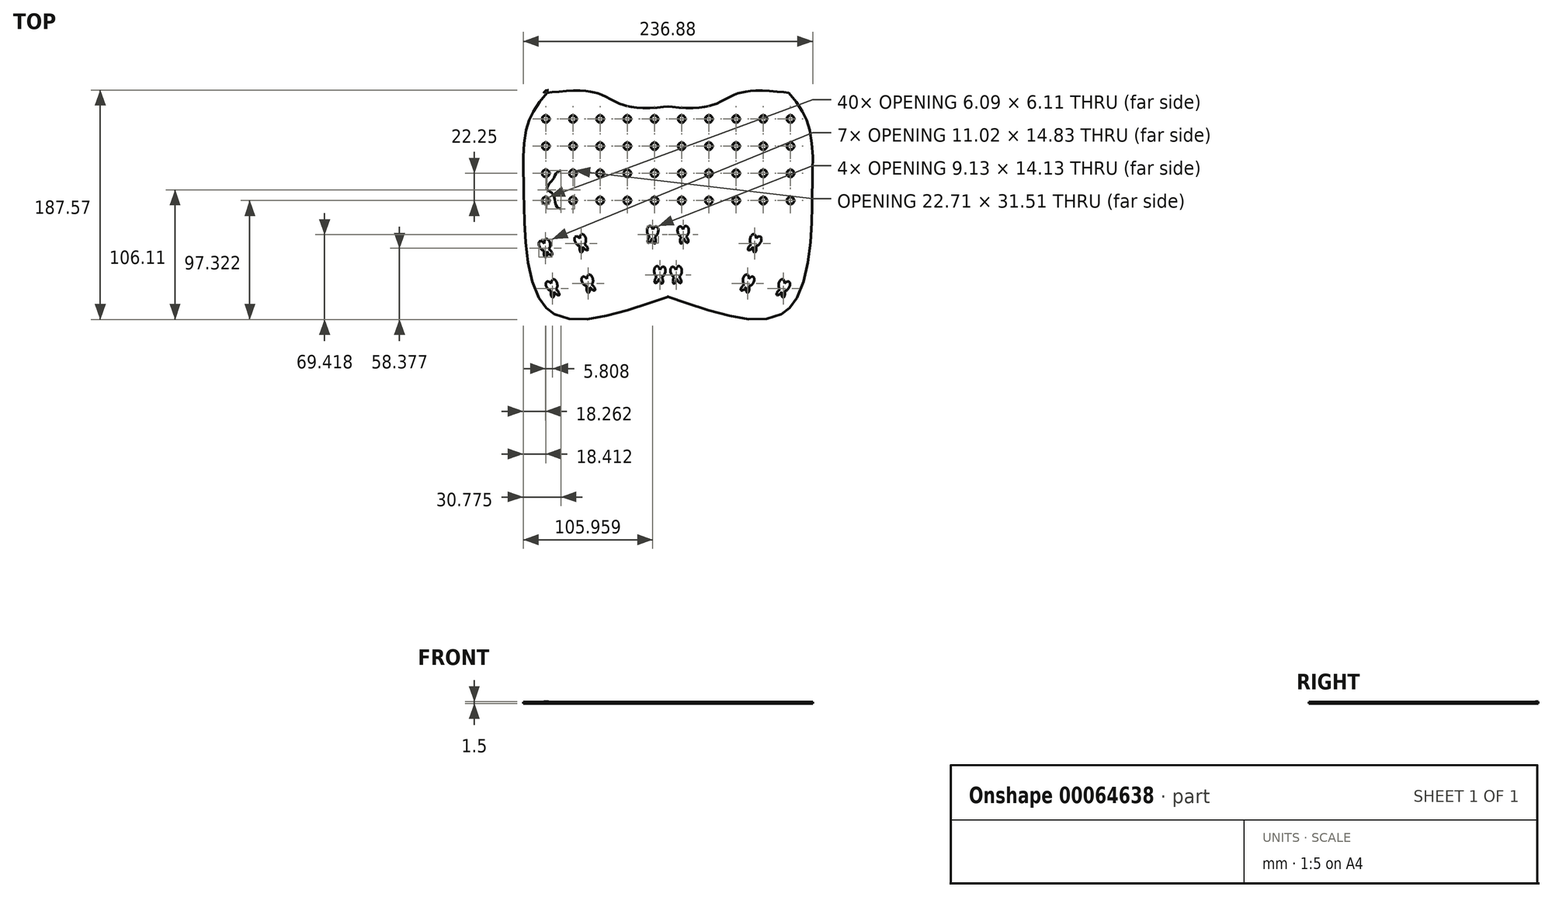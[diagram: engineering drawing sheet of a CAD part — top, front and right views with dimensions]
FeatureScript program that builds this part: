
annotation { "Feature Type Name" : "Feature", "Feature Type Description" : "" }
export const myFeature = defineFeature(function(context is Context, id is Id, definition is map)
    precondition{}
    {
        {
            var Q0;
            Q0=qCreatedBy(makeId("Top.planeOp"),FACE);
            var sketch = newSketch(context, id + "F0", { "sketchPlane" : qUnion([Q0])});
            skLineSegment(sketch, "E0", {"start": v(-116.5, 0) * mm, "end": v(139.03, 0) * mm, "construction": true});
            skLineSegment(sketch, "E1.0", {"start": v(-116.5, -90) * mm, "end": v(139.03, -90) * mm, "construction": true});
            skLineSegment(sketch, "E2.0", {"start": v(-116.5, 90) * mm, "end": v(139.03, 90) * mm, "construction": true});
            skLineSegment(sketch, "E3", {"start": v(0, 90) * mm, "end": v(0, -92.69) * mm, "construction": true});
            skLineSegment(sketch, "E4.0", {"start": v(-100, 90) * mm, "end": v(-100, -92.69) * mm, "construction": true});
            skLineSegment(sketch, "E5.0", {"start": v(-120, 90) * mm, "end": v(-120, -92.69) * mm, "construction": true});
            skLineSegment(sketch, "E6.0", {"start": v(120, 90) * mm, "end": v(120, -92.69) * mm, "construction": true});
            skLineSegment(sketch, "E7.0", {"start": v(100, 90) * mm, "end": v(100, -92.69) * mm, "construction": true});
            skFitSpline(sketch, "E8", {"points": [v(-100, 90) * mm, v(-114.02, 69.47) * mm, v(-120, 43.4) * mm, v(-120, 8.31) * mm, v(-100, -90) * mm, v(0, -80.79) * mm], "startDerivative": vector(-114.58, -138.92) * mm, "endDerivative": vector(433.2, 151.03) * mm});
            skFitSpline(sketch, "E9", {"points": [v(0, 78.79) * mm, v(-34.86, 79.72) * mm, v(-58.45, 90) * mm, v(-100, 90) * mm], "startDerivative": vector(-110.99, -8.68) * mm, "endDerivative": vector(-123.02, -12.63) * mm});
            skArc(sketch, "E10.filletArc", {"start": v(-97.54, 90.25) * mm, "mid": v(-99.77, 89.57) * mm, "end": v(-101.57, 88.09) * mm});
            skFitSpline(sketch, "E11.MirrorCS", {"points": [v(0, 78.79) * mm, v(34.86, 79.72) * mm, v(58.45, 90) * mm, v(100, 90) * mm], "startDerivative": vector(110.99, -8.68) * mm, "endDerivative": vector(123.02, -12.63) * mm});
            skFitSpline(sketch, "E12.MirrorCS", {"points": [v(100, 90) * mm, v(114.02, 69.47) * mm, v(120, 43.4) * mm, v(120, 8.31) * mm, v(100, -90) * mm, v(0, -80.79) * mm], "startDerivative": vector(114.58, -138.92) * mm, "endDerivative": vector(-433.2, 151.03) * mm});
            skArc(sketch, "E13.MirrorCS", {"start": v(97.54, 90.25) * mm, "mid": v(99.77, 89.57) * mm, "end": v(101.57, 88.09) * mm});
            skFitSpline(sketch, "E14.0", {"points": [v(0.16, 76.8) * mm, v(-2.16, 76.61) * mm, v(-6.8, 76.25) * mm, v(-13.69, 75.85) * mm, v(-20.42, 75.74) * mm, v(-25.82, 76.02) * mm, v(-29.97, 76.55) * mm, v(-32.48, 77.03) * mm, v(-34.44, 77.51) * mm, v(-36.35, 78.06) * mm, v(-38.65, 78.88) * mm, v(-41.26, 80) * mm, v(-44.61, 81.61) * mm, v(-47.82, 83.32) * mm, v(-51.02, 84.95) * mm, v(-53.45, 86.09) * mm, v(-55.94, 87.11) * mm, v(-58.1, 87.84) * mm, v(-59.9, 88.32) * mm, v(-61.76, 88.75) * mm, v(-64.2, 89.18) * mm, v(-67.3, 89.53) * mm, v(-71.61, 89.8) * mm, v(-77.33, 89.83) * mm, v(-84.6, 89.45) * mm, v(-92.12, 88.8) * mm, v(-97.23, 88.27) * mm, v(-99.8, 88.01) * mm]});
            skFitSpline(sketch, "E15.0", {"points": [v(-0.16, 76.8) * mm, v(2.16, 76.61) * mm, v(6.8, 76.25) * mm, v(13.69, 75.85) * mm, v(20.42, 75.74) * mm, v(25.82, 76.02) * mm, v(29.97, 76.55) * mm, v(32.48, 77.03) * mm, v(34.44, 77.51) * mm, v(36.35, 78.06) * mm, v(38.65, 78.88) * mm, v(41.26, 80) * mm, v(44.61, 81.61) * mm, v(47.82, 83.32) * mm, v(51.02, 84.95) * mm, v(53.45, 86.09) * mm, v(55.94, 87.11) * mm, v(58.1, 87.84) * mm, v(59.9, 88.32) * mm, v(61.76, 88.75) * mm, v(64.2, 89.18) * mm, v(67.3, 89.53) * mm, v(71.61, 89.8) * mm, v(77.33, 89.83) * mm, v(84.6, 89.45) * mm, v(92.12, 88.8) * mm, v(97.23, 88.27) * mm, v(99.8, 88.01) * mm]});
            skFitSpline(sketch, "E16.0", {"points": [v(98.46, 88.73) * mm, v(99.65, 87.28) * mm, v(102.03, 84.4) * mm, v(105.43, 80.03) * mm, v(108.04, 76.27) * mm, v(109.92, 73.15) * mm, v(111.23, 70.74) * mm, v(112.4, 68.25) * mm, v(113.46, 65.66) * mm, v(114.39, 62.97) * mm, v(115.47, 59.3) * mm, v(116.56, 54.56) * mm, v(117.47, 48.83) * mm, v(118.05, 43.2) * mm, v(118.35, 37.81) * mm, v(118.44, 32.29) * mm, v(118.37, 26.22) * mm, v(118.24, 20.4) * mm, v(118.12, 15.08) * mm, v(118.05, 11.45) * mm, v(118, 8.34) * mm, v(117.95, 5.08) * mm, v(117.9, 0.76) * mm, v(117.8, -4.78) * mm, v(117.63, -12.53) * mm, v(117.26, -22.79) * mm, v(116.37, -35.51) * mm, v(114.87, -48.17) * mm, v(112.6, -60.27) * mm, v(109.38, -71.31) * mm, v(105.8, -79.21) * mm, v(102.33, -84.5) * mm, v(99.92, -87.34) * mm, v(97.83, -89.3) * mm, v(95.62, -91.08) * mm, v(91.46, -93.7) * mm, v(84.64, -96.16) * mm, v(75.12, -97.29) * mm, v(64.45, -96.8) * mm, v(52.83, -94.9) * mm, v(40.45, -91.9) * mm, v(23.2, -86.76) * mm, v(9.68, -82.05) * mm, v(0.66, -78.9) * mm]});
            skFitSpline(sketch, "E17.0", {"points": [v(-98.46, 88.73) * mm, v(-99.65, 87.28) * mm, v(-102.03, 84.4) * mm, v(-105.43, 80.03) * mm, v(-108.04, 76.27) * mm, v(-109.92, 73.15) * mm, v(-111.23, 70.74) * mm, v(-112.4, 68.25) * mm, v(-113.46, 65.66) * mm, v(-114.39, 62.97) * mm, v(-115.47, 59.3) * mm, v(-116.56, 54.56) * mm, v(-117.47, 48.83) * mm, v(-118.05, 43.2) * mm, v(-118.35, 37.81) * mm, v(-118.44, 32.29) * mm, v(-118.37, 26.22) * mm, v(-118.24, 20.4) * mm, v(-118.12, 15.08) * mm, v(-118.05, 11.45) * mm, v(-118, 8.34) * mm, v(-117.95, 5.08) * mm, v(-117.9, 0.76) * mm, v(-117.8, -4.78) * mm, v(-117.63, -12.53) * mm, v(-117.26, -22.79) * mm, v(-116.37, -35.51) * mm, v(-114.87, -48.17) * mm, v(-112.6, -60.27) * mm, v(-109.38, -71.31) * mm, v(-105.8, -79.21) * mm, v(-102.33, -84.5) * mm, v(-99.92, -87.34) * mm, v(-97.83, -89.3) * mm, v(-95.62, -91.08) * mm, v(-91.46, -93.7) * mm, v(-84.64, -96.16) * mm, v(-75.12, -97.29) * mm, v(-64.45, -96.8) * mm, v(-52.83, -94.9) * mm, v(-40.45, -91.9) * mm, v(-23.2, -86.76) * mm, v(-9.68, -82.05) * mm, v(-0.66, -78.9) * mm]});
            skFitSpline(sketch, "E18", {"points": [v(-0.66, -78.9) * mm, v(0, -78.63) * mm, v(0.66, -78.9) * mm], "startDerivative": vector(1.32, 0.81) * mm, "endDerivative": vector(1.32, -0.81) * mm});
            skArc(sketch, "E19.filletArc", {"start": v(100.56, 86.17) * mm, "mid": v(98.75, 87.66) * mm, "end": v(96.52, 88.35) * mm});
            skArc(sketch, "E20.filletArc", {"start": v(-96.52, 88.35) * mm, "mid": v(-98.75, 87.66) * mm, "end": v(-100.56, 86.17) * mm});
            skCircle(sketch, "E21", {"center": v(-100, 0) * mm, "radius": 2.04 * mm});
            skEllipticalArc(sketch, "E22", {});
            skEllipticalArc(sketch, "E23.1.0", {});
            skEllipticalArc(sketch, "E23.2.0", {});
            skEllipticalArc(sketch, "E24.1.3.0", {});
            skEllipticalArc(sketch, "E24.1.4.0", {});
            skEllipticalArc(sketch, "E24.1.5.0", {});
            skEllipticalArc(sketch, "E24.1.6.0", {});
            skEllipticalArc(sketch, "E24.1.7.0", {});
            skEllipticalArc(sketch, "E24.1.8.0", {});
            skEllipticalArc(sketch, "E24.1.9.0", {});
            skEllipticalArc(sketch, "E24.1.10.0", {});
            skEllipticalArc(sketch, "E24.1.11.0", {});
            skEllipticalArc(sketch, "E24.1.12.0", {});
            skEllipticalArc(sketch, "E24.1.13.0", {});
            skEllipticalArc(sketch, "E24.1.14.0", {});
            skEllipticalArc(sketch, "E25.trimOffspring", {});
            skEllipticalArc(sketch, "E26.trimOffspring", {});
            skEllipticalArc(sketch, "E27.trimOffspring", {});
            skEllipticalArc(sketch, "E28.trimOffspring", {});
            skEllipticalArc(sketch, "E29.trimOffspring", {});
            skEllipticalArc(sketch, "E30.trimOffspring", {});
            skEllipticalArc(sketch, "E31.trimOffspring", {});
            skEllipticalArc(sketch, "E32.trimOffspring", {});
            skEllipticalArc(sketch, "E33.trimOffspring", {});
            skEllipticalArc(sketch, "E34.trimOffspring", {});
            skEllipticalArc(sketch, "E35.trimOffspring", {});
            skEllipticalArc(sketch, "E36.trimOffspring", {});
            skEllipticalArc(sketch, "E37.trimOffspring", {});
            skEllipticalArc(sketch, "E38.trimOffspring", {});
            skEllipticalArc(sketch, "E39.trimOffspring", {});
            skEllipticalArc(sketch, "E40.0.1.0", {});
            skEllipticalArc(sketch, "E40.0.1.1", {});
            skEllipticalArc(sketch, "E40.0.1.2", {});
            skEllipticalArc(sketch, "E40.0.1.3", {});
            skEllipticalArc(sketch, "E40.0.1.4", {});
            skEllipticalArc(sketch, "E40.0.1.5", {});
            skEllipticalArc(sketch, "E40.0.1.6", {});
            skEllipticalArc(sketch, "E40.0.1.7", {});
            skEllipticalArc(sketch, "E40.0.1.8", {});
            skEllipticalArc(sketch, "E40.0.1.9", {});
            skEllipticalArc(sketch, "E40.0.1.10", {});
            skEllipticalArc(sketch, "E40.0.1.11", {});
            skEllipticalArc(sketch, "E40.0.1.12", {});
            skEllipticalArc(sketch, "E40.0.1.13", {});
            skEllipticalArc(sketch, "E40.0.1.14", {});
            skEllipticalArc(sketch, "E40.0.2.0", {});
            skEllipticalArc(sketch, "E40.0.2.1", {});
            skEllipticalArc(sketch, "E40.0.2.2", {});
            skEllipticalArc(sketch, "E40.0.2.3", {});
            skEllipticalArc(sketch, "E40.0.2.4", {});
            skEllipticalArc(sketch, "E40.0.2.5", {});
            skEllipticalArc(sketch, "E40.0.2.6", {});
            skEllipticalArc(sketch, "E40.0.2.7", {});
            skEllipticalArc(sketch, "E40.0.2.8", {});
            skEllipticalArc(sketch, "E40.0.2.9", {});
            skEllipticalArc(sketch, "E40.0.2.10", {});
            skEllipticalArc(sketch, "E40.0.2.11", {});
            skEllipticalArc(sketch, "E40.0.2.12", {});
            skEllipticalArc(sketch, "E40.0.2.13", {});
            skEllipticalArc(sketch, "E40.0.2.14", {});
            skEllipticalArc(sketch, "E40.0.3.0", {});
            skEllipticalArc(sketch, "E40.0.3.1", {});
            skEllipticalArc(sketch, "E40.0.3.2", {});
            skEllipticalArc(sketch, "E40.0.3.3", {});
            skEllipticalArc(sketch, "E40.0.3.4", {});
            skEllipticalArc(sketch, "E40.0.3.5", {});
            skEllipticalArc(sketch, "E40.0.3.6", {});
            skEllipticalArc(sketch, "E40.0.3.7", {});
            skEllipticalArc(sketch, "E40.0.3.8", {});
            skEllipticalArc(sketch, "E40.0.3.9", {});
            skEllipticalArc(sketch, "E40.0.3.10", {});
            skEllipticalArc(sketch, "E40.0.3.11", {});
            skEllipticalArc(sketch, "E40.0.3.12", {});
            skEllipticalArc(sketch, "E40.0.3.13", {});
            skEllipticalArc(sketch, "E40.0.3.14", {});
            skEllipticalArc(sketch, "E40.1.0.0", {});
            skEllipticalArc(sketch, "E40.1.0.1", {});
            skEllipticalArc(sketch, "E40.1.0.2", {});
            skEllipticalArc(sketch, "E40.1.0.3", {});
            skEllipticalArc(sketch, "E40.1.0.4", {});
            skEllipticalArc(sketch, "E40.1.0.5", {});
            skEllipticalArc(sketch, "E40.1.0.6", {});
            skEllipticalArc(sketch, "E40.1.0.7", {});
            skEllipticalArc(sketch, "E40.1.0.8", {});
            skEllipticalArc(sketch, "E40.1.0.9", {});
            skEllipticalArc(sketch, "E40.1.0.10", {});
            skEllipticalArc(sketch, "E40.1.0.11", {});
            skEllipticalArc(sketch, "E40.1.0.12", {});
            skEllipticalArc(sketch, "E40.1.0.13", {});
            skEllipticalArc(sketch, "E40.1.0.14", {});
            skEllipticalArc(sketch, "E40.1.1.0", {});
            skEllipticalArc(sketch, "E40.1.1.1", {});
            skEllipticalArc(sketch, "E40.1.1.2", {});
            skEllipticalArc(sketch, "E40.1.1.3", {});
            skEllipticalArc(sketch, "E40.1.1.4", {});
            skEllipticalArc(sketch, "E40.1.1.5", {});
            skEllipticalArc(sketch, "E40.1.1.6", {});
            skEllipticalArc(sketch, "E40.1.1.7", {});
            skEllipticalArc(sketch, "E40.1.1.8", {});
            skEllipticalArc(sketch, "E40.1.1.9", {});
            skEllipticalArc(sketch, "E40.1.1.10", {});
            skEllipticalArc(sketch, "E40.1.1.11", {});
            skEllipticalArc(sketch, "E40.1.1.12", {});
            skEllipticalArc(sketch, "E40.1.1.13", {});
            skEllipticalArc(sketch, "E40.1.1.14", {});
            skEllipticalArc(sketch, "E40.1.2.0", {});
            skEllipticalArc(sketch, "E40.1.2.1", {});
            skEllipticalArc(sketch, "E40.1.2.2", {});
            skEllipticalArc(sketch, "E40.1.2.3", {});
            skEllipticalArc(sketch, "E40.1.2.4", {});
            skEllipticalArc(sketch, "E40.1.2.5", {});
            skEllipticalArc(sketch, "E40.1.2.6", {});
            skEllipticalArc(sketch, "E40.1.2.7", {});
            skEllipticalArc(sketch, "E40.1.2.8", {});
            skEllipticalArc(sketch, "E40.1.2.9", {});
            skEllipticalArc(sketch, "E40.1.2.10", {});
            skEllipticalArc(sketch, "E40.1.2.11", {});
            skEllipticalArc(sketch, "E40.1.2.12", {});
            skEllipticalArc(sketch, "E40.1.2.13", {});
            skEllipticalArc(sketch, "E40.1.2.14", {});
            skEllipticalArc(sketch, "E40.1.3.0", {});
            skEllipticalArc(sketch, "E40.1.3.1", {});
            skEllipticalArc(sketch, "E40.1.3.2", {});
            skEllipticalArc(sketch, "E40.1.3.3", {});
            skEllipticalArc(sketch, "E40.1.3.4", {});
            skEllipticalArc(sketch, "E40.1.3.5", {});
            skEllipticalArc(sketch, "E40.1.3.6", {});
            skEllipticalArc(sketch, "E40.1.3.7", {});
            skEllipticalArc(sketch, "E40.1.3.8", {});
            skEllipticalArc(sketch, "E40.1.3.9", {});
            skEllipticalArc(sketch, "E40.1.3.10", {});
            skEllipticalArc(sketch, "E40.1.3.11", {});
            skEllipticalArc(sketch, "E40.1.3.12", {});
            skEllipticalArc(sketch, "E40.1.3.13", {});
            skEllipticalArc(sketch, "E40.1.3.14", {});
            skEllipticalArc(sketch, "E40.2.0.0", {});
            skEllipticalArc(sketch, "E40.2.0.1", {});
            skEllipticalArc(sketch, "E40.2.0.2", {});
            skEllipticalArc(sketch, "E40.2.0.3", {});
            skEllipticalArc(sketch, "E40.2.0.4", {});
            skEllipticalArc(sketch, "E40.2.0.5", {});
            skEllipticalArc(sketch, "E40.2.0.6", {});
            skEllipticalArc(sketch, "E40.2.0.7", {});
            skEllipticalArc(sketch, "E40.2.0.8", {});
            skEllipticalArc(sketch, "E40.2.0.9", {});
            skEllipticalArc(sketch, "E40.2.0.10", {});
            skEllipticalArc(sketch, "E40.2.0.11", {});
            skEllipticalArc(sketch, "E40.2.0.12", {});
            skEllipticalArc(sketch, "E40.2.0.13", {});
            skEllipticalArc(sketch, "E40.2.0.14", {});
            skEllipticalArc(sketch, "E40.2.1.0", {});
            skEllipticalArc(sketch, "E40.2.1.1", {});
            skEllipticalArc(sketch, "E40.2.1.2", {});
            skEllipticalArc(sketch, "E40.2.1.3", {});
            skEllipticalArc(sketch, "E40.2.1.4", {});
            skEllipticalArc(sketch, "E40.2.1.5", {});
            skEllipticalArc(sketch, "E40.2.1.6", {});
            skEllipticalArc(sketch, "E40.2.1.7", {});
            skEllipticalArc(sketch, "E40.2.1.8", {});
            skEllipticalArc(sketch, "E40.2.1.9", {});
            skEllipticalArc(sketch, "E40.2.1.10", {});
            skEllipticalArc(sketch, "E40.2.1.11", {});
            skEllipticalArc(sketch, "E40.2.1.12", {});
            skEllipticalArc(sketch, "E40.2.1.13", {});
            skEllipticalArc(sketch, "E40.2.1.14", {});
            skEllipticalArc(sketch, "E40.2.2.0", {});
            skEllipticalArc(sketch, "E40.2.2.1", {});
            skEllipticalArc(sketch, "E40.2.2.2", {});
            skEllipticalArc(sketch, "E40.2.2.3", {});
            skEllipticalArc(sketch, "E40.2.2.4", {});
            skEllipticalArc(sketch, "E40.2.2.5", {});
            skEllipticalArc(sketch, "E40.2.2.6", {});
            skEllipticalArc(sketch, "E40.2.2.7", {});
            skEllipticalArc(sketch, "E40.2.2.8", {});
            skEllipticalArc(sketch, "E40.2.2.9", {});
            skEllipticalArc(sketch, "E40.2.2.10", {});
            skEllipticalArc(sketch, "E40.2.2.11", {});
            skEllipticalArc(sketch, "E40.2.2.12", {});
            skEllipticalArc(sketch, "E40.2.2.13", {});
            skEllipticalArc(sketch, "E40.2.2.14", {});
            skEllipticalArc(sketch, "E40.2.3.0", {});
            skEllipticalArc(sketch, "E40.2.3.1", {});
            skEllipticalArc(sketch, "E40.2.3.2", {});
            skEllipticalArc(sketch, "E40.2.3.3", {});
            skEllipticalArc(sketch, "E40.2.3.4", {});
            skEllipticalArc(sketch, "E40.2.3.5", {});
            skEllipticalArc(sketch, "E40.2.3.6", {});
            skEllipticalArc(sketch, "E40.2.3.7", {});
            skEllipticalArc(sketch, "E40.2.3.8", {});
            skEllipticalArc(sketch, "E40.2.3.9", {});
            skEllipticalArc(sketch, "E40.2.3.10", {});
            skEllipticalArc(sketch, "E40.2.3.11", {});
            skEllipticalArc(sketch, "E40.2.3.12", {});
            skEllipticalArc(sketch, "E40.2.3.13", {});
            skEllipticalArc(sketch, "E40.2.3.14", {});
            skEllipticalArc(sketch, "E40.3.0.0", {});
            skEllipticalArc(sketch, "E40.3.0.1", {});
            skEllipticalArc(sketch, "E40.3.0.2", {});
            skEllipticalArc(sketch, "E40.3.0.3", {});
            skEllipticalArc(sketch, "E40.3.0.4", {});
            skEllipticalArc(sketch, "E40.3.0.5", {});
            skEllipticalArc(sketch, "E40.3.0.6", {});
            skEllipticalArc(sketch, "E40.3.0.7", {});
            skEllipticalArc(sketch, "E40.3.0.8", {});
            skEllipticalArc(sketch, "E40.3.0.9", {});
            skEllipticalArc(sketch, "E40.3.0.10", {});
            skEllipticalArc(sketch, "E40.3.0.11", {});
            skEllipticalArc(sketch, "E40.3.0.12", {});
            skEllipticalArc(sketch, "E40.3.0.13", {});
            skEllipticalArc(sketch, "E40.3.0.14", {});
            skEllipticalArc(sketch, "E40.3.1.0", {});
            skEllipticalArc(sketch, "E40.3.1.1", {});
            skEllipticalArc(sketch, "E40.3.1.2", {});
            skEllipticalArc(sketch, "E40.3.1.3", {});
            skEllipticalArc(sketch, "E40.3.1.4", {});
            skEllipticalArc(sketch, "E40.3.1.5", {});
            skEllipticalArc(sketch, "E40.3.1.6", {});
            skEllipticalArc(sketch, "E40.3.1.7", {});
            skEllipticalArc(sketch, "E40.3.1.8", {});
            skEllipticalArc(sketch, "E40.3.1.9", {});
            skEllipticalArc(sketch, "E40.3.1.10", {});
            skEllipticalArc(sketch, "E40.3.1.11", {});
            skEllipticalArc(sketch, "E40.3.1.12", {});
            skEllipticalArc(sketch, "E40.3.1.13", {});
            skEllipticalArc(sketch, "E40.3.1.14", {});
            skEllipticalArc(sketch, "E40.3.2.0", {});
            skEllipticalArc(sketch, "E40.3.2.1", {});
            skEllipticalArc(sketch, "E40.3.2.2", {});
            skEllipticalArc(sketch, "E40.3.2.3", {});
            skEllipticalArc(sketch, "E40.3.2.4", {});
            skEllipticalArc(sketch, "E40.3.2.5", {});
            skEllipticalArc(sketch, "E40.3.2.6", {});
            skEllipticalArc(sketch, "E40.3.2.7", {});
            skEllipticalArc(sketch, "E40.3.2.8", {});
            skEllipticalArc(sketch, "E40.3.2.9", {});
            skEllipticalArc(sketch, "E40.3.2.10", {});
            skEllipticalArc(sketch, "E40.3.2.11", {});
            skEllipticalArc(sketch, "E40.3.2.12", {});
            skEllipticalArc(sketch, "E40.3.2.13", {});
            skEllipticalArc(sketch, "E40.3.2.14", {});
            skEllipticalArc(sketch, "E40.3.3.0", {});
            skEllipticalArc(sketch, "E40.3.3.1", {});
            skEllipticalArc(sketch, "E40.3.3.2", {});
            skEllipticalArc(sketch, "E40.3.3.3", {});
            skEllipticalArc(sketch, "E40.3.3.4", {});
            skEllipticalArc(sketch, "E40.3.3.5", {});
            skEllipticalArc(sketch, "E40.3.3.6", {});
            skEllipticalArc(sketch, "E40.3.3.7", {});
            skEllipticalArc(sketch, "E40.3.3.8", {});
            skEllipticalArc(sketch, "E40.3.3.9", {});
            skEllipticalArc(sketch, "E40.3.3.10", {});
            skEllipticalArc(sketch, "E40.3.3.11", {});
            skEllipticalArc(sketch, "E40.3.3.12", {});
            skEllipticalArc(sketch, "E40.3.3.13", {});
            skEllipticalArc(sketch, "E40.3.3.14", {});
            skEllipticalArc(sketch, "E40.4.0.0", {});
            skEllipticalArc(sketch, "E40.4.0.1", {});
            skEllipticalArc(sketch, "E40.4.0.2", {});
            skEllipticalArc(sketch, "E40.4.0.3", {});
            skEllipticalArc(sketch, "E40.4.0.4", {});
            skEllipticalArc(sketch, "E40.4.0.5", {});
            skEllipticalArc(sketch, "E40.4.0.6", {});
            skEllipticalArc(sketch, "E40.4.0.7", {});
            skEllipticalArc(sketch, "E40.4.0.8", {});
            skEllipticalArc(sketch, "E40.4.0.9", {});
            skEllipticalArc(sketch, "E40.4.0.10", {});
            skEllipticalArc(sketch, "E40.4.0.11", {});
            skEllipticalArc(sketch, "E40.4.0.12", {});
            skEllipticalArc(sketch, "E40.4.0.13", {});
            skEllipticalArc(sketch, "E40.4.0.14", {});
            skEllipticalArc(sketch, "E40.4.1.0", {});
            skEllipticalArc(sketch, "E40.4.1.1", {});
            skEllipticalArc(sketch, "E40.4.1.2", {});
            skEllipticalArc(sketch, "E40.4.1.3", {});
            skEllipticalArc(sketch, "E40.4.1.4", {});
            skEllipticalArc(sketch, "E40.4.1.5", {});
            skEllipticalArc(sketch, "E40.4.1.6", {});
            skEllipticalArc(sketch, "E40.4.1.7", {});
            skEllipticalArc(sketch, "E40.4.1.8", {});
            skEllipticalArc(sketch, "E40.4.1.9", {});
            skEllipticalArc(sketch, "E40.4.1.10", {});
            skEllipticalArc(sketch, "E40.4.1.11", {});
            skEllipticalArc(sketch, "E40.4.1.12", {});
            skEllipticalArc(sketch, "E40.4.1.13", {});
            skEllipticalArc(sketch, "E40.4.1.14", {});
            skEllipticalArc(sketch, "E40.4.2.0", {});
            skEllipticalArc(sketch, "E40.4.2.1", {});
            skEllipticalArc(sketch, "E40.4.2.2", {});
            skEllipticalArc(sketch, "E40.4.2.3", {});
            skEllipticalArc(sketch, "E40.4.2.4", {});
            skEllipticalArc(sketch, "E40.4.2.5", {});
            skEllipticalArc(sketch, "E40.4.2.6", {});
            skEllipticalArc(sketch, "E40.4.2.7", {});
            skEllipticalArc(sketch, "E40.4.2.8", {});
            skEllipticalArc(sketch, "E40.4.2.9", {});
            skEllipticalArc(sketch, "E40.4.2.10", {});
            skEllipticalArc(sketch, "E40.4.2.11", {});
            skEllipticalArc(sketch, "E40.4.2.12", {});
            skEllipticalArc(sketch, "E40.4.2.13", {});
            skEllipticalArc(sketch, "E40.4.2.14", {});
            skEllipticalArc(sketch, "E40.4.3.0", {});
            skEllipticalArc(sketch, "E40.4.3.1", {});
            skEllipticalArc(sketch, "E40.4.3.2", {});
            skEllipticalArc(sketch, "E40.4.3.3", {});
            skEllipticalArc(sketch, "E40.4.3.4", {});
            skEllipticalArc(sketch, "E40.4.3.5", {});
            skEllipticalArc(sketch, "E40.4.3.6", {});
            skEllipticalArc(sketch, "E40.4.3.7", {});
            skEllipticalArc(sketch, "E40.4.3.8", {});
            skEllipticalArc(sketch, "E40.4.3.9", {});
            skEllipticalArc(sketch, "E40.4.3.10", {});
            skEllipticalArc(sketch, "E40.4.3.11", {});
            skEllipticalArc(sketch, "E40.4.3.12", {});
            skEllipticalArc(sketch, "E40.4.3.13", {});
            skEllipticalArc(sketch, "E40.4.3.14", {});
            skEllipticalArc(sketch, "E40.5.0.0", {});
            skEllipticalArc(sketch, "E40.5.0.1", {});
            skEllipticalArc(sketch, "E40.5.0.2", {});
            skEllipticalArc(sketch, "E40.5.0.3", {});
            skEllipticalArc(sketch, "E40.5.0.4", {});
            skEllipticalArc(sketch, "E40.5.0.5", {});
            skEllipticalArc(sketch, "E40.5.0.6", {});
            skEllipticalArc(sketch, "E40.5.0.7", {});
            skEllipticalArc(sketch, "E40.5.0.8", {});
            skEllipticalArc(sketch, "E40.5.0.9", {});
            skEllipticalArc(sketch, "E40.5.0.10", {});
            skEllipticalArc(sketch, "E40.5.0.11", {});
            skEllipticalArc(sketch, "E40.5.0.12", {});
            skEllipticalArc(sketch, "E40.5.0.13", {});
            skEllipticalArc(sketch, "E40.5.0.14", {});
            skEllipticalArc(sketch, "E40.5.1.0", {});
            skEllipticalArc(sketch, "E40.5.1.1", {});
            skEllipticalArc(sketch, "E40.5.1.2", {});
            skEllipticalArc(sketch, "E40.5.1.3", {});
            skEllipticalArc(sketch, "E40.5.1.4", {});
            skEllipticalArc(sketch, "E40.5.1.5", {});
            skEllipticalArc(sketch, "E40.5.1.6", {});
            skEllipticalArc(sketch, "E40.5.1.7", {});
            skEllipticalArc(sketch, "E40.5.1.8", {});
            skEllipticalArc(sketch, "E40.5.1.9", {});
            skEllipticalArc(sketch, "E40.5.1.10", {});
            skEllipticalArc(sketch, "E40.5.1.11", {});
            skEllipticalArc(sketch, "E40.5.1.12", {});
            skEllipticalArc(sketch, "E40.5.1.13", {});
            skEllipticalArc(sketch, "E40.5.1.14", {});
            skEllipticalArc(sketch, "E40.5.2.0", {});
            skEllipticalArc(sketch, "E40.5.2.1", {});
            skEllipticalArc(sketch, "E40.5.2.2", {});
            skEllipticalArc(sketch, "E40.5.2.3", {});
            skEllipticalArc(sketch, "E40.5.2.4", {});
            skEllipticalArc(sketch, "E40.5.2.5", {});
            skEllipticalArc(sketch, "E40.5.2.6", {});
            skEllipticalArc(sketch, "E40.5.2.7", {});
            skEllipticalArc(sketch, "E40.5.2.8", {});
            skEllipticalArc(sketch, "E40.5.2.9", {});
            skEllipticalArc(sketch, "E40.5.2.10", {});
            skEllipticalArc(sketch, "E40.5.2.11", {});
            skEllipticalArc(sketch, "E40.5.2.12", {});
            skEllipticalArc(sketch, "E40.5.2.13", {});
            skEllipticalArc(sketch, "E40.5.2.14", {});
            skEllipticalArc(sketch, "E40.5.3.0", {});
            skEllipticalArc(sketch, "E40.5.3.1", {});
            skEllipticalArc(sketch, "E40.5.3.2", {});
            skEllipticalArc(sketch, "E40.5.3.3", {});
            skEllipticalArc(sketch, "E40.5.3.4", {});
            skEllipticalArc(sketch, "E40.5.3.5", {});
            skEllipticalArc(sketch, "E40.5.3.6", {});
            skEllipticalArc(sketch, "E40.5.3.7", {});
            skEllipticalArc(sketch, "E40.5.3.8", {});
            skEllipticalArc(sketch, "E40.5.3.9", {});
            skEllipticalArc(sketch, "E40.5.3.10", {});
            skEllipticalArc(sketch, "E40.5.3.11", {});
            skEllipticalArc(sketch, "E40.5.3.12", {});
            skEllipticalArc(sketch, "E40.5.3.13", {});
            skEllipticalArc(sketch, "E40.5.3.14", {});
            skEllipticalArc(sketch, "E40.6.0.0", {});
            skEllipticalArc(sketch, "E40.6.0.1", {});
            skEllipticalArc(sketch, "E40.6.0.2", {});
            skEllipticalArc(sketch, "E40.6.0.3", {});
            skEllipticalArc(sketch, "E40.6.0.4", {});
            skEllipticalArc(sketch, "E40.6.0.5", {});
            skEllipticalArc(sketch, "E40.6.0.6", {});
            skEllipticalArc(sketch, "E40.6.0.7", {});
            skEllipticalArc(sketch, "E40.6.0.8", {});
            skEllipticalArc(sketch, "E40.6.0.9", {});
            skEllipticalArc(sketch, "E40.6.0.10", {});
            skEllipticalArc(sketch, "E40.6.0.11", {});
            skEllipticalArc(sketch, "E40.6.0.12", {});
            skEllipticalArc(sketch, "E40.6.0.13", {});
            skEllipticalArc(sketch, "E40.6.0.14", {});
            skEllipticalArc(sketch, "E40.6.1.0", {});
            skEllipticalArc(sketch, "E40.6.1.1", {});
            skEllipticalArc(sketch, "E40.6.1.2", {});
            skEllipticalArc(sketch, "E40.6.1.3", {});
            skEllipticalArc(sketch, "E40.6.1.4", {});
            skEllipticalArc(sketch, "E40.6.1.5", {});
            skEllipticalArc(sketch, "E40.6.1.6", {});
            skEllipticalArc(sketch, "E40.6.1.7", {});
            skEllipticalArc(sketch, "E40.6.1.8", {});
            skEllipticalArc(sketch, "E40.6.1.9", {});
            skEllipticalArc(sketch, "E40.6.1.10", {});
            skEllipticalArc(sketch, "E40.6.1.11", {});
            skEllipticalArc(sketch, "E40.6.1.12", {});
            skEllipticalArc(sketch, "E40.6.1.13", {});
            skEllipticalArc(sketch, "E40.6.1.14", {});
            skEllipticalArc(sketch, "E40.6.2.0", {});
            skEllipticalArc(sketch, "E40.6.2.1", {});
            skEllipticalArc(sketch, "E40.6.2.2", {});
            skEllipticalArc(sketch, "E40.6.2.3", {});
            skEllipticalArc(sketch, "E40.6.2.4", {});
            skEllipticalArc(sketch, "E40.6.2.5", {});
            skEllipticalArc(sketch, "E40.6.2.6", {});
            skEllipticalArc(sketch, "E40.6.2.7", {});
            skEllipticalArc(sketch, "E40.6.2.8", {});
            skEllipticalArc(sketch, "E40.6.2.9", {});
            skEllipticalArc(sketch, "E40.6.2.10", {});
            skEllipticalArc(sketch, "E40.6.2.11", {});
            skEllipticalArc(sketch, "E40.6.2.12", {});
            skEllipticalArc(sketch, "E40.6.2.13", {});
            skEllipticalArc(sketch, "E40.6.2.14", {});
            skEllipticalArc(sketch, "E40.6.3.0", {});
            skEllipticalArc(sketch, "E40.6.3.1", {});
            skEllipticalArc(sketch, "E40.6.3.2", {});
            skEllipticalArc(sketch, "E40.6.3.3", {});
            skEllipticalArc(sketch, "E40.6.3.4", {});
            skEllipticalArc(sketch, "E40.6.3.5", {});
            skEllipticalArc(sketch, "E40.6.3.6", {});
            skEllipticalArc(sketch, "E40.6.3.7", {});
            skEllipticalArc(sketch, "E40.6.3.8", {});
            skEllipticalArc(sketch, "E40.6.3.9", {});
            skEllipticalArc(sketch, "E40.6.3.10", {});
            skEllipticalArc(sketch, "E40.6.3.11", {});
            skEllipticalArc(sketch, "E40.6.3.12", {});
            skEllipticalArc(sketch, "E40.6.3.13", {});
            skEllipticalArc(sketch, "E40.6.3.14", {});
            skEllipticalArc(sketch, "E40.7.0.0", {});
            skEllipticalArc(sketch, "E40.7.0.1", {});
            skEllipticalArc(sketch, "E40.7.0.2", {});
            skEllipticalArc(sketch, "E40.7.0.3", {});
            skEllipticalArc(sketch, "E40.7.0.4", {});
            skEllipticalArc(sketch, "E40.7.0.5", {});
            skEllipticalArc(sketch, "E40.7.0.6", {});
            skEllipticalArc(sketch, "E40.7.0.7", {});
            skEllipticalArc(sketch, "E40.7.0.8", {});
            skEllipticalArc(sketch, "E40.7.0.9", {});
            skEllipticalArc(sketch, "E40.7.0.10", {});
            skEllipticalArc(sketch, "E40.7.0.11", {});
            skEllipticalArc(sketch, "E40.7.0.12", {});
            skEllipticalArc(sketch, "E40.7.0.13", {});
            skEllipticalArc(sketch, "E40.7.0.14", {});
            skEllipticalArc(sketch, "E40.7.1.0", {});
            skEllipticalArc(sketch, "E40.7.1.1", {});
            skEllipticalArc(sketch, "E40.7.1.2", {});
            skEllipticalArc(sketch, "E40.7.1.3", {});
            skEllipticalArc(sketch, "E40.7.1.4", {});
            skEllipticalArc(sketch, "E40.7.1.5", {});
            skEllipticalArc(sketch, "E40.7.1.6", {});
            skEllipticalArc(sketch, "E40.7.1.7", {});
            skEllipticalArc(sketch, "E40.7.1.8", {});
            skEllipticalArc(sketch, "E40.7.1.9", {});
            skEllipticalArc(sketch, "E40.7.1.10", {});
            skEllipticalArc(sketch, "E40.7.1.11", {});
            skEllipticalArc(sketch, "E40.7.1.12", {});
            skEllipticalArc(sketch, "E40.7.1.13", {});
            skEllipticalArc(sketch, "E40.7.1.14", {});
            skEllipticalArc(sketch, "E40.7.2.0", {});
            skEllipticalArc(sketch, "E40.7.2.1", {});
            skEllipticalArc(sketch, "E40.7.2.2", {});
            skEllipticalArc(sketch, "E40.7.2.3", {});
            skEllipticalArc(sketch, "E40.7.2.4", {});
            skEllipticalArc(sketch, "E40.7.2.5", {});
            skEllipticalArc(sketch, "E40.7.2.6", {});
            skEllipticalArc(sketch, "E40.7.2.7", {});
            skEllipticalArc(sketch, "E40.7.2.8", {});
            skEllipticalArc(sketch, "E40.7.2.9", {});
            skEllipticalArc(sketch, "E40.7.2.10", {});
            skEllipticalArc(sketch, "E40.7.2.11", {});
            skEllipticalArc(sketch, "E40.7.2.12", {});
            skEllipticalArc(sketch, "E40.7.2.13", {});
            skEllipticalArc(sketch, "E40.7.2.14", {});
            skEllipticalArc(sketch, "E40.7.3.0", {});
            skEllipticalArc(sketch, "E40.7.3.1", {});
            skEllipticalArc(sketch, "E40.7.3.2", {});
            skEllipticalArc(sketch, "E40.7.3.3", {});
            skEllipticalArc(sketch, "E40.7.3.4", {});
            skEllipticalArc(sketch, "E40.7.3.5", {});
            skEllipticalArc(sketch, "E40.7.3.6", {});
            skEllipticalArc(sketch, "E40.7.3.7", {});
            skEllipticalArc(sketch, "E40.7.3.8", {});
            skEllipticalArc(sketch, "E40.7.3.9", {});
            skEllipticalArc(sketch, "E40.7.3.10", {});
            skEllipticalArc(sketch, "E40.7.3.11", {});
            skEllipticalArc(sketch, "E40.7.3.12", {});
            skEllipticalArc(sketch, "E40.7.3.13", {});
            skEllipticalArc(sketch, "E40.7.3.14", {});
            skEllipticalArc(sketch, "E40.8.0.0", {});
            skEllipticalArc(sketch, "E40.8.0.1", {});
            skEllipticalArc(sketch, "E40.8.0.2", {});
            skEllipticalArc(sketch, "E40.8.0.3", {});
            skEllipticalArc(sketch, "E40.8.0.4", {});
            skEllipticalArc(sketch, "E40.8.0.5", {});
            skEllipticalArc(sketch, "E40.8.0.6", {});
            skEllipticalArc(sketch, "E40.8.0.7", {});
            skEllipticalArc(sketch, "E40.8.0.8", {});
            skEllipticalArc(sketch, "E40.8.0.9", {});
            skEllipticalArc(sketch, "E40.8.0.10", {});
            skEllipticalArc(sketch, "E40.8.0.11", {});
            skEllipticalArc(sketch, "E40.8.0.12", {});
            skEllipticalArc(sketch, "E40.8.0.13", {});
            skEllipticalArc(sketch, "E40.8.0.14", {});
            skEllipticalArc(sketch, "E40.8.1.0", {});
            skEllipticalArc(sketch, "E40.8.1.1", {});
            skEllipticalArc(sketch, "E40.8.1.2", {});
            skEllipticalArc(sketch, "E40.8.1.3", {});
            skEllipticalArc(sketch, "E40.8.1.4", {});
            skEllipticalArc(sketch, "E40.8.1.5", {});
            skEllipticalArc(sketch, "E40.8.1.6", {});
            skEllipticalArc(sketch, "E40.8.1.7", {});
            skEllipticalArc(sketch, "E40.8.1.8", {});
            skEllipticalArc(sketch, "E40.8.1.9", {});
            skEllipticalArc(sketch, "E40.8.1.10", {});
            skEllipticalArc(sketch, "E40.8.1.11", {});
            skEllipticalArc(sketch, "E40.8.1.12", {});
            skEllipticalArc(sketch, "E40.8.1.13", {});
            skEllipticalArc(sketch, "E40.8.1.14", {});
            skEllipticalArc(sketch, "E40.8.2.0", {});
            skEllipticalArc(sketch, "E40.8.2.1", {});
            skEllipticalArc(sketch, "E40.8.2.2", {});
            skEllipticalArc(sketch, "E40.8.2.3", {});
            skEllipticalArc(sketch, "E40.8.2.4", {});
            skEllipticalArc(sketch, "E40.8.2.5", {});
            skEllipticalArc(sketch, "E40.8.2.6", {});
            skEllipticalArc(sketch, "E40.8.2.7", {});
            skEllipticalArc(sketch, "E40.8.2.8", {});
            skEllipticalArc(sketch, "E40.8.2.9", {});
            skEllipticalArc(sketch, "E40.8.2.10", {});
            skEllipticalArc(sketch, "E40.8.2.11", {});
            skEllipticalArc(sketch, "E40.8.2.12", {});
            skEllipticalArc(sketch, "E40.8.2.13", {});
            skEllipticalArc(sketch, "E40.8.2.14", {});
            skEllipticalArc(sketch, "E40.8.3.0", {});
            skEllipticalArc(sketch, "E40.8.3.1", {});
            skEllipticalArc(sketch, "E40.8.3.2", {});
            skEllipticalArc(sketch, "E40.8.3.3", {});
            skEllipticalArc(sketch, "E40.8.3.4", {});
            skEllipticalArc(sketch, "E40.8.3.5", {});
            skEllipticalArc(sketch, "E40.8.3.6", {});
            skEllipticalArc(sketch, "E40.8.3.7", {});
            skEllipticalArc(sketch, "E40.8.3.8", {});
            skEllipticalArc(sketch, "E40.8.3.9", {});
            skEllipticalArc(sketch, "E40.8.3.10", {});
            skEllipticalArc(sketch, "E40.8.3.11", {});
            skEllipticalArc(sketch, "E40.8.3.12", {});
            skEllipticalArc(sketch, "E40.8.3.13", {});
            skEllipticalArc(sketch, "E40.8.3.14", {});
            skEllipticalArc(sketch, "E40.9.0.0", {});
            skEllipticalArc(sketch, "E40.9.0.1", {});
            skEllipticalArc(sketch, "E40.9.0.2", {});
            skEllipticalArc(sketch, "E40.9.0.3", {});
            skEllipticalArc(sketch, "E40.9.0.4", {});
            skEllipticalArc(sketch, "E40.9.0.5", {});
            skEllipticalArc(sketch, "E40.9.0.6", {});
            skEllipticalArc(sketch, "E40.9.0.7", {});
            skEllipticalArc(sketch, "E40.9.0.8", {});
            skEllipticalArc(sketch, "E40.9.0.9", {});
            skEllipticalArc(sketch, "E40.9.0.10", {});
            skEllipticalArc(sketch, "E40.9.0.11", {});
            skEllipticalArc(sketch, "E40.9.0.12", {});
            skEllipticalArc(sketch, "E40.9.0.13", {});
            skEllipticalArc(sketch, "E40.9.0.14", {});
            skEllipticalArc(sketch, "E40.9.1.0", {});
            skEllipticalArc(sketch, "E40.9.1.1", {});
            skEllipticalArc(sketch, "E40.9.1.2", {});
            skEllipticalArc(sketch, "E40.9.1.3", {});
            skEllipticalArc(sketch, "E40.9.1.4", {});
            skEllipticalArc(sketch, "E40.9.1.5", {});
            skEllipticalArc(sketch, "E40.9.1.6", {});
            skEllipticalArc(sketch, "E40.9.1.7", {});
            skEllipticalArc(sketch, "E40.9.1.8", {});
            skEllipticalArc(sketch, "E40.9.1.9", {});
            skEllipticalArc(sketch, "E40.9.1.10", {});
            skEllipticalArc(sketch, "E40.9.1.11", {});
            skEllipticalArc(sketch, "E40.9.1.12", {});
            skEllipticalArc(sketch, "E40.9.1.13", {});
            skEllipticalArc(sketch, "E40.9.1.14", {});
            skEllipticalArc(sketch, "E40.9.2.0", {});
            skEllipticalArc(sketch, "E40.9.2.1", {});
            skEllipticalArc(sketch, "E40.9.2.2", {});
            skEllipticalArc(sketch, "E40.9.2.3", {});
            skEllipticalArc(sketch, "E40.9.2.4", {});
            skEllipticalArc(sketch, "E40.9.2.5", {});
            skEllipticalArc(sketch, "E40.9.2.6", {});
            skEllipticalArc(sketch, "E40.9.2.7", {});
            skEllipticalArc(sketch, "E40.9.2.8", {});
            skEllipticalArc(sketch, "E40.9.2.9", {});
            skEllipticalArc(sketch, "E40.9.2.10", {});
            skEllipticalArc(sketch, "E40.9.2.11", {});
            skEllipticalArc(sketch, "E40.9.2.12", {});
            skEllipticalArc(sketch, "E40.9.2.13", {});
            skEllipticalArc(sketch, "E40.9.2.14", {});
            skEllipticalArc(sketch, "E40.9.3.0", {});
            skEllipticalArc(sketch, "E40.9.3.1", {});
            skEllipticalArc(sketch, "E40.9.3.2", {});
            skEllipticalArc(sketch, "E40.9.3.3", {});
            skEllipticalArc(sketch, "E40.9.3.4", {});
            skEllipticalArc(sketch, "E40.9.3.5", {});
            skEllipticalArc(sketch, "E40.9.3.6", {});
            skEllipticalArc(sketch, "E40.9.3.7", {});
            skEllipticalArc(sketch, "E40.9.3.8", {});
            skEllipticalArc(sketch, "E40.9.3.9", {});
            skEllipticalArc(sketch, "E40.9.3.10", {});
            skEllipticalArc(sketch, "E40.9.3.11", {});
            skEllipticalArc(sketch, "E40.9.3.12", {});
            skEllipticalArc(sketch, "E40.9.3.13", {});
            skEllipticalArc(sketch, "E40.9.3.14", {});
            skLineSegment(sketch, "E40.direction1", {"start": v(-98.4, -2.07) * mm, "end": v(-76.15, -2.07) * mm, "construction": true});
            skLineSegment(sketch, "E40.direction2", {"start": v(-98.4, -2.07) * mm, "end": v(-98.4, 20.18) * mm, "construction": true});
            skLineSegment(sketch, "E41", {"start": v(-100, -76.68) * mm, "end": v(0, -64) * mm, "construction": true});
            skEllipticalArc(sketch, "E42", {});
            skEllipticalArc(sketch, "E43", {});
            skLineSegment(sketch, "E44", {"start": v(-96.84, -64.06) * mm, "end": v(-91.82, -78.03) * mm, "construction": true});
            skEllipticalArc(sketch, "E45.MirrorCS", {});
            skEllipticalArc(sketch, "E46.MirrorCS", {});
            skEllipticalArc(sketch, "E47.trimOffspring", {});
            skEllipticalArc(sketch, "E48.trimOffspring", {});
            skEllipticalArc(sketch, "E49.trimOffspring", {});
            skEllipticalArc(sketch, "E50.trimOffspring", {});
            skLineSegment(sketch, "E51", {"start": v(-50, -70.34) * mm, "end": v(-52.96, -46.95) * mm, "construction": true});
            skEllipticalArc(sketch, "E52.MirrorCS", {});
            skEllipticalArc(sketch, "E53.MirrorCS", {});
            skEllipticalArc(sketch, "E54.MirrorCS", {});
            skEllipticalArc(sketch, "E55.MirrorCS", {});
            skEllipticalArc(sketch, "E56.1.0.0", {});
            skEllipticalArc(sketch, "E56.1.0.1", {});
            skEllipticalArc(sketch, "E56.1.0.2", {});
            skEllipticalArc(sketch, "E56.1.0.3", {});
            skLineSegment(sketch, "E56.direction1", {"start": v(-91.78, -72.47) * mm, "end": v(-62.58, -68.55) * mm, "construction": true});
            skEllipticalArc(sketch, "E57.0.1.0", {});
            skEllipticalArc(sketch, "E57.0.1.1", {});
            skEllipticalArc(sketch, "E57.0.1.2", {});
            skEllipticalArc(sketch, "E57.0.1.3", {});
            skEllipticalArc(sketch, "E57.0.1.4", {});
            skEllipticalArc(sketch, "E57.0.1.5", {});
            skEllipticalArc(sketch, "E57.0.1.6", {});
            skEllipticalArc(sketch, "E57.0.1.7", {});
            skEllipticalArc(sketch, "E57.0.1.8", {});
            skEllipticalArc(sketch, "E57.0.1.9", {});
            skEllipticalArc(sketch, "E57.0.1.10", {});
            skEllipticalArc(sketch, "E57.0.1.11", {});
            skLineSegment(sketch, "E57.direction1", {"start": v(-9.01, -61.98) * mm, "end": v(15.99, -61.98) * mm, "construction": true});
            skLineSegment(sketch, "E57.direction2", {"start": v(-9.01, -61.98) * mm, "end": v(-14.82, -29.06) * mm, "construction": true});
            skEllipticalArc(sketch, "E58.MirrorCS", {});
            skEllipticalArc(sketch, "E59.MirrorCS", {});
            skEllipticalArc(sketch, "E60.MirrorCS", {});
            skEllipticalArc(sketch, "E61.MirrorCS", {});
            skEllipticalArc(sketch, "E62.MirrorCS", {});
            skEllipticalArc(sketch, "E63.MirrorCS", {});
            skEllipticalArc(sketch, "E64.MirrorCS", {});
            skEllipticalArc(sketch, "E65.MirrorCS", {});
            skEllipticalArc(sketch, "E66.MirrorCS", {});
            skEllipticalArc(sketch, "E67.MirrorCS", {});
            skEllipticalArc(sketch, "E68.MirrorCS", {});
            skEllipticalArc(sketch, "E69.MirrorCS", {});
            skEllipticalArc(sketch, "E70.MirrorCS", {});
            skEllipticalArc(sketch, "E71.MirrorCS", {});
            skEllipticalArc(sketch, "E72.MirrorCS", {});
            skEllipticalArc(sketch, "E73.MirrorCS", {});
            skEllipticalArc(sketch, "E74.MirrorCS", {});
            skEllipticalArc(sketch, "E75.MirrorCS", {});
            skEllipticalArc(sketch, "E76.MirrorCS", {});
            skEllipticalArc(sketch, "E77.MirrorCS", {});
            skEllipticalArc(sketch, "E78.MirrorCS", {});
            skEllipticalArc(sketch, "E79.MirrorCS", {});
            skLineSegment(sketch, "E80", {"start": v(-87.67, 25.63) * mm, "end": v(-87.67, -6.96) * mm, "construction": true});
            skFitSpline(sketch, "E81", {"points": [v(-87.67, 24.54) * mm, v(-83.85, 22.24) * mm, v(-81.65, 17.63) * mm, v(-77.98, 13.65) * mm, v(-76.3, 9.25) * mm, v(-78.2, 7.57) * mm, v(-81.55, 4.53) * mm, v(-83.75, -3.74) * mm, v(-87.67, -6.96) * mm], "startDerivative": vector(43.74, -13.23) * mm, "endDerivative": vector(-50.81, -5.65) * mm});
            skFitSpline(sketch, "E82.MirrorCS", {"points": [v(-87.67, 24.54) * mm, v(-91.48, 22.24) * mm, v(-93.68, 17.63) * mm, v(-97.35, 13.65) * mm, v(-99.02, 9.25) * mm, v(-97.14, 7.57) * mm, v(-93.79, 4.53) * mm, v(-91.59, -3.74) * mm, v(-87.67, -6.96) * mm], "startDerivative": vector(-43.74, -13.23) * mm, "endDerivative": vector(50.81, -5.65) * mm});
            const initialGuessF0  = {"E22": [-0.09796370088603243, 0, -0.741691698534492, -0.6707409517280276, 0.0012113596359206152, 0.0005476982455656242, 4.424159048994017, 1.0271249403401506], "E23.1.0": [-0.09813974819403327, 0.0008282374659133868, -0.40475415908808526, -0.9144255413651223, 0.0012113596359206152, 0.0005476982455656242, 4.4241590489939915, 1.0271249403401483], "E23.2.0": [-0.09863744993914286, 0.0015132651496692073, 0.002169051540750866, -0.99999764760494, 0.0012113596359206152, 0.0005476982455656242, 4.4241590489940075, 1.0271249403401341], "E24.1.3.0": [-0.09937074896815337, 0.0019366355414648928, 0.40871721345297557, -0.912661075880436, 0.0012113596359206152, 0.0005476982455656242, 1.8115872085407756, 3.8684587889580113], "E24.1.4.0": [-0.1002128512171363, 0.0020251440543597454, 0.7445944560798636, -0.6675171128706231, 0.0012113596359206152, 0.0005476982455656242, 1.811587208540798, 3.8684587889579776], "E24.1.5.0": [-0.10101814955698378, 0.0017634867623996658, 0.9517245528222696, -0.3069533768428862, 0.0012113596359206152, 0.0005476982455656242, 1.811587208540785, 3.868458788958013], "E24.1.6.0": [-0.10164740058883041, 0.0011969065884463656, 0.9942928282355765, 0.10668538662487148, 0.0012113596359206152, 0.0005476982455656242, 1.8115872085407754, 3.868458788958021], "E24.1.7.0": [-0.10199180109270375, 0.0004233703917957028, 0.8649388407801819, 0.5018772775388773, 0.001211359635920615, 0.000547698245565624, 1.8115872085407738, 3.8684587889580158], "E24.1.8.0": [-0.10199180109270375, -0.0004233703917957062, 0.5860290700312074, 0.8102900277544814, 0.0012113596359206152, 0.0005476982455656242, 1.8115872085407763, 3.868458788958045], "E24.1.9.0": [-0.10164740058883039, -0.0011969065884463587, 0.20578954916687192, 0.97859627091753, 0.0012113596359206152, 0.0005476982455656242, 1.8115872085407798, 3.868458788957996], "E24.1.10.0": [-0.10101814955698377, -0.001763486762399652, -0.2100328542877775, 0.9776943285709134, 0.0012113596359206152, 0.0005476982455656242, 4.4241590489939995, 1.027124940340158], "E24.1.11.0": [-0.1002128512171363, -0.0020251440543597593, -0.5895386691474909, 0.8077401547402515, 0.0012113596359206152, 0.0005476982455656242, 4.424159048994005, 1.0271249403401468], "E24.1.12.0": [-0.09937074896815336, -0.0019366355414648928, -0.8671078923209321, 0.4981203700660625, 0.0012113596359206152, 0.0005476982455656242, 4.42415904899401, 1.0271249403401517], "E24.1.13.0": [-0.09863744993914288, -0.0015132651496692073, -0.9947462834841825, 0.10237104812595471, 0.0012113596359206152, 0.0005476982455656242, 4.424159048994001, 1.0271249403401437], "E24.1.14.0": [-0.09813974819403326, -0.0008282374659133868, -0.9503840052467358, -0.31107915804690683, 0.0012113596359206152, 0.0005476982455656242, 4.424159048994019, 1.0271249403401463], "E25.trimOffspring": [-0.09937074896815337, 0.0019366355414648928, 0.40871721345297557, -0.912661075880436, 0.0012113596359206152, 0.0005476982455656242, 4.395511339103687, 1.0271249403401677], "E26.trimOffspring": [-0.09863744993914286, 0.0015132651496692073, 0.002169051540750866, -0.99999764760494, 0.0012113596359206152, 0.0005476982455656242, 1.811587208540777, 3.868458788958028], "E27.trimOffspring": [-0.09813974819403327, 0.0008282374659133868, -0.40475415908808526, -0.9144255413651223, 0.0012113596359206152, 0.0005476982455656242, 1.8115872085407903, 3.868458788958002], "E28.trimOffspring": [-0.09796370088603243, 0, -0.741691698534492, -0.6707409517280276, 0.0012113596359206152, 0.0005476982455656242, 1.8115872085407894, 3.8684587889580095], "E29.trimOffspring": [-0.1002128512171363, 0.0020251440543597454, 0.7445944560798636, -0.6675171128706231, 0.0012113596359206152, 0.0005476982455656242, 4.424159048993999, 1.0271249403401697], "E30.trimOffspring": [-0.10101814955698378, 0.0017634867623996658, 0.9517245528222696, -0.3069533768428862, 0.0012113596359206152, 0.0005476982455656242, 4.424159048994017, 1.0271249403401368], "E31.trimOffspring": [-0.10164740058883041, 0.0011969065884463656, 0.9942928282355765, 0.10668538662487148, 0.0012113596359206152, 0.0005476982455656242, 4.424159048994029, 1.0271249403401441], "E32.trimOffspring": [-0.10199180109270375, 0.0004233703917957028, 0.8649388407801819, 0.5018772775388773, 0.001211359635920615, 0.000547698245565624, 4.424159048994019, 1.0271249403401321], "E33.trimOffspring": [-0.10199180109270375, -0.0004233703917957062, 0.5860290700312074, 0.8102900277544814, 0.0012113596359206152, 0.0005476982455656242, 4.4241590489940155, 1.0271249403401317], "E34.trimOffspring": [-0.09813974819403326, -0.0008282374659133868, -0.9503840052467358, -0.31107915804690683, 0.0012113596359206152, 0.0005476982455656242, 1.8115872085407585, 3.868458788958019], "E35.trimOffspring": [-0.09863744993914288, -0.0015132651496692073, -0.9947462834841825, 0.10237104812595471, 0.0012113596359206152, 0.0005476982455656242, 1.8115872085408105, 3.868458788958024], "E36.trimOffspring": [-0.09937074896815336, -0.0019366355414648928, -0.8671078923209321, 0.4981203700660625, 0.0012113596359206152, 0.0005476982455656242, 1.8115872085407796, 3.8684587889579816], "E37.trimOffspring": [-0.1002128512171363, -0.0020251440543597593, -0.5895386691474909, 0.8077401547402515, 0.0012113596359206152, 0.0005476982455656242, 1.8115872085407858, 3.8684587889580238], "E38.trimOffspring": [-0.10101814955698377, -0.001763486762399652, -0.2100328542877775, 0.9776943285709134, 0.0012113596359206152, 0.0005476982455656242, 1.8115872085407818, 3.868458788958003], "E39.trimOffspring": [-0.10164740058883039, -0.0011969065884463587, 0.20578954916687192, 0.97859627091753, 0.0012113596359206152, 0.0005476982455656242, 4.42415904899399, 1.0271249403401728], "E40.0.1.0": [-0.09863744993914288, 0.02073673485033079, -0.9947462834841825, 0.10237104812595471, 0.0012113596359206152, 0.0005476982455656242, 1.8115872085408105, 3.8684587889580238], "E40.0.1.1": [-0.09813974819403326, 0.021421762534086612, -0.9503840052467358, -0.31107915804690683, 0.0012113596359206152, 0.0005476982455656242, 1.8115872085407578, 3.868458788958019], "E40.0.1.2": [-0.09796370088603243, 0.02225, -0.741691698534492, -0.6707409517280276, 0.0012113596359206152, 0.0005476982455656242, 1.8115872085407894, 3.86845878895801], "E40.0.1.3": [-0.09813974819403327, 0.023078237465913386, -0.40475415908808526, -0.9144255413651223, 0.0012113596359206152, 0.0005476982455656242, 1.8115872085407896, 3.868458788958003], "E40.0.1.4": [-0.09863744993914286, 0.023763265149669206, 0.002169051540750866, -0.99999764760494, 0.0012113596359206152, 0.0005476982455656242, 1.8115872085407771, 3.8684587889580273], "E40.0.1.5": [-0.09937074896815337, 0.024186635541464892, 0.40871721345297557, -0.912661075880436, 0.0012113596359206152, 0.0005476982455656242, 1.8115872085407752, 3.8684587889580118], "E40.0.1.6": [-0.1002128512171363, 0.024275144054359744, 0.7445944560798636, -0.6675171128706231, 0.0012113596359206152, 0.0005476982455656242, 1.8115872085407987, 3.868458788957976], "E40.0.1.7": [-0.10101814955698378, 0.024013486762399665, 0.9517245528222696, -0.3069533768428862, 0.0012113596359206152, 0.0005476982455656242, 1.8115872085407854, 3.8684587889580118], "E40.0.1.8": [-0.10164740058883041, 0.023446906588446365, 0.9942928282355765, 0.10668538662487148, 0.0012113596359206152, 0.0005476982455656242, 1.8115872085407754, 3.8684587889580206], "E40.0.1.9": [-0.10199180109270375, 0.022673370391795702, 0.8649388407801819, 0.5018772775388773, 0.001211359635920615, 0.000547698245565624, 1.8115872085407736, 3.8684587889580158], "E40.0.1.10": [-0.10199180109270375, 0.021826629608204293, 0.5860290700312074, 0.8102900277544814, 0.0012113596359206152, 0.0005476982455656242, 1.8115872085407756, 3.868458788958045], "E40.0.1.11": [-0.10164740058883039, 0.02105309341155364, 0.20578954916687192, 0.97859627091753, 0.0012113596359206152, 0.0005476982455656242, 1.811587208540781, 3.868458788957996], "E40.0.1.12": [-0.10101814955698377, 0.020486513237600347, -0.2100328542877775, 0.9776943285709134, 0.0012113596359206152, 0.0005476982455656242, 1.8115872085407831, 3.8684587889580038], "E40.0.1.13": [-0.1002128512171363, 0.02022485594564024, -0.5895386691474909, 0.8077401547402515, 0.0012113596359206152, 0.0005476982455656242, 1.8115872085407858, 3.868458788958025], "E40.0.1.14": [-0.09937074896815336, 0.020313364458535106, -0.8671078923209321, 0.4981203700660625, 0.0012113596359206152, 0.0005476982455656242, 1.81158720854078, 3.868458788957983], "E40.0.2.0": [-0.09863744993914288, 0.04298673485033079, -0.9947462834841825, 0.10237104812595471, 0.0012113596359206152, 0.0005476982455656242, 1.8115872085408105, 3.8684587889580255], "E40.0.2.1": [-0.09813974819403326, 0.04367176253408661, -0.9503840052467358, -0.31107915804690683, 0.0012113596359206152, 0.0005476982455656242, 1.8115872085407578, 3.868458788958019], "E40.0.2.2": [-0.09796370088603243, 0.0445, -0.741691698534492, -0.6707409517280276, 0.0012113596359206152, 0.0005476982455656242, 1.8115872085407914, 3.868458788958009], "E40.0.2.3": [-0.09813974819403327, 0.045328237465913385, -0.40475415908808526, -0.9144255413651223, 0.0012113596359206152, 0.0005476982455656242, 1.8115872085407922, 3.868458788958], "E40.0.2.4": [-0.09863744993914286, 0.046013265149669205, 0.002169051540750866, -0.99999764760494, 0.0012113596359206152, 0.0005476982455656242, 1.8115872085407771, 3.8684587889580273], "E40.0.2.5": [-0.09937074896815337, 0.04643663554146489, 0.40871721345297557, -0.912661075880436, 0.0012113596359206152, 0.0005476982455656242, 1.8115872085407778, 3.8684587889580118], "E40.0.2.6": [-0.1002128512171363, 0.04652514405435974, 0.7445944560798636, -0.6675171128706231, 0.0012113596359206152, 0.0005476982455656242, 1.8115872085407987, 3.868458788957976], "E40.0.2.7": [-0.10101814955698378, 0.046263486762399664, 0.9517245528222696, -0.3069533768428862, 0.0012113596359206152, 0.0005476982455656242, 1.8115872085407847, 3.8684587889580118], "E40.0.2.8": [-0.10164740058883041, 0.045696906588446363, 0.9942928282355765, 0.10668538662487148, 0.0012113596359206152, 0.0005476982455656242, 1.8115872085407754, 3.8684587889580224], "E40.0.2.9": [-0.10199180109270375, 0.0449233703917957, 0.8649388407801819, 0.5018772775388773, 0.001211359635920615, 0.000547698245565624, 1.8115872085407754, 3.8684587889580158], "E40.0.2.10": [-0.10199180109270375, 0.04407662960820429, 0.5860290700312074, 0.8102900277544814, 0.0012113596359206152, 0.0005476982455656242, 1.8115872085407756, 3.868458788958045], "E40.0.2.11": [-0.10164740058883039, 0.04330309341155364, 0.20578954916687192, 0.97859627091753, 0.0012113596359206152, 0.0005476982455656242, 1.811587208540781, 3.868458788957996], "E40.0.2.12": [-0.10101814955698377, 0.042736513237600346, -0.2100328542877775, 0.9776943285709134, 0.0012113596359206152, 0.0005476982455656242, 1.8115872085407831, 3.868458788958], "E40.0.2.13": [-0.1002128512171363, 0.04247485594564024, -0.5895386691474909, 0.8077401547402515, 0.0012113596359206152, 0.0005476982455656242, 1.8115872085407836, 3.868458788958025], "E40.0.2.14": [-0.09937074896815336, 0.042563364458535105, -0.8671078923209321, 0.4981203700660625, 0.0012113596359206152, 0.0005476982455656242, 1.811587208540779, 3.868458788957983], "E40.0.3.0": [-0.09863744993914288, 0.0652367348503308, -0.9947462834841825, 0.10237104812595471, 0.0012113596359206152, 0.0005476982455656242, 1.8115872085408105, 3.8684587889580255], "E40.0.3.1": [-0.09813974819403326, 0.06592176253408662, -0.9503840052467358, -0.31107915804690683, 0.0012113596359206152, 0.0005476982455656242, 1.8115872085407603, 3.8684587889580175], "E40.0.3.2": [-0.09796370088603243, 0.06675, -0.741691698534492, -0.6707409517280276, 0.0012113596359206152, 0.0005476982455656242, 1.8115872085407871, 3.868458788958009], "E40.0.3.3": [-0.09813974819403327, 0.06757823746591339, -0.40475415908808526, -0.9144255413651223, 0.0012113596359206152, 0.0005476982455656242, 1.8115872085407922, 3.868458788958005], "E40.0.3.4": [-0.09863744993914286, 0.06826326514966921, 0.002169051540750866, -0.99999764760494, 0.0012113596359206152, 0.0005476982455656242, 1.8115872085407712, 3.8684587889580273], "E40.0.3.5": [-0.09937074896815337, 0.0686866355414649, 0.40871721345297557, -0.912661075880436, 0.0012113596359206152, 0.0005476982455656242, 1.8115872085407727, 3.868458788958004], "E40.0.3.6": [-0.1002128512171363, 0.06877514405435975, 0.7445944560798636, -0.6675171128706231, 0.0012113596359206152, 0.0005476982455656242, 1.8115872085407987, 3.868458788957976], "E40.0.3.7": [-0.10101814955698378, 0.06851348676239967, 0.9517245528222696, -0.3069533768428862, 0.0012113596359206152, 0.0005476982455656242, 1.8115872085407858, 3.8684587889580118], "E40.0.3.8": [-0.10164740058883041, 0.06794690658844638, 0.9942928282355765, 0.10668538662487148, 0.0012113596359206152, 0.0005476982455656242, 1.8115872085407754, 3.8684587889580224], "E40.0.3.9": [-0.10199180109270375, 0.0671733703917957, 0.8649388407801819, 0.5018772775388773, 0.001211359635920615, 0.000547698245565624, 1.8115872085407754, 3.868458788958016], "E40.0.3.10": [-0.10199180109270375, 0.0663266296082043, 0.5860290700312074, 0.8102900277544814, 0.0012113596359206152, 0.0005476982455656242, 1.8115872085407807, 3.868458788958045], "E40.0.3.11": [-0.10164740058883039, 0.06555309341155365, 0.20578954916687192, 0.97859627091753, 0.0012113596359206152, 0.0005476982455656242, 1.8115872085407752, 3.868458788957996], "E40.0.3.12": [-0.10101814955698377, 0.06498651323760035, -0.2100328542877775, 0.9776943285709134, 0.0012113596359206152, 0.0005476982455656242, 1.8115872085407776, 3.8684587889580073], "E40.0.3.13": [-0.1002128512171363, 0.06472485594564024, -0.5895386691474909, 0.8077401547402515, 0.0012113596359206152, 0.0005476982455656242, 1.8115872085407836, 3.8684587889580175], "E40.0.3.14": [-0.09937074896815336, 0.06481336445853511, -0.8671078923209321, 0.4981203700660625, 0.0012113596359206152, 0.0005476982455656242, 1.8115872085407811, 3.868458788957983], "E40.1.0.0": [-0.07638744993914287, -0.0015132651496692073, -0.9947462834841825, 0.10237104812595471, 0.0012113596359206152, 0.0005476982455656242, 1.8115872085408105, 3.868458788958024], "E40.1.0.1": [-0.07588974819403325, -0.0008282374659133868, -0.9503840052467358, -0.31107915804690683, 0.0012113596359206152, 0.0005476982455656242, 1.8115872085407585, 3.868458788958019], "E40.1.0.2": [-0.07571370088603242, 0, -0.741691698534492, -0.6707409517280276, 0.0012113596359206152, 0.0005476982455656242, 1.8115872085407891, 3.8684587889580095], "E40.1.0.3": [-0.07588974819403327, 0.0008282374659133868, -0.40475415908808526, -0.9144255413651223, 0.0012113596359206152, 0.0005476982455656242, 1.8115872085407905, 3.868458788958002], "E40.1.0.4": [-0.07638744993914286, 0.0015132651496692073, 0.002169051540750866, -0.99999764760494, 0.0012113596359206152, 0.0005476982455656242, 1.8115872085407774, 3.8684587889580273], "E40.1.0.5": [-0.07712074896815337, 0.0019366355414648928, 0.40871721345297557, -0.912661075880436, 0.0012113596359206152, 0.0005476982455656242, 1.8115872085407752, 3.8684587889580113], "E40.1.0.6": [-0.0779628512171363, 0.0020251440543597454, 0.7445944560798636, -0.6675171128706231, 0.0012113596359206152, 0.0005476982455656242, 1.811587208540798, 3.8684587889579767], "E40.1.0.7": [-0.07876814955698377, 0.0017634867623996658, 0.9517245528222696, -0.3069533768428862, 0.0012113596359206152, 0.0005476982455656242, 1.811587208540785, 3.8684587889580127], "E40.1.0.8": [-0.07939740058883041, 0.0011969065884463656, 0.9942928282355765, 0.10668538662487148, 0.0012113596359206152, 0.0005476982455656242, 1.8115872085407754, 3.868458788958021], "E40.1.0.9": [-0.07974180109270375, 0.0004233703917957028, 0.8649388407801819, 0.5018772775388773, 0.001211359635920615, 0.000547698245565624, 1.8115872085407738, 3.8684587889580158], "E40.1.0.10": [-0.07974180109270375, -0.0004233703917957062, 0.5860290700312074, 0.8102900277544814, 0.0012113596359206152, 0.0005476982455656242, 1.811587208540776, 3.868458788958045], "E40.1.0.11": [-0.07939740058883038, -0.0011969065884463587, 0.20578954916687192, 0.97859627091753, 0.0012113596359206152, 0.0005476982455656242, 1.8115872085407798, 3.8684587889579958], "E40.1.0.12": [-0.07876814955698376, -0.001763486762399652, -0.2100328542877775, 0.9776943285709134, 0.0012113596359206152, 0.0005476982455656242, 1.8115872085407814, 3.868458788958003], "E40.1.0.13": [-0.0779628512171363, -0.0020251440543597593, -0.5895386691474909, 0.8077401547402515, 0.0012113596359206152, 0.0005476982455656242, 1.8115872085407858, 3.8684587889580233], "E40.1.0.14": [-0.07712074896815335, -0.0019366355414648928, -0.8671078923209321, 0.4981203700660625, 0.0012113596359206152, 0.0005476982455656242, 1.8115872085407796, 3.8684587889579802], "E40.1.1.0": [-0.07638744993914287, 0.02073673485033079, -0.9947462834841825, 0.10237104812595471, 0.0012113596359206152, 0.0005476982455656242, 1.8115872085408105, 3.8684587889580238], "E40.1.1.1": [-0.07588974819403325, 0.021421762534086612, -0.9503840052467358, -0.31107915804690683, 0.0012113596359206152, 0.0005476982455656242, 1.8115872085407578, 3.868458788958019], "E40.1.1.2": [-0.07571370088603242, 0.02225, -0.741691698534492, -0.6707409517280276, 0.0012113596359206152, 0.0005476982455656242, 1.8115872085407894, 3.86845878895801], "E40.1.1.3": [-0.07588974819403327, 0.023078237465913386, -0.40475415908808526, -0.9144255413651223, 0.0012113596359206152, 0.0005476982455656242, 1.8115872085407896, 3.868458788958003], "E40.1.1.4": [-0.07638744993914286, 0.023763265149669206, 0.002169051540750866, -0.99999764760494, 0.0012113596359206152, 0.0005476982455656242, 1.8115872085407771, 3.8684587889580273], "E40.1.1.5": [-0.07712074896815337, 0.024186635541464892, 0.40871721345297557, -0.912661075880436, 0.0012113596359206152, 0.0005476982455656242, 1.8115872085407752, 3.8684587889580118], "E40.1.1.6": [-0.0779628512171363, 0.024275144054359744, 0.7445944560798636, -0.6675171128706231, 0.0012113596359206152, 0.0005476982455656242, 1.8115872085407987, 3.868458788957976], "E40.1.1.7": [-0.07876814955698377, 0.024013486762399665, 0.9517245528222696, -0.3069533768428862, 0.0012113596359206152, 0.0005476982455656242, 1.8115872085407854, 3.8684587889580118], "E40.1.1.8": [-0.07939740058883041, 0.023446906588446365, 0.9942928282355765, 0.10668538662487148, 0.0012113596359206152, 0.0005476982455656242, 1.8115872085407754, 3.8684587889580206], "E40.1.1.9": [-0.07974180109270375, 0.022673370391795702, 0.8649388407801819, 0.5018772775388773, 0.001211359635920615, 0.000547698245565624, 1.8115872085407736, 3.8684587889580158], "E40.1.1.10": [-0.07974180109270375, 0.021826629608204293, 0.5860290700312074, 0.8102900277544814, 0.0012113596359206152, 0.0005476982455656242, 1.8115872085407756, 3.868458788958045], "E40.1.1.11": [-0.07939740058883038, 0.02105309341155364, 0.20578954916687192, 0.97859627091753, 0.0012113596359206152, 0.0005476982455656242, 1.811587208540781, 3.868458788957996], "E40.1.1.12": [-0.07876814955698376, 0.020486513237600347, -0.2100328542877775, 0.9776943285709134, 0.0012113596359206152, 0.0005476982455656242, 1.8115872085407831, 3.8684587889580038], "E40.1.1.13": [-0.0779628512171363, 0.02022485594564024, -0.5895386691474909, 0.8077401547402515, 0.0012113596359206152, 0.0005476982455656242, 1.8115872085407858, 3.868458788958025], "E40.1.1.14": [-0.07712074896815335, 0.020313364458535106, -0.8671078923209321, 0.4981203700660625, 0.0012113596359206152, 0.0005476982455656242, 1.81158720854078, 3.868458788957983], "E40.1.2.0": [-0.07638744993914287, 0.04298673485033079, -0.9947462834841825, 0.10237104812595471, 0.0012113596359206152, 0.0005476982455656242, 1.8115872085408105, 3.8684587889580255], "E40.1.2.1": [-0.07588974819403325, 0.04367176253408661, -0.9503840052467358, -0.31107915804690683, 0.0012113596359206152, 0.0005476982455656242, 1.8115872085407578, 3.868458788958019], "E40.1.2.2": [-0.07571370088603242, 0.0445, -0.741691698534492, -0.6707409517280276, 0.0012113596359206152, 0.0005476982455656242, 1.8115872085407914, 3.868458788958009], "E40.1.2.3": [-0.07588974819403327, 0.045328237465913385, -0.40475415908808526, -0.9144255413651223, 0.0012113596359206152, 0.0005476982455656242, 1.8115872085407922, 3.868458788958], "E40.1.2.4": [-0.07638744993914286, 0.046013265149669205, 0.002169051540750866, -0.99999764760494, 0.0012113596359206152, 0.0005476982455656242, 1.8115872085407771, 3.8684587889580273], "E40.1.2.5": [-0.07712074896815337, 0.04643663554146489, 0.40871721345297557, -0.912661075880436, 0.0012113596359206152, 0.0005476982455656242, 1.8115872085407778, 3.8684587889580118], "E40.1.2.6": [-0.0779628512171363, 0.04652514405435974, 0.7445944560798636, -0.6675171128706231, 0.0012113596359206152, 0.0005476982455656242, 1.8115872085407987, 3.868458788957976], "E40.1.2.7": [-0.07876814955698377, 0.046263486762399664, 0.9517245528222696, -0.3069533768428862, 0.0012113596359206152, 0.0005476982455656242, 1.8115872085407847, 3.8684587889580118], "E40.1.2.8": [-0.07939740058883041, 0.045696906588446363, 0.9942928282355765, 0.10668538662487148, 0.0012113596359206152, 0.0005476982455656242, 1.8115872085407754, 3.8684587889580224], "E40.1.2.9": [-0.07974180109270375, 0.0449233703917957, 0.8649388407801819, 0.5018772775388773, 0.001211359635920615, 0.000547698245565624, 1.8115872085407754, 3.8684587889580158], "E40.1.2.10": [-0.07974180109270375, 0.04407662960820429, 0.5860290700312074, 0.8102900277544814, 0.0012113596359206152, 0.0005476982455656242, 1.8115872085407756, 3.868458788958045], "E40.1.2.11": [-0.07939740058883038, 0.04330309341155364, 0.20578954916687192, 0.97859627091753, 0.0012113596359206152, 0.0005476982455656242, 1.811587208540781, 3.868458788957996], "E40.1.2.12": [-0.07876814955698376, 0.042736513237600346, -0.2100328542877775, 0.9776943285709134, 0.0012113596359206152, 0.0005476982455656242, 1.8115872085407831, 3.868458788958], "E40.1.2.13": [-0.0779628512171363, 0.04247485594564024, -0.5895386691474909, 0.8077401547402515, 0.0012113596359206152, 0.0005476982455656242, 1.8115872085407836, 3.868458788958025], "E40.1.2.14": [-0.07712074896815335, 0.042563364458535105, -0.8671078923209321, 0.4981203700660625, 0.0012113596359206152, 0.0005476982455656242, 1.811587208540779, 3.868458788957983], "E40.1.3.0": [-0.07638744993914287, 0.0652367348503308, -0.9947462834841825, 0.10237104812595471, 0.0012113596359206152, 0.0005476982455656242, 1.8115872085408105, 3.8684587889580255], "E40.1.3.1": [-0.07588974819403325, 0.06592176253408662, -0.9503840052467358, -0.31107915804690683, 0.0012113596359206152, 0.0005476982455656242, 1.8115872085407603, 3.8684587889580175], "E40.1.3.2": [-0.07571370088603242, 0.06675, -0.741691698534492, -0.6707409517280276, 0.0012113596359206152, 0.0005476982455656242, 1.8115872085407871, 3.868458788958009], "E40.1.3.3": [-0.07588974819403327, 0.06757823746591339, -0.40475415908808526, -0.9144255413651223, 0.0012113596359206152, 0.0005476982455656242, 1.8115872085407922, 3.868458788958005], "E40.1.3.4": [-0.07638744993914286, 0.06826326514966921, 0.002169051540750866, -0.99999764760494, 0.0012113596359206152, 0.0005476982455656242, 1.8115872085407712, 3.8684587889580273], "E40.1.3.5": [-0.07712074896815337, 0.0686866355414649, 0.40871721345297557, -0.912661075880436, 0.0012113596359206152, 0.0005476982455656242, 1.8115872085407727, 3.868458788958004], "E40.1.3.6": [-0.0779628512171363, 0.06877514405435975, 0.7445944560798636, -0.6675171128706231, 0.0012113596359206152, 0.0005476982455656242, 1.8115872085407987, 3.868458788957976], "E40.1.3.7": [-0.07876814955698377, 0.06851348676239967, 0.9517245528222696, -0.3069533768428862, 0.0012113596359206152, 0.0005476982455656242, 1.8115872085407858, 3.8684587889580118], "E40.1.3.8": [-0.07939740058883041, 0.06794690658844638, 0.9942928282355765, 0.10668538662487148, 0.0012113596359206152, 0.0005476982455656242, 1.8115872085407754, 3.8684587889580224], "E40.1.3.9": [-0.07974180109270375, 0.0671733703917957, 0.8649388407801819, 0.5018772775388773, 0.001211359635920615, 0.000547698245565624, 1.8115872085407754, 3.868458788958016], "E40.1.3.10": [-0.07974180109270375, 0.0663266296082043, 0.5860290700312074, 0.8102900277544814, 0.0012113596359206152, 0.0005476982455656242, 1.8115872085407807, 3.868458788958045], "E40.1.3.11": [-0.07939740058883038, 0.06555309341155365, 0.20578954916687192, 0.97859627091753, 0.0012113596359206152, 0.0005476982455656242, 1.8115872085407752, 3.868458788957996], "E40.1.3.12": [-0.07876814955698376, 0.06498651323760035, -0.2100328542877775, 0.9776943285709134, 0.0012113596359206152, 0.0005476982455656242, 1.8115872085407776, 3.8684587889580073], "E40.1.3.13": [-0.0779628512171363, 0.06472485594564024, -0.5895386691474909, 0.8077401547402515, 0.0012113596359206152, 0.0005476982455656242, 1.8115872085407836, 3.8684587889580175], "E40.1.3.14": [-0.07712074896815335, 0.06481336445853511, -0.8671078923209321, 0.4981203700660625, 0.0012113596359206152, 0.0005476982455656242, 1.8115872085407811, 3.868458788957983], "E40.2.0.0": [-0.054137449939142865, -0.0015132651496692073, -0.9947462834841825, 0.10237104812595471, 0.0012113596359206152, 0.0005476982455656242, 1.8115872085408105, 3.868458788958024], "E40.2.0.1": [-0.05363974819403325, -0.0008282374659133868, -0.9503840052467358, -0.31107915804690683, 0.0012113596359206152, 0.0005476982455656242, 1.8115872085407585, 3.868458788958019], "E40.2.0.2": [-0.05346370088603242, 0, -0.741691698534492, -0.6707409517280276, 0.0012113596359206152, 0.0005476982455656242, 1.8115872085407891, 3.8684587889580095], "E40.2.0.3": [-0.05363974819403326, 0.0008282374659133868, -0.40475415908808526, -0.9144255413651223, 0.0012113596359206152, 0.0005476982455656242, 1.8115872085407905, 3.868458788958002], "E40.2.0.4": [-0.05413744993914285, 0.0015132651496692073, 0.002169051540750866, -0.99999764760494, 0.0012113596359206152, 0.0005476982455656242, 1.8115872085407763, 3.8684587889580273], "E40.2.0.5": [-0.05487074896815336, 0.0019366355414648928, 0.40871721345297557, -0.912661075880436, 0.0012113596359206152, 0.0005476982455656242, 1.8115872085407752, 3.8684587889580113], "E40.2.0.6": [-0.05571285121713629, 0.0020251440543597454, 0.7445944560798636, -0.6675171128706231, 0.0012113596359206152, 0.0005476982455656242, 1.811587208540798, 3.8684587889579767], "E40.2.0.7": [-0.05651814955698377, 0.0017634867623996658, 0.9517245528222696, -0.3069533768428862, 0.0012113596359206152, 0.0005476982455656242, 1.811587208540785, 3.8684587889580127], "E40.2.0.8": [-0.0571474005888304, 0.0011969065884463656, 0.9942928282355765, 0.10668538662487148, 0.0012113596359206152, 0.0005476982455656242, 1.8115872085407754, 3.868458788958021], "E40.2.0.9": [-0.05749180109270374, 0.0004233703917957028, 0.8649388407801819, 0.5018772775388773, 0.001211359635920615, 0.000547698245565624, 1.8115872085407738, 3.8684587889580158], "E40.2.0.10": [-0.05749180109270374, -0.0004233703917957062, 0.5860290700312074, 0.8102900277544814, 0.0012113596359206152, 0.0005476982455656242, 1.811587208540776, 3.868458788958045], "E40.2.0.11": [-0.057147400588830374, -0.0011969065884463587, 0.20578954916687192, 0.97859627091753, 0.0012113596359206152, 0.0005476982455656242, 1.8115872085407798, 3.8684587889579958], "E40.2.0.12": [-0.056518149556983754, -0.001763486762399652, -0.2100328542877775, 0.9776943285709134, 0.0012113596359206152, 0.0005476982455656242, 1.8115872085407814, 3.868458788958003], "E40.2.0.13": [-0.05571285121713629, -0.0020251440543597593, -0.5895386691474909, 0.8077401547402515, 0.0012113596359206152, 0.0005476982455656242, 1.8115872085407858, 3.8684587889580233], "E40.2.0.14": [-0.054870748968153346, -0.0019366355414648928, -0.8671078923209321, 0.4981203700660625, 0.0012113596359206152, 0.0005476982455656242, 1.8115872085407796, 3.8684587889579802], "E40.2.1.0": [-0.054137449939142865, 0.02073673485033079, -0.9947462834841825, 0.10237104812595471, 0.0012113596359206152, 0.0005476982455656242, 1.8115872085408105, 3.8684587889580238], "E40.2.1.1": [-0.05363974819403325, 0.021421762534086612, -0.9503840052467358, -0.31107915804690683, 0.0012113596359206152, 0.0005476982455656242, 1.8115872085407578, 3.868458788958019], "E40.2.1.2": [-0.05346370088603242, 0.02225, -0.741691698534492, -0.6707409517280276, 0.0012113596359206152, 0.0005476982455656242, 1.8115872085407894, 3.86845878895801], "E40.2.1.3": [-0.05363974819403326, 0.023078237465913386, -0.40475415908808526, -0.9144255413651223, 0.0012113596359206152, 0.0005476982455656242, 1.8115872085407896, 3.868458788958003], "E40.2.1.4": [-0.05413744993914285, 0.023763265149669206, 0.002169051540750866, -0.99999764760494, 0.0012113596359206152, 0.0005476982455656242, 1.8115872085407763, 3.8684587889580273], "E40.2.1.5": [-0.05487074896815336, 0.024186635541464892, 0.40871721345297557, -0.912661075880436, 0.0012113596359206152, 0.0005476982455656242, 1.8115872085407752, 3.8684587889580118], "E40.2.1.6": [-0.05571285121713629, 0.024275144054359744, 0.7445944560798636, -0.6675171128706231, 0.0012113596359206152, 0.0005476982455656242, 1.8115872085407987, 3.868458788957976], "E40.2.1.7": [-0.05651814955698377, 0.024013486762399665, 0.9517245528222696, -0.3069533768428862, 0.0012113596359206152, 0.0005476982455656242, 1.8115872085407854, 3.8684587889580118], "E40.2.1.8": [-0.0571474005888304, 0.023446906588446365, 0.9942928282355765, 0.10668538662487148, 0.0012113596359206152, 0.0005476982455656242, 1.8115872085407754, 3.8684587889580206], "E40.2.1.9": [-0.05749180109270374, 0.022673370391795702, 0.8649388407801819, 0.5018772775388773, 0.001211359635920615, 0.000547698245565624, 1.8115872085407736, 3.8684587889580158], "E40.2.1.10": [-0.05749180109270374, 0.021826629608204293, 0.5860290700312074, 0.8102900277544814, 0.0012113596359206152, 0.0005476982455656242, 1.8115872085407756, 3.868458788958045], "E40.2.1.11": [-0.057147400588830374, 0.02105309341155364, 0.20578954916687192, 0.97859627091753, 0.0012113596359206152, 0.0005476982455656242, 1.811587208540781, 3.868458788957996], "E40.2.1.12": [-0.056518149556983754, 0.020486513237600347, -0.2100328542877775, 0.9776943285709134, 0.0012113596359206152, 0.0005476982455656242, 1.8115872085407831, 3.8684587889580038], "E40.2.1.13": [-0.05571285121713629, 0.02022485594564024, -0.5895386691474909, 0.8077401547402515, 0.0012113596359206152, 0.0005476982455656242, 1.8115872085407858, 3.868458788958025], "E40.2.1.14": [-0.054870748968153346, 0.020313364458535106, -0.8671078923209321, 0.4981203700660625, 0.0012113596359206152, 0.0005476982455656242, 1.81158720854078, 3.868458788957983], "E40.2.2.0": [-0.054137449939142865, 0.04298673485033079, -0.9947462834841825, 0.10237104812595471, 0.0012113596359206152, 0.0005476982455656242, 1.8115872085408105, 3.8684587889580255], "E40.2.2.1": [-0.05363974819403325, 0.04367176253408661, -0.9503840052467358, -0.31107915804690683, 0.0012113596359206152, 0.0005476982455656242, 1.8115872085407578, 3.868458788958019], "E40.2.2.2": [-0.05346370088603242, 0.0445, -0.741691698534492, -0.6707409517280276, 0.0012113596359206152, 0.0005476982455656242, 1.8115872085407914, 3.868458788958009], "E40.2.2.3": [-0.05363974819403326, 0.045328237465913385, -0.40475415908808526, -0.9144255413651223, 0.0012113596359206152, 0.0005476982455656242, 1.8115872085407922, 3.868458788958], "E40.2.2.4": [-0.05413744993914285, 0.046013265149669205, 0.002169051540750866, -0.99999764760494, 0.0012113596359206152, 0.0005476982455656242, 1.8115872085407763, 3.8684587889580273], "E40.2.2.5": [-0.05487074896815336, 0.04643663554146489, 0.40871721345297557, -0.912661075880436, 0.0012113596359206152, 0.0005476982455656242, 1.8115872085407778, 3.8684587889580118], "E40.2.2.6": [-0.05571285121713629, 0.04652514405435974, 0.7445944560798636, -0.6675171128706231, 0.0012113596359206152, 0.0005476982455656242, 1.8115872085407987, 3.868458788957976], "E40.2.2.7": [-0.05651814955698377, 0.046263486762399664, 0.9517245528222696, -0.3069533768428862, 0.0012113596359206152, 0.0005476982455656242, 1.8115872085407847, 3.8684587889580118], "E40.2.2.8": [-0.0571474005888304, 0.045696906588446363, 0.9942928282355765, 0.10668538662487148, 0.0012113596359206152, 0.0005476982455656242, 1.8115872085407754, 3.8684587889580224], "E40.2.2.9": [-0.05749180109270374, 0.0449233703917957, 0.8649388407801819, 0.5018772775388773, 0.001211359635920615, 0.000547698245565624, 1.8115872085407754, 3.8684587889580158], "E40.2.2.10": [-0.05749180109270374, 0.04407662960820429, 0.5860290700312074, 0.8102900277544814, 0.0012113596359206152, 0.0005476982455656242, 1.8115872085407756, 3.868458788958045], "E40.2.2.11": [-0.057147400588830374, 0.04330309341155364, 0.20578954916687192, 0.97859627091753, 0.0012113596359206152, 0.0005476982455656242, 1.811587208540781, 3.868458788957996], "E40.2.2.12": [-0.056518149556983754, 0.042736513237600346, -0.2100328542877775, 0.9776943285709134, 0.0012113596359206152, 0.0005476982455656242, 1.8115872085407831, 3.868458788958], "E40.2.2.13": [-0.05571285121713629, 0.04247485594564024, -0.5895386691474909, 0.8077401547402515, 0.0012113596359206152, 0.0005476982455656242, 1.8115872085407836, 3.868458788958025], "E40.2.2.14": [-0.054870748968153346, 0.042563364458535105, -0.8671078923209321, 0.4981203700660625, 0.0012113596359206152, 0.0005476982455656242, 1.811587208540779, 3.868458788957983], "E40.2.3.0": [-0.054137449939142865, 0.0652367348503308, -0.9947462834841825, 0.10237104812595471, 0.0012113596359206152, 0.0005476982455656242, 1.8115872085408105, 3.8684587889580255], "E40.2.3.1": [-0.05363974819403325, 0.06592176253408662, -0.9503840052467358, -0.31107915804690683, 0.0012113596359206152, 0.0005476982455656242, 1.8115872085407603, 3.8684587889580175], "E40.2.3.2": [-0.05346370088603242, 0.06675, -0.741691698534492, -0.6707409517280276, 0.0012113596359206152, 0.0005476982455656242, 1.8115872085407871, 3.868458788958009], "E40.2.3.3": [-0.05363974819403326, 0.06757823746591339, -0.40475415908808526, -0.9144255413651223, 0.0012113596359206152, 0.0005476982455656242, 1.8115872085407922, 3.868458788958005], "E40.2.3.4": [-0.05413744993914285, 0.06826326514966921, 0.002169051540750866, -0.99999764760494, 0.0012113596359206152, 0.0005476982455656242, 1.8115872085407705, 3.8684587889580273], "E40.2.3.5": [-0.05487074896815336, 0.0686866355414649, 0.40871721345297557, -0.912661075880436, 0.0012113596359206152, 0.0005476982455656242, 1.8115872085407727, 3.868458788958004], "E40.2.3.6": [-0.05571285121713629, 0.06877514405435975, 0.7445944560798636, -0.6675171128706231, 0.0012113596359206152, 0.0005476982455656242, 1.8115872085407987, 3.868458788957976], "E40.2.3.7": [-0.05651814955698377, 0.06851348676239967, 0.9517245528222696, -0.3069533768428862, 0.0012113596359206152, 0.0005476982455656242, 1.8115872085407858, 3.8684587889580118], "E40.2.3.8": [-0.0571474005888304, 0.06794690658844638, 0.9942928282355765, 0.10668538662487148, 0.0012113596359206152, 0.0005476982455656242, 1.8115872085407754, 3.8684587889580224], "E40.2.3.9": [-0.05749180109270374, 0.0671733703917957, 0.8649388407801819, 0.5018772775388773, 0.001211359635920615, 0.000547698245565624, 1.8115872085407754, 3.868458788958016], "E40.2.3.10": [-0.05749180109270374, 0.0663266296082043, 0.5860290700312074, 0.8102900277544814, 0.0012113596359206152, 0.0005476982455656242, 1.8115872085407807, 3.868458788958045], "E40.2.3.11": [-0.057147400588830374, 0.06555309341155365, 0.20578954916687192, 0.97859627091753, 0.0012113596359206152, 0.0005476982455656242, 1.8115872085407752, 3.868458788957996], "E40.2.3.12": [-0.056518149556983754, 0.06498651323760035, -0.2100328542877775, 0.9776943285709134, 0.0012113596359206152, 0.0005476982455656242, 1.8115872085407776, 3.8684587889580073], "E40.2.3.13": [-0.05571285121713629, 0.06472485594564024, -0.5895386691474909, 0.8077401547402515, 0.0012113596359206152, 0.0005476982455656242, 1.8115872085407836, 3.8684587889580175], "E40.2.3.14": [-0.054870748968153346, 0.06481336445853511, -0.8671078923209321, 0.4981203700660625, 0.0012113596359206152, 0.0005476982455656242, 1.8115872085407811, 3.868458788957983], "E40.3.0.0": [-0.03188744993914286, -0.0015132651496692073, -0.9947462834841825, 0.10237104812595471, 0.0012113596359206152, 0.0005476982455656242, 1.8115872085408105, 3.868458788958024], "E40.3.0.1": [-0.03138974819403324, -0.0008282374659133868, -0.9503840052467358, -0.31107915804690683, 0.0012113596359206152, 0.0005476982455656242, 1.8115872085407585, 3.868458788958019], "E40.3.0.2": [-0.03121370088603241, 0, -0.741691698534492, -0.6707409517280276, 0.0012113596359206152, 0.0005476982455656242, 1.8115872085407891, 3.8684587889580095], "E40.3.0.3": [-0.03138974819403326, 0.0008282374659133868, -0.40475415908808526, -0.9144255413651223, 0.0012113596359206152, 0.0005476982455656242, 1.8115872085407905, 3.868458788958002], "E40.3.0.4": [-0.031887449939142845, 0.0015132651496692073, 0.002169051540750866, -0.99999764760494, 0.0012113596359206152, 0.0005476982455656242, 1.8115872085407763, 3.8684587889580273], "E40.3.0.5": [-0.032620748968153354, 0.0019366355414648928, 0.40871721345297557, -0.912661075880436, 0.0012113596359206152, 0.0005476982455656242, 1.8115872085407752, 3.8684587889580113], "E40.3.0.6": [-0.03346285121713628, 0.0020251440543597454, 0.7445944560798636, -0.6675171128706231, 0.0012113596359206152, 0.0005476982455656242, 1.811587208540798, 3.8684587889579767], "E40.3.0.7": [-0.03426814955698376, 0.0017634867623996658, 0.9517245528222696, -0.3069533768428862, 0.0012113596359206152, 0.0005476982455656242, 1.811587208540785, 3.8684587889580127], "E40.3.0.8": [-0.034897400588830396, 0.0011969065884463656, 0.9942928282355765, 0.10668538662487148, 0.0012113596359206152, 0.0005476982455656242, 1.8115872085407754, 3.868458788958021], "E40.3.0.9": [-0.03524180109270374, 0.0004233703917957028, 0.8649388407801819, 0.5018772775388773, 0.001211359635920615, 0.000547698245565624, 1.8115872085407738, 3.8684587889580158], "E40.3.0.10": [-0.03524180109270374, -0.0004233703917957062, 0.5860290700312074, 0.8102900277544814, 0.0012113596359206152, 0.0005476982455656242, 1.811587208540776, 3.868458788958045], "E40.3.0.11": [-0.03489740058883037, -0.0011969065884463587, 0.20578954916687192, 0.97859627091753, 0.0012113596359206152, 0.0005476982455656242, 1.8115872085407798, 3.8684587889579958], "E40.3.0.12": [-0.03426814955698375, -0.001763486762399652, -0.2100328542877775, 0.9776943285709134, 0.0012113596359206152, 0.0005476982455656242, 1.8115872085407814, 3.868458788958003], "E40.3.0.13": [-0.03346285121713628, -0.0020251440543597593, -0.5895386691474909, 0.8077401547402515, 0.0012113596359206152, 0.0005476982455656242, 1.8115872085407858, 3.8684587889580233], "E40.3.0.14": [-0.03262074896815334, -0.0019366355414648928, -0.8671078923209321, 0.4981203700660625, 0.0012113596359206152, 0.0005476982455656242, 1.8115872085407796, 3.8684587889579802], "E40.3.1.0": [-0.03188744993914286, 0.02073673485033079, -0.9947462834841825, 0.10237104812595471, 0.0012113596359206152, 0.0005476982455656242, 1.8115872085408105, 3.8684587889580238], "E40.3.1.1": [-0.03138974819403324, 0.021421762534086612, -0.9503840052467358, -0.31107915804690683, 0.0012113596359206152, 0.0005476982455656242, 1.8115872085407578, 3.868458788958019], "E40.3.1.2": [-0.03121370088603241, 0.02225, -0.741691698534492, -0.6707409517280276, 0.0012113596359206152, 0.0005476982455656242, 1.8115872085407894, 3.86845878895801], "E40.3.1.3": [-0.03138974819403326, 0.023078237465913386, -0.40475415908808526, -0.9144255413651223, 0.0012113596359206152, 0.0005476982455656242, 1.8115872085407896, 3.868458788958003], "E40.3.1.4": [-0.031887449939142845, 0.023763265149669206, 0.002169051540750866, -0.99999764760494, 0.0012113596359206152, 0.0005476982455656242, 1.8115872085407763, 3.8684587889580273], "E40.3.1.5": [-0.032620748968153354, 0.024186635541464892, 0.40871721345297557, -0.912661075880436, 0.0012113596359206152, 0.0005476982455656242, 1.8115872085407752, 3.8684587889580118], "E40.3.1.6": [-0.03346285121713628, 0.024275144054359744, 0.7445944560798636, -0.6675171128706231, 0.0012113596359206152, 0.0005476982455656242, 1.8115872085407987, 3.868458788957976], "E40.3.1.7": [-0.03426814955698376, 0.024013486762399665, 0.9517245528222696, -0.3069533768428862, 0.0012113596359206152, 0.0005476982455656242, 1.8115872085407854, 3.8684587889580118], "E40.3.1.8": [-0.034897400588830396, 0.023446906588446365, 0.9942928282355765, 0.10668538662487148, 0.0012113596359206152, 0.0005476982455656242, 1.8115872085407754, 3.8684587889580206], "E40.3.1.9": [-0.03524180109270374, 0.022673370391795702, 0.8649388407801819, 0.5018772775388773, 0.001211359635920615, 0.000547698245565624, 1.8115872085407736, 3.8684587889580158], "E40.3.1.10": [-0.03524180109270374, 0.021826629608204293, 0.5860290700312074, 0.8102900277544814, 0.0012113596359206152, 0.0005476982455656242, 1.8115872085407756, 3.868458788958045], "E40.3.1.11": [-0.03489740058883037, 0.02105309341155364, 0.20578954916687192, 0.97859627091753, 0.0012113596359206152, 0.0005476982455656242, 1.811587208540781, 3.868458788957996], "E40.3.1.12": [-0.03426814955698375, 0.020486513237600347, -0.2100328542877775, 0.9776943285709134, 0.0012113596359206152, 0.0005476982455656242, 1.8115872085407831, 3.8684587889580038], "E40.3.1.13": [-0.03346285121713628, 0.02022485594564024, -0.5895386691474909, 0.8077401547402515, 0.0012113596359206152, 0.0005476982455656242, 1.8115872085407858, 3.868458788958025], "E40.3.1.14": [-0.03262074896815334, 0.020313364458535106, -0.8671078923209321, 0.4981203700660625, 0.0012113596359206152, 0.0005476982455656242, 1.81158720854078, 3.868458788957983], "E40.3.2.0": [-0.03188744993914286, 0.04298673485033079, -0.9947462834841825, 0.10237104812595471, 0.0012113596359206152, 0.0005476982455656242, 1.8115872085408105, 3.8684587889580255], "E40.3.2.1": [-0.03138974819403324, 0.04367176253408661, -0.9503840052467358, -0.31107915804690683, 0.0012113596359206152, 0.0005476982455656242, 1.8115872085407578, 3.868458788958019], "E40.3.2.2": [-0.03121370088603241, 0.0445, -0.741691698534492, -0.6707409517280276, 0.0012113596359206152, 0.0005476982455656242, 1.8115872085407934, 3.868458788958009], "E40.3.2.3": [-0.03138974819403326, 0.045328237465913385, -0.40475415908808526, -0.9144255413651223, 0.0012113596359206152, 0.0005476982455656242, 1.8115872085407922, 3.868458788958], "E40.3.2.4": [-0.031887449939142845, 0.046013265149669205, 0.002169051540750866, -0.99999764760494, 0.0012113596359206152, 0.0005476982455656242, 1.8115872085407763, 3.8684587889580273], "E40.3.2.5": [-0.032620748968153354, 0.04643663554146489, 0.40871721345297557, -0.912661075880436, 0.0012113596359206152, 0.0005476982455656242, 1.8115872085407778, 3.8684587889580118], "E40.3.2.6": [-0.03346285121713628, 0.04652514405435974, 0.7445944560798636, -0.6675171128706231, 0.0012113596359206152, 0.0005476982455656242, 1.8115872085407987, 3.868458788957976], "E40.3.2.7": [-0.03426814955698376, 0.046263486762399664, 0.9517245528222696, -0.3069533768428862, 0.0012113596359206152, 0.0005476982455656242, 1.8115872085407847, 3.8684587889580118], "E40.3.2.8": [-0.034897400588830396, 0.045696906588446363, 0.9942928282355765, 0.10668538662487148, 0.0012113596359206152, 0.0005476982455656242, 1.8115872085407754, 3.8684587889580224], "E40.3.2.9": [-0.03524180109270374, 0.0449233703917957, 0.8649388407801819, 0.5018772775388773, 0.001211359635920615, 0.000547698245565624, 1.8115872085407754, 3.8684587889580158], "E40.3.2.10": [-0.03524180109270374, 0.04407662960820429, 0.5860290700312074, 0.8102900277544814, 0.0012113596359206152, 0.0005476982455656242, 1.8115872085407756, 3.868458788958045], "E40.3.2.11": [-0.03489740058883037, 0.04330309341155364, 0.20578954916687192, 0.97859627091753, 0.0012113596359206152, 0.0005476982455656242, 1.811587208540781, 3.868458788957996], "E40.3.2.12": [-0.03426814955698375, 0.042736513237600346, -0.2100328542877775, 0.9776943285709134, 0.0012113596359206152, 0.0005476982455656242, 1.8115872085407831, 3.868458788958], "E40.3.2.13": [-0.03346285121713628, 0.04247485594564024, -0.5895386691474909, 0.8077401547402515, 0.0012113596359206152, 0.0005476982455656242, 1.8115872085407836, 3.868458788958025], "E40.3.2.14": [-0.03262074896815334, 0.042563364458535105, -0.8671078923209321, 0.4981203700660625, 0.0012113596359206152, 0.0005476982455656242, 1.811587208540779, 3.868458788957983], "E40.3.3.0": [-0.03188744993914286, 0.0652367348503308, -0.9947462834841825, 0.10237104812595471, 0.0012113596359206152, 0.0005476982455656242, 1.8115872085408105, 3.8684587889580255], "E40.3.3.1": [-0.03138974819403324, 0.06592176253408662, -0.9503840052467358, -0.31107915804690683, 0.0012113596359206152, 0.0005476982455656242, 1.811587208540763, 3.8684587889580175], "E40.3.3.2": [-0.03121370088603241, 0.06675, -0.741691698534492, -0.6707409517280276, 0.0012113596359206152, 0.0005476982455656242, 1.8115872085407871, 3.868458788958009], "E40.3.3.3": [-0.03138974819403326, 0.06757823746591339, -0.40475415908808526, -0.9144255413651223, 0.0012113596359206152, 0.0005476982455656242, 1.8115872085407922, 3.868458788958005], "E40.3.3.4": [-0.031887449939142845, 0.06826326514966921, 0.002169051540750866, -0.99999764760494, 0.0012113596359206152, 0.0005476982455656242, 1.8115872085407705, 3.8684587889580273], "E40.3.3.5": [-0.032620748968153354, 0.0686866355414649, 0.40871721345297557, -0.912661075880436, 0.0012113596359206152, 0.0005476982455656242, 1.8115872085407727, 3.868458788958004], "E40.3.3.6": [-0.03346285121713628, 0.06877514405435975, 0.7445944560798636, -0.6675171128706231, 0.0012113596359206152, 0.0005476982455656242, 1.8115872085407987, 3.868458788957976], "E40.3.3.7": [-0.03426814955698376, 0.06851348676239967, 0.9517245528222696, -0.3069533768428862, 0.0012113596359206152, 0.0005476982455656242, 1.8115872085407858, 3.8684587889580118], "E40.3.3.8": [-0.034897400588830396, 0.06794690658844638, 0.9942928282355765, 0.10668538662487148, 0.0012113596359206152, 0.0005476982455656242, 1.8115872085407754, 3.8684587889580224], "E40.3.3.9": [-0.03524180109270374, 0.0671733703917957, 0.8649388407801819, 0.5018772775388773, 0.001211359635920615, 0.000547698245565624, 1.8115872085407754, 3.868458788958016], "E40.3.3.10": [-0.03524180109270374, 0.0663266296082043, 0.5860290700312074, 0.8102900277544814, 0.0012113596359206152, 0.0005476982455656242, 1.8115872085407807, 3.868458788958045], "E40.3.3.11": [-0.03489740058883037, 0.06555309341155365, 0.20578954916687192, 0.97859627091753, 0.0012113596359206152, 0.0005476982455656242, 1.8115872085407752, 3.868458788957996], "E40.3.3.12": [-0.03426814955698375, 0.06498651323760035, -0.2100328542877775, 0.9776943285709134, 0.0012113596359206152, 0.0005476982455656242, 1.8115872085407776, 3.8684587889580073], "E40.3.3.13": [-0.03346285121713628, 0.06472485594564024, -0.5895386691474909, 0.8077401547402515, 0.0012113596359206152, 0.0005476982455656242, 1.8115872085407836, 3.8684587889580175], "E40.3.3.14": [-0.03262074896815334, 0.06481336445853511, -0.8671078923209321, 0.4981203700660625, 0.0012113596359206152, 0.0005476982455656242, 1.8115872085407811, 3.868458788957983], "E40.4.0.0": [-0.009637449939142853, -0.0015132651496692073, -0.9947462834841825, 0.10237104812595471, 0.0012113596359206152, 0.0005476982455656242, 1.8115872085408105, 3.868458788958024], "E40.4.0.1": [-0.009139748194033237, -0.0008282374659133868, -0.9503840052467358, -0.31107915804690683, 0.0012113596359206152, 0.0005476982455656242, 1.8115872085407585, 3.868458788958019], "E40.4.0.2": [-0.008963700886032405, 0, -0.741691698534492, -0.6707409517280276, 0.0012113596359206152, 0.0005476982455656242, 1.8115872085407891, 3.8684587889580095], "E40.4.0.3": [-0.009139748194033251, 0.0008282374659133868, -0.40475415908808526, -0.9144255413651223, 0.0012113596359206152, 0.0005476982455656242, 1.8115872085407896, 3.868458788958002], "E40.4.0.4": [-0.00963744993914284, 0.0015132651496692073, 0.002169051540750866, -0.99999764760494, 0.0012113596359206152, 0.0005476982455656242, 1.8115872085407763, 3.868458788958029], "E40.4.0.5": [-0.010370748968153348, 0.0019366355414648928, 0.40871721345297557, -0.912661075880436, 0.0012113596359206152, 0.0005476982455656242, 1.8115872085407752, 3.8684587889580104], "E40.4.0.6": [-0.011212851217136277, 0.0020251440543597454, 0.7445944560798636, -0.6675171128706231, 0.0012113596359206152, 0.0005476982455656242, 1.811587208540798, 3.8684587889579785], "E40.4.0.7": [-0.012018149556983757, 0.0017634867623996658, 0.9517245528222696, -0.3069533768428862, 0.0012113596359206152, 0.0005476982455656242, 1.811587208540785, 3.8684587889580127], "E40.4.0.8": [-0.01264740058883039, 0.0011969065884463656, 0.9942928282355765, 0.10668538662487148, 0.0012113596359206152, 0.0005476982455656242, 1.8115872085407754, 3.868458788958021], "E40.4.0.9": [-0.01299180109270373, 0.0004233703917957028, 0.8649388407801819, 0.5018772775388773, 0.001211359635920615, 0.000547698245565624, 1.8115872085407738, 3.8684587889580158], "E40.4.0.10": [-0.01299180109270373, -0.0004233703917957062, 0.5860290700312074, 0.8102900277544814, 0.0012113596359206152, 0.0005476982455656242, 1.811587208540776, 3.868458788958045], "E40.4.0.11": [-0.012647400588830363, -0.0011969065884463587, 0.20578954916687192, 0.97859627091753, 0.0012113596359206152, 0.0005476982455656242, 1.8115872085407798, 3.8684587889579976], "E40.4.0.12": [-0.012018149556983743, -0.001763486762399652, -0.2100328542877775, 0.9776943285709134, 0.0012113596359206152, 0.0005476982455656242, 1.8115872085407823, 3.868458788958003], "E40.4.0.13": [-0.011212851217136277, -0.0020251440543597593, -0.5895386691474909, 0.8077401547402515, 0.0012113596359206152, 0.0005476982455656242, 1.8115872085407858, 3.868458788958024], "E40.4.0.14": [-0.010370748968153334, -0.0019366355414648928, -0.8671078923209321, 0.4981203700660625, 0.0012113596359206152, 0.0005476982455656242, 1.8115872085407796, 3.868458788957982], "E40.4.1.0": [-0.009637449939142853, 0.02073673485033079, -0.9947462834841825, 0.10237104812595471, 0.0012113596359206152, 0.0005476982455656242, 1.8115872085408105, 3.8684587889580238], "E40.4.1.1": [-0.009139748194033237, 0.021421762534086612, -0.9503840052467358, -0.31107915804690683, 0.0012113596359206152, 0.0005476982455656242, 1.8115872085407578, 3.868458788958019], "E40.4.1.2": [-0.008963700886032405, 0.02225, -0.741691698534492, -0.6707409517280276, 0.0012113596359206152, 0.0005476982455656242, 1.8115872085407894, 3.86845878895801], "E40.4.1.3": [-0.009139748194033251, 0.023078237465913386, -0.40475415908808526, -0.9144255413651223, 0.0012113596359206152, 0.0005476982455656242, 1.8115872085407891, 3.868458788958003], "E40.4.1.4": [-0.00963744993914284, 0.023763265149669206, 0.002169051540750866, -0.99999764760494, 0.0012113596359206152, 0.0005476982455656242, 1.8115872085407765, 3.868458788958028], "E40.4.1.5": [-0.010370748968153348, 0.024186635541464892, 0.40871721345297557, -0.912661075880436, 0.0012113596359206152, 0.0005476982455656242, 1.8115872085407752, 3.8684587889580118], "E40.4.1.6": [-0.011212851217136277, 0.024275144054359744, 0.7445944560798636, -0.6675171128706231, 0.0012113596359206152, 0.0005476982455656242, 1.8115872085407987, 3.8684587889579762], "E40.4.1.7": [-0.012018149556983757, 0.024013486762399665, 0.9517245528222696, -0.3069533768428862, 0.0012113596359206152, 0.0005476982455656242, 1.8115872085407854, 3.8684587889580118], "E40.4.1.8": [-0.01264740058883039, 0.023446906588446365, 0.9942928282355765, 0.10668538662487148, 0.0012113596359206152, 0.0005476982455656242, 1.8115872085407754, 3.8684587889580206], "E40.4.1.9": [-0.01299180109270373, 0.022673370391795702, 0.8649388407801819, 0.5018772775388773, 0.001211359635920615, 0.000547698245565624, 1.8115872085407736, 3.8684587889580158], "E40.4.1.10": [-0.01299180109270373, 0.021826629608204293, 0.5860290700312074, 0.8102900277544814, 0.0012113596359206152, 0.0005476982455656242, 1.8115872085407756, 3.868458788958045], "E40.4.1.11": [-0.012647400588830363, 0.02105309341155364, 0.20578954916687192, 0.97859627091753, 0.0012113596359206152, 0.0005476982455656242, 1.811587208540781, 3.868458788957996], "E40.4.1.12": [-0.012018149556983743, 0.020486513237600347, -0.2100328542877775, 0.9776943285709134, 0.0012113596359206152, 0.0005476982455656242, 1.811587208540784, 3.8684587889580038], "E40.4.1.13": [-0.011212851217136277, 0.02022485594564024, -0.5895386691474909, 0.8077401547402515, 0.0012113596359206152, 0.0005476982455656242, 1.8115872085407858, 3.8684587889580255], "E40.4.1.14": [-0.010370748968153334, 0.020313364458535106, -0.8671078923209321, 0.4981203700660625, 0.0012113596359206152, 0.0005476982455656242, 1.81158720854078, 3.868458788957984], "E40.4.2.0": [-0.009637449939142853, 0.04298673485033079, -0.9947462834841825, 0.10237104812595471, 0.0012113596359206152, 0.0005476982455656242, 1.8115872085408105, 3.8684587889580255], "E40.4.2.1": [-0.009139748194033237, 0.04367176253408661, -0.9503840052467358, -0.31107915804690683, 0.0012113596359206152, 0.0005476982455656242, 1.8115872085407578, 3.868458788958019], "E40.4.2.2": [-0.008963700886032405, 0.0445, -0.741691698534492, -0.6707409517280276, 0.0012113596359206152, 0.0005476982455656242, 1.8115872085407925, 3.868458788958009], "E40.4.2.3": [-0.009139748194033251, 0.045328237465913385, -0.40475415908808526, -0.9144255413651223, 0.0012113596359206152, 0.0005476982455656242, 1.8115872085407922, 3.868458788957999], "E40.4.2.4": [-0.00963744993914284, 0.046013265149669205, 0.002169051540750866, -0.99999764760494, 0.0012113596359206152, 0.0005476982455656242, 1.8115872085407765, 3.868458788958028], "E40.4.2.5": [-0.010370748968153348, 0.04643663554146489, 0.40871721345297557, -0.912661075880436, 0.0012113596359206152, 0.0005476982455656242, 1.8115872085407785, 3.8684587889580118], "E40.4.2.6": [-0.011212851217136277, 0.04652514405435974, 0.7445944560798636, -0.6675171128706231, 0.0012113596359206152, 0.0005476982455656242, 1.8115872085407987, 3.8684587889579762], "E40.4.2.7": [-0.012018149556983757, 0.046263486762399664, 0.9517245528222696, -0.3069533768428862, 0.0012113596359206152, 0.0005476982455656242, 1.8115872085407847, 3.8684587889580118], "E40.4.2.8": [-0.01264740058883039, 0.045696906588446363, 0.9942928282355765, 0.10668538662487148, 0.0012113596359206152, 0.0005476982455656242, 1.8115872085407754, 3.8684587889580224], "E40.4.2.9": [-0.01299180109270373, 0.0449233703917957, 0.8649388407801819, 0.5018772775388773, 0.001211359635920615, 0.000547698245565624, 1.8115872085407765, 3.8684587889580158], "E40.4.2.10": [-0.01299180109270373, 0.04407662960820429, 0.5860290700312074, 0.8102900277544814, 0.0012113596359206152, 0.0005476982455656242, 1.8115872085407756, 3.868458788958045], "E40.4.2.11": [-0.012647400588830363, 0.04330309341155364, 0.20578954916687192, 0.97859627091753, 0.0012113596359206152, 0.0005476982455656242, 1.811587208540781, 3.868458788957996], "E40.4.2.12": [-0.012018149556983743, 0.042736513237600346, -0.2100328542877775, 0.9776943285709134, 0.0012113596359206152, 0.0005476982455656242, 1.811587208540784, 3.868458788958], "E40.4.2.13": [-0.011212851217136277, 0.04247485594564024, -0.5895386691474909, 0.8077401547402515, 0.0012113596359206152, 0.0005476982455656242, 1.8115872085407827, 3.8684587889580255], "E40.4.2.14": [-0.010370748968153334, 0.042563364458535105, -0.8671078923209321, 0.4981203700660625, 0.0012113596359206152, 0.0005476982455656242, 1.811587208540779, 3.868458788957984], "E40.4.3.0": [-0.009637449939142853, 0.0652367348503308, -0.9947462834841825, 0.10237104812595471, 0.0012113596359206152, 0.0005476982455656242, 1.8115872085408105, 3.8684587889580255], "E40.4.3.1": [-0.009139748194033237, 0.06592176253408662, -0.9503840052467358, -0.31107915804690683, 0.0012113596359206152, 0.0005476982455656242, 1.8115872085407616, 3.8684587889580158], "E40.4.3.2": [-0.008963700886032405, 0.06675, -0.741691698534492, -0.6707409517280276, 0.0012113596359206152, 0.0005476982455656242, 1.811587208540786, 3.868458788958009], "E40.4.3.3": [-0.009139748194033251, 0.06757823746591339, -0.40475415908808526, -0.9144255413651223, 0.0012113596359206152, 0.0005476982455656242, 1.8115872085407922, 3.8684587889580064], "E40.4.3.4": [-0.00963744993914284, 0.06826326514966921, 0.002169051540750866, -0.99999764760494, 0.0012113596359206152, 0.0005476982455656242, 1.8115872085407705, 3.868458788958028], "E40.4.3.5": [-0.010370748968153348, 0.0686866355414649, 0.40871721345297557, -0.912661075880436, 0.0012113596359206152, 0.0005476982455656242, 1.811587208540772, 3.8684587889580038], "E40.4.3.6": [-0.011212851217136277, 0.06877514405435975, 0.7445944560798636, -0.6675171128706231, 0.0012113596359206152, 0.0005476982455656242, 1.8115872085407987, 3.8684587889579762], "E40.4.3.7": [-0.012018149556983757, 0.06851348676239967, 0.9517245528222696, -0.3069533768428862, 0.0012113596359206152, 0.0005476982455656242, 1.8115872085407874, 3.8684587889580118], "E40.4.3.8": [-0.01264740058883039, 0.06794690658844638, 0.9942928282355765, 0.10668538662487148, 0.0012113596359206152, 0.0005476982455656242, 1.8115872085407754, 3.8684587889580224], "E40.4.3.9": [-0.01299180109270373, 0.0671733703917957, 0.8649388407801819, 0.5018772775388773, 0.001211359635920615, 0.000547698245565624, 1.8115872085407765, 3.868458788958016], "E40.4.3.10": [-0.01299180109270373, 0.0663266296082043, 0.5860290700312074, 0.8102900277544814, 0.0012113596359206152, 0.0005476982455656242, 1.8115872085407823, 3.868458788958045], "E40.4.3.11": [-0.012647400588830363, 0.06555309341155365, 0.20578954916687192, 0.97859627091753, 0.0012113596359206152, 0.0005476982455656242, 1.811587208540775, 3.868458788957996], "E40.4.3.12": [-0.012018149556983743, 0.06498651323760035, -0.2100328542877775, 0.9776943285709134, 0.0012113596359206152, 0.0005476982455656242, 1.8115872085407776, 3.8684587889580073], "E40.4.3.13": [-0.011212851217136277, 0.06472485594564024, -0.5895386691474909, 0.8077401547402515, 0.0012113596359206152, 0.0005476982455656242, 1.8115872085407827, 3.8684587889580175], "E40.4.3.14": [-0.010370748968153334, 0.06481336445853511, -0.8671078923209321, 0.4981203700660625, 0.0012113596359206152, 0.0005476982455656242, 1.8115872085407825, 3.868458788957984], "E40.5.0.0": [0.012612550060857153, -0.0015132651496692073, -0.9947462834841825, 0.10237104812595471, 0.0012113596359206152, 0.0005476982455656242, 1.8115872085408105, 3.868458788958024], "E40.5.0.1": [0.013110251805966769, -0.0008282374659133868, -0.9503840052467358, -0.31107915804690683, 0.0012113596359206152, 0.0005476982455656242, 1.8115872085407585, 3.868458788958019], "E40.5.0.2": [0.0132862991139676, 0, -0.741691698534492, -0.6707409517280276, 0.0012113596359206152, 0.0005476982455656242, 1.8115872085407891, 3.8684587889580095], "E40.5.0.3": [0.013110251805966755, 0.0008282374659133868, -0.40475415908808526, -0.9144255413651223, 0.0012113596359206152, 0.0005476982455656242, 1.8115872085407896, 3.868458788958002], "E40.5.0.4": [0.012612550060857167, 0.0015132651496692073, 0.002169051540750866, -0.99999764760494, 0.0012113596359206152, 0.0005476982455656242, 1.8115872085407763, 3.868458788958029], "E40.5.0.5": [0.011879251031846658, 0.0019366355414648928, 0.40871721345297557, -0.912661075880436, 0.0012113596359206152, 0.0005476982455656242, 1.8115872085407752, 3.8684587889580104], "E40.5.0.6": [0.011037148782863729, 0.0020251440543597454, 0.7445944560798636, -0.6675171128706231, 0.0012113596359206152, 0.0005476982455656242, 1.811587208540798, 3.8684587889579785], "E40.5.0.7": [0.01023185044301625, 0.0017634867623996658, 0.9517245528222696, -0.3069533768428862, 0.0012113596359206152, 0.0005476982455656242, 1.811587208540785, 3.8684587889580127], "E40.5.0.8": [0.009602599411169616, 0.0011969065884463656, 0.9942928282355765, 0.10668538662487148, 0.0012113596359206152, 0.0005476982455656242, 1.8115872085407754, 3.868458788958021], "E40.5.0.9": [0.009258198907296275, 0.0004233703917957028, 0.8649388407801819, 0.5018772775388773, 0.001211359635920615, 0.000547698245565624, 1.8115872085407738, 3.8684587889580158], "E40.5.0.10": [0.009258198907296275, -0.0004233703917957062, 0.5860290700312074, 0.8102900277544814, 0.0012113596359206152, 0.0005476982455656242, 1.811587208540776, 3.868458788958045], "E40.5.0.11": [0.009602599411169643, -0.0011969065884463587, 0.20578954916687192, 0.97859627091753, 0.0012113596359206152, 0.0005476982455656242, 1.8115872085407798, 3.8684587889579976], "E40.5.0.12": [0.010231850443016263, -0.001763486762399652, -0.2100328542877775, 0.9776943285709134, 0.0012113596359206152, 0.0005476982455656242, 1.8115872085407823, 3.868458788958003], "E40.5.0.13": [0.011037148782863729, -0.0020251440543597593, -0.5895386691474909, 0.8077401547402515, 0.0012113596359206152, 0.0005476982455656242, 1.8115872085407858, 3.868458788958024], "E40.5.0.14": [0.011879251031846672, -0.0019366355414648928, -0.8671078923209321, 0.4981203700660625, 0.0012113596359206152, 0.0005476982455656242, 1.8115872085407796, 3.868458788957982], "E40.5.1.0": [0.012612550060857153, 0.02073673485033079, -0.9947462834841825, 0.10237104812595471, 0.0012113596359206152, 0.0005476982455656242, 1.8115872085408105, 3.8684587889580238], "E40.5.1.1": [0.013110251805966769, 0.021421762534086612, -0.9503840052467358, -0.31107915804690683, 0.0012113596359206152, 0.0005476982455656242, 1.8115872085407578, 3.868458788958019], "E40.5.1.2": [0.0132862991139676, 0.02225, -0.741691698534492, -0.6707409517280276, 0.0012113596359206152, 0.0005476982455656242, 1.8115872085407894, 3.86845878895801], "E40.5.1.3": [0.013110251805966755, 0.023078237465913386, -0.40475415908808526, -0.9144255413651223, 0.0012113596359206152, 0.0005476982455656242, 1.8115872085407891, 3.868458788958003], "E40.5.1.4": [0.012612550060857167, 0.023763265149669206, 0.002169051540750866, -0.99999764760494, 0.0012113596359206152, 0.0005476982455656242, 1.8115872085407765, 3.868458788958028], "E40.5.1.5": [0.011879251031846658, 0.024186635541464892, 0.40871721345297557, -0.912661075880436, 0.0012113596359206152, 0.0005476982455656242, 1.8115872085407752, 3.8684587889580118], "E40.5.1.6": [0.011037148782863729, 0.024275144054359744, 0.7445944560798636, -0.6675171128706231, 0.0012113596359206152, 0.0005476982455656242, 1.8115872085407987, 3.8684587889579762], "E40.5.1.7": [0.01023185044301625, 0.024013486762399665, 0.9517245528222696, -0.3069533768428862, 0.0012113596359206152, 0.0005476982455656242, 1.8115872085407854, 3.8684587889580118], "E40.5.1.8": [0.009602599411169616, 0.023446906588446365, 0.9942928282355765, 0.10668538662487148, 0.0012113596359206152, 0.0005476982455656242, 1.8115872085407754, 3.8684587889580206], "E40.5.1.9": [0.009258198907296275, 0.022673370391795702, 0.8649388407801819, 0.5018772775388773, 0.001211359635920615, 0.000547698245565624, 1.8115872085407736, 3.8684587889580158], "E40.5.1.10": [0.009258198907296275, 0.021826629608204293, 0.5860290700312074, 0.8102900277544814, 0.0012113596359206152, 0.0005476982455656242, 1.8115872085407756, 3.868458788958045], "E40.5.1.11": [0.009602599411169643, 0.02105309341155364, 0.20578954916687192, 0.97859627091753, 0.0012113596359206152, 0.0005476982455656242, 1.811587208540781, 3.868458788957996], "E40.5.1.12": [0.010231850443016263, 0.020486513237600347, -0.2100328542877775, 0.9776943285709134, 0.0012113596359206152, 0.0005476982455656242, 1.811587208540784, 3.8684587889580038], "E40.5.1.13": [0.011037148782863729, 0.02022485594564024, -0.5895386691474909, 0.8077401547402515, 0.0012113596359206152, 0.0005476982455656242, 1.8115872085407858, 3.8684587889580255], "E40.5.1.14": [0.011879251031846672, 0.020313364458535106, -0.8671078923209321, 0.4981203700660625, 0.0012113596359206152, 0.0005476982455656242, 1.81158720854078, 3.868458788957984], "E40.5.2.0": [0.012612550060857153, 0.04298673485033079, -0.9947462834841825, 0.10237104812595471, 0.0012113596359206152, 0.0005476982455656242, 1.8115872085408105, 3.8684587889580255], "E40.5.2.1": [0.013110251805966769, 0.04367176253408661, -0.9503840052467358, -0.31107915804690683, 0.0012113596359206152, 0.0005476982455656242, 1.8115872085407578, 3.868458788958019], "E40.5.2.2": [0.0132862991139676, 0.0445, -0.741691698534492, -0.6707409517280276, 0.0012113596359206152, 0.0005476982455656242, 1.8115872085407925, 3.868458788958009], "E40.5.2.3": [0.013110251805966755, 0.045328237465913385, -0.40475415908808526, -0.9144255413651223, 0.0012113596359206152, 0.0005476982455656242, 1.8115872085407922, 3.868458788957999], "E40.5.2.4": [0.012612550060857167, 0.046013265149669205, 0.002169051540750866, -0.99999764760494, 0.0012113596359206152, 0.0005476982455656242, 1.8115872085407765, 3.868458788958028], "E40.5.2.5": [0.011879251031846658, 0.04643663554146489, 0.40871721345297557, -0.912661075880436, 0.0012113596359206152, 0.0005476982455656242, 1.8115872085407785, 3.8684587889580118], "E40.5.2.6": [0.011037148782863729, 0.04652514405435974, 0.7445944560798636, -0.6675171128706231, 0.0012113596359206152, 0.0005476982455656242, 1.8115872085407987, 3.8684587889579762], "E40.5.2.7": [0.01023185044301625, 0.046263486762399664, 0.9517245528222696, -0.3069533768428862, 0.0012113596359206152, 0.0005476982455656242, 1.8115872085407847, 3.8684587889580118], "E40.5.2.8": [0.009602599411169616, 0.045696906588446363, 0.9942928282355765, 0.10668538662487148, 0.0012113596359206152, 0.0005476982455656242, 1.8115872085407754, 3.8684587889580224], "E40.5.2.9": [0.009258198907296275, 0.0449233703917957, 0.8649388407801819, 0.5018772775388773, 0.001211359635920615, 0.000547698245565624, 1.8115872085407765, 3.8684587889580158], "E40.5.2.10": [0.009258198907296275, 0.04407662960820429, 0.5860290700312074, 0.8102900277544814, 0.0012113596359206152, 0.0005476982455656242, 1.8115872085407756, 3.868458788958045], "E40.5.2.11": [0.009602599411169643, 0.04330309341155364, 0.20578954916687192, 0.97859627091753, 0.0012113596359206152, 0.0005476982455656242, 1.811587208540781, 3.868458788957996], "E40.5.2.12": [0.010231850443016263, 0.042736513237600346, -0.2100328542877775, 0.9776943285709134, 0.0012113596359206152, 0.0005476982455656242, 1.811587208540784, 3.868458788958], "E40.5.2.13": [0.011037148782863729, 0.04247485594564024, -0.5895386691474909, 0.8077401547402515, 0.0012113596359206152, 0.0005476982455656242, 1.8115872085407827, 3.8684587889580255], "E40.5.2.14": [0.011879251031846672, 0.042563364458535105, -0.8671078923209321, 0.4981203700660625, 0.0012113596359206152, 0.0005476982455656242, 1.811587208540779, 3.868458788957984], "E40.5.3.0": [0.012612550060857153, 0.0652367348503308, -0.9947462834841825, 0.10237104812595471, 0.0012113596359206152, 0.0005476982455656242, 1.8115872085408105, 3.8684587889580255], "E40.5.3.1": [0.013110251805966769, 0.06592176253408662, -0.9503840052467358, -0.31107915804690683, 0.0012113596359206152, 0.0005476982455656242, 1.8115872085407616, 3.8684587889580158], "E40.5.3.2": [0.0132862991139676, 0.06675, -0.741691698534492, -0.6707409517280276, 0.0012113596359206152, 0.0005476982455656242, 1.811587208540786, 3.868458788958009], "E40.5.3.3": [0.013110251805966755, 0.06757823746591339, -0.40475415908808526, -0.9144255413651223, 0.0012113596359206152, 0.0005476982455656242, 1.8115872085407922, 3.8684587889580064], "E40.5.3.4": [0.012612550060857167, 0.06826326514966921, 0.002169051540750866, -0.99999764760494, 0.0012113596359206152, 0.0005476982455656242, 1.8115872085407705, 3.868458788958028], "E40.5.3.5": [0.011879251031846658, 0.0686866355414649, 0.40871721345297557, -0.912661075880436, 0.0012113596359206152, 0.0005476982455656242, 1.811587208540772, 3.8684587889580038], "E40.5.3.6": [0.011037148782863729, 0.06877514405435975, 0.7445944560798636, -0.6675171128706231, 0.0012113596359206152, 0.0005476982455656242, 1.8115872085407987, 3.8684587889579762], "E40.5.3.7": [0.01023185044301625, 0.06851348676239967, 0.9517245528222696, -0.3069533768428862, 0.0012113596359206152, 0.0005476982455656242, 1.8115872085407874, 3.8684587889580118], "E40.5.3.8": [0.009602599411169616, 0.06794690658844638, 0.9942928282355765, 0.10668538662487148, 0.0012113596359206152, 0.0005476982455656242, 1.8115872085407754, 3.8684587889580224], "E40.5.3.9": [0.009258198907296275, 0.0671733703917957, 0.8649388407801819, 0.5018772775388773, 0.001211359635920615, 0.000547698245565624, 1.8115872085407765, 3.868458788958016], "E40.5.3.10": [0.009258198907296275, 0.0663266296082043, 0.5860290700312074, 0.8102900277544814, 0.0012113596359206152, 0.0005476982455656242, 1.8115872085407823, 3.868458788958045], "E40.5.3.11": [0.009602599411169643, 0.06555309341155365, 0.20578954916687192, 0.97859627091753, 0.0012113596359206152, 0.0005476982455656242, 1.811587208540775, 3.868458788957996], "E40.5.3.12": [0.010231850443016263, 0.06498651323760035, -0.2100328542877775, 0.9776943285709134, 0.0012113596359206152, 0.0005476982455656242, 1.8115872085407776, 3.8684587889580073], "E40.5.3.13": [0.011037148782863729, 0.06472485594564024, -0.5895386691474909, 0.8077401547402515, 0.0012113596359206152, 0.0005476982455656242, 1.8115872085407827, 3.8684587889580175], "E40.5.3.14": [0.011879251031846672, 0.06481336445853511, -0.8671078923209321, 0.4981203700660625, 0.0012113596359206152, 0.0005476982455656242, 1.8115872085407825, 3.868458788957984], "E40.6.0.0": [0.03486255006085716, -0.0015132651496692073, -0.9947462834841825, 0.10237104812595471, 0.0012113596359206152, 0.0005476982455656242, 1.8115872085408105, 3.868458788958024], "E40.6.0.1": [0.035360251805966775, -0.0008282374659133868, -0.9503840052467358, -0.31107915804690683, 0.0012113596359206152, 0.0005476982455656242, 1.8115872085407585, 3.868458788958019], "E40.6.0.2": [0.03553629911396761, 0, -0.741691698534492, -0.6707409517280276, 0.0012113596359206152, 0.0005476982455656242, 1.8115872085407891, 3.8684587889580095], "E40.6.0.3": [0.03536025180596676, 0.0008282374659133868, -0.40475415908808526, -0.9144255413651223, 0.0012113596359206152, 0.0005476982455656242, 1.8115872085407905, 3.868458788958002], "E40.6.0.4": [0.03486255006085717, 0.0015132651496692073, 0.002169051540750866, -0.99999764760494, 0.0012113596359206152, 0.0005476982455656242, 1.8115872085407763, 3.8684587889580273], "E40.6.0.5": [0.034129251031846664, 0.0019366355414648928, 0.40871721345297557, -0.912661075880436, 0.0012113596359206152, 0.0005476982455656242, 1.8115872085407752, 3.8684587889580113], "E40.6.0.6": [0.033287148782863735, 0.0020251440543597454, 0.7445944560798636, -0.6675171128706231, 0.0012113596359206152, 0.0005476982455656242, 1.811587208540798, 3.8684587889579767], "E40.6.0.7": [0.032481850443016255, 0.0017634867623996658, 0.9517245528222696, -0.3069533768428862, 0.0012113596359206152, 0.0005476982455656242, 1.811587208540785, 3.8684587889580127], "E40.6.0.8": [0.03185259941116962, 0.0011969065884463656, 0.9942928282355765, 0.10668538662487148, 0.0012113596359206152, 0.0005476982455656242, 1.8115872085407754, 3.868458788958021], "E40.6.0.9": [0.03150819890729628, 0.0004233703917957028, 0.8649388407801819, 0.5018772775388773, 0.001211359635920615, 0.000547698245565624, 1.8115872085407738, 3.8684587889580158], "E40.6.0.10": [0.03150819890729628, -0.0004233703917957062, 0.5860290700312074, 0.8102900277544814, 0.0012113596359206152, 0.0005476982455656242, 1.811587208540776, 3.868458788958045], "E40.6.0.11": [0.03185259941116965, -0.0011969065884463587, 0.20578954916687192, 0.97859627091753, 0.0012113596359206152, 0.0005476982455656242, 1.8115872085407798, 3.8684587889579958], "E40.6.0.12": [0.03248185044301627, -0.001763486762399652, -0.2100328542877775, 0.9776943285709134, 0.0012113596359206152, 0.0005476982455656242, 1.8115872085407814, 3.868458788958003], "E40.6.0.13": [0.033287148782863735, -0.0020251440543597593, -0.5895386691474909, 0.8077401547402515, 0.0012113596359206152, 0.0005476982455656242, 1.8115872085407858, 3.8684587889580233], "E40.6.0.14": [0.03412925103184668, -0.0019366355414648928, -0.8671078923209321, 0.4981203700660625, 0.0012113596359206152, 0.0005476982455656242, 1.8115872085407796, 3.8684587889579802], "E40.6.1.0": [0.03486255006085716, 0.02073673485033079, -0.9947462834841825, 0.10237104812595471, 0.0012113596359206152, 0.0005476982455656242, 1.8115872085408105, 3.8684587889580238], "E40.6.1.1": [0.035360251805966775, 0.021421762534086612, -0.9503840052467358, -0.31107915804690683, 0.0012113596359206152, 0.0005476982455656242, 1.8115872085407578, 3.868458788958019], "E40.6.1.2": [0.03553629911396761, 0.02225, -0.741691698534492, -0.6707409517280276, 0.0012113596359206152, 0.0005476982455656242, 1.8115872085407894, 3.86845878895801], "E40.6.1.3": [0.03536025180596676, 0.023078237465913386, -0.40475415908808526, -0.9144255413651223, 0.0012113596359206152, 0.0005476982455656242, 1.8115872085407896, 3.868458788958003], "E40.6.1.4": [0.03486255006085717, 0.023763265149669206, 0.002169051540750866, -0.99999764760494, 0.0012113596359206152, 0.0005476982455656242, 1.8115872085407763, 3.8684587889580273], "E40.6.1.5": [0.034129251031846664, 0.024186635541464892, 0.40871721345297557, -0.912661075880436, 0.0012113596359206152, 0.0005476982455656242, 1.8115872085407752, 3.8684587889580118], "E40.6.1.6": [0.033287148782863735, 0.024275144054359744, 0.7445944560798636, -0.6675171128706231, 0.0012113596359206152, 0.0005476982455656242, 1.8115872085407987, 3.868458788957976], "E40.6.1.7": [0.032481850443016255, 0.024013486762399665, 0.9517245528222696, -0.3069533768428862, 0.0012113596359206152, 0.0005476982455656242, 1.8115872085407854, 3.8684587889580118], "E40.6.1.8": [0.03185259941116962, 0.023446906588446365, 0.9942928282355765, 0.10668538662487148, 0.0012113596359206152, 0.0005476982455656242, 1.8115872085407754, 3.8684587889580206], "E40.6.1.9": [0.03150819890729628, 0.022673370391795702, 0.8649388407801819, 0.5018772775388773, 0.001211359635920615, 0.000547698245565624, 1.8115872085407736, 3.8684587889580158], "E40.6.1.10": [0.03150819890729628, 0.021826629608204293, 0.5860290700312074, 0.8102900277544814, 0.0012113596359206152, 0.0005476982455656242, 1.8115872085407756, 3.868458788958045], "E40.6.1.11": [0.03185259941116965, 0.02105309341155364, 0.20578954916687192, 0.97859627091753, 0.0012113596359206152, 0.0005476982455656242, 1.811587208540781, 3.868458788957996], "E40.6.1.12": [0.03248185044301627, 0.020486513237600347, -0.2100328542877775, 0.9776943285709134, 0.0012113596359206152, 0.0005476982455656242, 1.8115872085407831, 3.8684587889580038], "E40.6.1.13": [0.033287148782863735, 0.02022485594564024, -0.5895386691474909, 0.8077401547402515, 0.0012113596359206152, 0.0005476982455656242, 1.8115872085407858, 3.868458788958025], "E40.6.1.14": [0.03412925103184668, 0.020313364458535106, -0.8671078923209321, 0.4981203700660625, 0.0012113596359206152, 0.0005476982455656242, 1.81158720854078, 3.868458788957983], "E40.6.2.0": [0.03486255006085716, 0.04298673485033079, -0.9947462834841825, 0.10237104812595471, 0.0012113596359206152, 0.0005476982455656242, 1.8115872085408105, 3.8684587889580255], "E40.6.2.1": [0.035360251805966775, 0.04367176253408661, -0.9503840052467358, -0.31107915804690683, 0.0012113596359206152, 0.0005476982455656242, 1.8115872085407578, 3.868458788958019], "E40.6.2.2": [0.03553629911396761, 0.0445, -0.741691698534492, -0.6707409517280276, 0.0012113596359206152, 0.0005476982455656242, 1.8115872085407914, 3.868458788958009], "E40.6.2.3": [0.03536025180596676, 0.045328237465913385, -0.40475415908808526, -0.9144255413651223, 0.0012113596359206152, 0.0005476982455656242, 1.8115872085407922, 3.868458788958], "E40.6.2.4": [0.03486255006085717, 0.046013265149669205, 0.002169051540750866, -0.99999764760494, 0.0012113596359206152, 0.0005476982455656242, 1.8115872085407763, 3.8684587889580273], "E40.6.2.5": [0.034129251031846664, 0.04643663554146489, 0.40871721345297557, -0.912661075880436, 0.0012113596359206152, 0.0005476982455656242, 1.8115872085407778, 3.8684587889580118], "E40.6.2.6": [0.033287148782863735, 0.04652514405435974, 0.7445944560798636, -0.6675171128706231, 0.0012113596359206152, 0.0005476982455656242, 1.8115872085407987, 3.868458788957976], "E40.6.2.7": [0.032481850443016255, 0.046263486762399664, 0.9517245528222696, -0.3069533768428862, 0.0012113596359206152, 0.0005476982455656242, 1.8115872085407847, 3.8684587889580118], "E40.6.2.8": [0.03185259941116962, 0.045696906588446363, 0.9942928282355765, 0.10668538662487148, 0.0012113596359206152, 0.0005476982455656242, 1.8115872085407754, 3.8684587889580224], "E40.6.2.9": [0.03150819890729628, 0.0449233703917957, 0.8649388407801819, 0.5018772775388773, 0.001211359635920615, 0.000547698245565624, 1.8115872085407754, 3.8684587889580158], "E40.6.2.10": [0.03150819890729628, 0.04407662960820429, 0.5860290700312074, 0.8102900277544814, 0.0012113596359206152, 0.0005476982455656242, 1.8115872085407756, 3.868458788958045], "E40.6.2.11": [0.03185259941116965, 0.04330309341155364, 0.20578954916687192, 0.97859627091753, 0.0012113596359206152, 0.0005476982455656242, 1.811587208540781, 3.868458788957996], "E40.6.2.12": [0.03248185044301627, 0.042736513237600346, -0.2100328542877775, 0.9776943285709134, 0.0012113596359206152, 0.0005476982455656242, 1.8115872085407831, 3.868458788958], "E40.6.2.13": [0.033287148782863735, 0.04247485594564024, -0.5895386691474909, 0.8077401547402515, 0.0012113596359206152, 0.0005476982455656242, 1.8115872085407836, 3.868458788958025], "E40.6.2.14": [0.03412925103184668, 0.042563364458535105, -0.8671078923209321, 0.4981203700660625, 0.0012113596359206152, 0.0005476982455656242, 1.811587208540779, 3.868458788957983], "E40.6.3.0": [0.03486255006085716, 0.0652367348503308, -0.9947462834841825, 0.10237104812595471, 0.0012113596359206152, 0.0005476982455656242, 1.8115872085408105, 3.8684587889580255], "E40.6.3.1": [0.035360251805966775, 0.06592176253408662, -0.9503840052467358, -0.31107915804690683, 0.0012113596359206152, 0.0005476982455656242, 1.8115872085407603, 3.8684587889580175], "E40.6.3.2": [0.03553629911396761, 0.06675, -0.741691698534492, -0.6707409517280276, 0.0012113596359206152, 0.0005476982455656242, 1.8115872085407871, 3.868458788958009], "E40.6.3.3": [0.03536025180596676, 0.06757823746591339, -0.40475415908808526, -0.9144255413651223, 0.0012113596359206152, 0.0005476982455656242, 1.8115872085407922, 3.868458788958005], "E40.6.3.4": [0.03486255006085717, 0.06826326514966921, 0.002169051540750866, -0.99999764760494, 0.0012113596359206152, 0.0005476982455656242, 1.8115872085407705, 3.8684587889580273], "E40.6.3.5": [0.034129251031846664, 0.0686866355414649, 0.40871721345297557, -0.912661075880436, 0.0012113596359206152, 0.0005476982455656242, 1.8115872085407727, 3.868458788958004], "E40.6.3.6": [0.033287148782863735, 0.06877514405435975, 0.7445944560798636, -0.6675171128706231, 0.0012113596359206152, 0.0005476982455656242, 1.8115872085407987, 3.868458788957976], "E40.6.3.7": [0.032481850443016255, 0.06851348676239967, 0.9517245528222696, -0.3069533768428862, 0.0012113596359206152, 0.0005476982455656242, 1.8115872085407858, 3.8684587889580118], "E40.6.3.8": [0.03185259941116962, 0.06794690658844638, 0.9942928282355765, 0.10668538662487148, 0.0012113596359206152, 0.0005476982455656242, 1.8115872085407754, 3.8684587889580224], "E40.6.3.9": [0.03150819890729628, 0.0671733703917957, 0.8649388407801819, 0.5018772775388773, 0.001211359635920615, 0.000547698245565624, 1.8115872085407754, 3.868458788958016], "E40.6.3.10": [0.03150819890729628, 0.0663266296082043, 0.5860290700312074, 0.8102900277544814, 0.0012113596359206152, 0.0005476982455656242, 1.8115872085407823, 3.868458788958045], "E40.6.3.11": [0.03185259941116965, 0.06555309341155365, 0.20578954916687192, 0.97859627091753, 0.0012113596359206152, 0.0005476982455656242, 1.8115872085407752, 3.868458788957996], "E40.6.3.12": [0.03248185044301627, 0.06498651323760035, -0.2100328542877775, 0.9776943285709134, 0.0012113596359206152, 0.0005476982455656242, 1.8115872085407776, 3.8684587889580073], "E40.6.3.13": [0.033287148782863735, 0.06472485594564024, -0.5895386691474909, 0.8077401547402515, 0.0012113596359206152, 0.0005476982455656242, 1.8115872085407836, 3.8684587889580175], "E40.6.3.14": [0.03412925103184668, 0.06481336445853511, -0.8671078923209321, 0.4981203700660625, 0.0012113596359206152, 0.0005476982455656242, 1.8115872085407811, 3.868458788957983], "E40.7.0.0": [0.05711255006085718, -0.0015132651496692073, -0.9947462834841825, 0.10237104812595471, 0.0012113596359206152, 0.0005476982455656242, 1.8115872085408105, 3.868458788958024], "E40.7.0.1": [0.057610251805966795, -0.0008282374659133868, -0.9503840052467358, -0.31107915804690683, 0.0012113596359206152, 0.0005476982455656242, 1.8115872085407585, 3.868458788958019], "E40.7.0.2": [0.057786299113967626, 0, -0.741691698534492, -0.6707409517280276, 0.0012113596359206152, 0.0005476982455656242, 1.8115872085407891, 3.8684587889580095], "E40.7.0.3": [0.05761025180596678, 0.0008282374659133868, -0.40475415908808526, -0.9144255413651223, 0.0012113596359206152, 0.0005476982455656242, 1.8115872085407905, 3.868458788958002], "E40.7.0.4": [0.05711255006085719, 0.0015132651496692073, 0.002169051540750866, -0.99999764760494, 0.0012113596359206152, 0.0005476982455656242, 1.8115872085407763, 3.8684587889580273], "E40.7.0.5": [0.05637925103184668, 0.0019366355414648928, 0.40871721345297557, -0.912661075880436, 0.0012113596359206152, 0.0005476982455656242, 1.8115872085407752, 3.8684587889580113], "E40.7.0.6": [0.055537148782863754, 0.0020251440543597454, 0.7445944560798636, -0.6675171128706231, 0.0012113596359206152, 0.0005476982455656242, 1.811587208540798, 3.8684587889579767], "E40.7.0.7": [0.054731850443016275, 0.0017634867623996658, 0.9517245528222696, -0.3069533768428862, 0.0012113596359206152, 0.0005476982455656242, 1.811587208540785, 3.8684587889580127], "E40.7.0.8": [0.05410259941116964, 0.0011969065884463656, 0.9942928282355765, 0.10668538662487148, 0.0012113596359206152, 0.0005476982455656242, 1.8115872085407754, 3.868458788958021], "E40.7.0.9": [0.0537581989072963, 0.0004233703917957028, 0.8649388407801819, 0.5018772775388773, 0.001211359635920615, 0.000547698245565624, 1.8115872085407738, 3.8684587889580158], "E40.7.0.10": [0.0537581989072963, -0.0004233703917957062, 0.5860290700312074, 0.8102900277544814, 0.0012113596359206152, 0.0005476982455656242, 1.811587208540776, 3.868458788958045], "E40.7.0.11": [0.05410259941116967, -0.0011969065884463587, 0.20578954916687192, 0.97859627091753, 0.0012113596359206152, 0.0005476982455656242, 1.8115872085407798, 3.8684587889579958], "E40.7.0.12": [0.05473185044301629, -0.001763486762399652, -0.2100328542877775, 0.9776943285709134, 0.0012113596359206152, 0.0005476982455656242, 1.8115872085407814, 3.868458788958003], "E40.7.0.13": [0.055537148782863754, -0.0020251440543597593, -0.5895386691474909, 0.8077401547402515, 0.0012113596359206152, 0.0005476982455656242, 1.8115872085407858, 3.8684587889580233], "E40.7.0.14": [0.0563792510318467, -0.0019366355414648928, -0.8671078923209321, 0.4981203700660625, 0.0012113596359206152, 0.0005476982455656242, 1.8115872085407796, 3.8684587889579802], "E40.7.1.0": [0.05711255006085718, 0.02073673485033079, -0.9947462834841825, 0.10237104812595471, 0.0012113596359206152, 0.0005476982455656242, 1.8115872085408105, 3.8684587889580238], "E40.7.1.1": [0.057610251805966795, 0.021421762534086612, -0.9503840052467358, -0.31107915804690683, 0.0012113596359206152, 0.0005476982455656242, 1.8115872085407578, 3.868458788958019], "E40.7.1.2": [0.057786299113967626, 0.02225, -0.741691698534492, -0.6707409517280276, 0.0012113596359206152, 0.0005476982455656242, 1.8115872085407894, 3.86845878895801], "E40.7.1.3": [0.05761025180596678, 0.023078237465913386, -0.40475415908808526, -0.9144255413651223, 0.0012113596359206152, 0.0005476982455656242, 1.8115872085407896, 3.868458788958003], "E40.7.1.4": [0.05711255006085719, 0.023763265149669206, 0.002169051540750866, -0.99999764760494, 0.0012113596359206152, 0.0005476982455656242, 1.8115872085407763, 3.8684587889580273], "E40.7.1.5": [0.05637925103184668, 0.024186635541464892, 0.40871721345297557, -0.912661075880436, 0.0012113596359206152, 0.0005476982455656242, 1.8115872085407752, 3.8684587889580118], "E40.7.1.6": [0.055537148782863754, 0.024275144054359744, 0.7445944560798636, -0.6675171128706231, 0.0012113596359206152, 0.0005476982455656242, 1.8115872085407987, 3.868458788957976], "E40.7.1.7": [0.054731850443016275, 0.024013486762399665, 0.9517245528222696, -0.3069533768428862, 0.0012113596359206152, 0.0005476982455656242, 1.8115872085407854, 3.8684587889580118], "E40.7.1.8": [0.05410259941116964, 0.023446906588446365, 0.9942928282355765, 0.10668538662487148, 0.0012113596359206152, 0.0005476982455656242, 1.8115872085407754, 3.8684587889580206], "E40.7.1.9": [0.0537581989072963, 0.022673370391795702, 0.8649388407801819, 0.5018772775388773, 0.001211359635920615, 0.000547698245565624, 1.8115872085407736, 3.8684587889580158], "E40.7.1.10": [0.0537581989072963, 0.021826629608204293, 0.5860290700312074, 0.8102900277544814, 0.0012113596359206152, 0.0005476982455656242, 1.8115872085407756, 3.868458788958045], "E40.7.1.11": [0.05410259941116967, 0.02105309341155364, 0.20578954916687192, 0.97859627091753, 0.0012113596359206152, 0.0005476982455656242, 1.811587208540781, 3.868458788957996], "E40.7.1.12": [0.05473185044301629, 0.020486513237600347, -0.2100328542877775, 0.9776943285709134, 0.0012113596359206152, 0.0005476982455656242, 1.8115872085407831, 3.8684587889580038], "E40.7.1.13": [0.055537148782863754, 0.02022485594564024, -0.5895386691474909, 0.8077401547402515, 0.0012113596359206152, 0.0005476982455656242, 1.8115872085407858, 3.868458788958025], "E40.7.1.14": [0.0563792510318467, 0.020313364458535106, -0.8671078923209321, 0.4981203700660625, 0.0012113596359206152, 0.0005476982455656242, 1.81158720854078, 3.868458788957983], "E40.7.2.0": [0.05711255006085718, 0.04298673485033079, -0.9947462834841825, 0.10237104812595471, 0.0012113596359206152, 0.0005476982455656242, 1.8115872085408105, 3.8684587889580255], "E40.7.2.1": [0.057610251805966795, 0.04367176253408661, -0.9503840052467358, -0.31107915804690683, 0.0012113596359206152, 0.0005476982455656242, 1.8115872085407578, 3.868458788958019], "E40.7.2.2": [0.057786299113967626, 0.0445, -0.741691698534492, -0.6707409517280276, 0.0012113596359206152, 0.0005476982455656242, 1.8115872085407914, 3.868458788958009], "E40.7.2.3": [0.05761025180596678, 0.045328237465913385, -0.40475415908808526, -0.9144255413651223, 0.0012113596359206152, 0.0005476982455656242, 1.8115872085407922, 3.868458788958], "E40.7.2.4": [0.05711255006085719, 0.046013265149669205, 0.002169051540750866, -0.99999764760494, 0.0012113596359206152, 0.0005476982455656242, 1.8115872085407763, 3.8684587889580273], "E40.7.2.5": [0.05637925103184668, 0.04643663554146489, 0.40871721345297557, -0.912661075880436, 0.0012113596359206152, 0.0005476982455656242, 1.8115872085407778, 3.8684587889580118], "E40.7.2.6": [0.055537148782863754, 0.04652514405435974, 0.7445944560798636, -0.6675171128706231, 0.0012113596359206152, 0.0005476982455656242, 1.8115872085407987, 3.868458788957976], "E40.7.2.7": [0.054731850443016275, 0.046263486762399664, 0.9517245528222696, -0.3069533768428862, 0.0012113596359206152, 0.0005476982455656242, 1.8115872085407847, 3.8684587889580118], "E40.7.2.8": [0.05410259941116964, 0.045696906588446363, 0.9942928282355765, 0.10668538662487148, 0.0012113596359206152, 0.0005476982455656242, 1.8115872085407754, 3.8684587889580224], "E40.7.2.9": [0.0537581989072963, 0.0449233703917957, 0.8649388407801819, 0.5018772775388773, 0.001211359635920615, 0.000547698245565624, 1.8115872085407754, 3.8684587889580158], "E40.7.2.10": [0.0537581989072963, 0.04407662960820429, 0.5860290700312074, 0.8102900277544814, 0.0012113596359206152, 0.0005476982455656242, 1.8115872085407756, 3.868458788958045], "E40.7.2.11": [0.05410259941116967, 0.04330309341155364, 0.20578954916687192, 0.97859627091753, 0.0012113596359206152, 0.0005476982455656242, 1.811587208540781, 3.868458788957996], "E40.7.2.12": [0.05473185044301629, 0.042736513237600346, -0.2100328542877775, 0.9776943285709134, 0.0012113596359206152, 0.0005476982455656242, 1.8115872085407831, 3.868458788958], "E40.7.2.13": [0.055537148782863754, 0.04247485594564024, -0.5895386691474909, 0.8077401547402515, 0.0012113596359206152, 0.0005476982455656242, 1.8115872085407836, 3.868458788958025], "E40.7.2.14": [0.0563792510318467, 0.042563364458535105, -0.8671078923209321, 0.4981203700660625, 0.0012113596359206152, 0.0005476982455656242, 1.811587208540779, 3.868458788957983], "E40.7.3.0": [0.05711255006085718, 0.0652367348503308, -0.9947462834841825, 0.10237104812595471, 0.0012113596359206152, 0.0005476982455656242, 1.8115872085408105, 3.8684587889580255], "E40.7.3.1": [0.057610251805966795, 0.06592176253408662, -0.9503840052467358, -0.31107915804690683, 0.0012113596359206152, 0.0005476982455656242, 1.8115872085407603, 3.8684587889580175], "E40.7.3.2": [0.057786299113967626, 0.06675, -0.741691698534492, -0.6707409517280276, 0.0012113596359206152, 0.0005476982455656242, 1.8115872085407871, 3.868458788958009], "E40.7.3.3": [0.05761025180596678, 0.06757823746591339, -0.40475415908808526, -0.9144255413651223, 0.0012113596359206152, 0.0005476982455656242, 1.8115872085407922, 3.868458788958005], "E40.7.3.4": [0.05711255006085719, 0.06826326514966921, 0.002169051540750866, -0.99999764760494, 0.0012113596359206152, 0.0005476982455656242, 1.8115872085407705, 3.8684587889580273], "E40.7.3.5": [0.05637925103184668, 0.0686866355414649, 0.40871721345297557, -0.912661075880436, 0.0012113596359206152, 0.0005476982455656242, 1.8115872085407727, 3.868458788958004], "E40.7.3.6": [0.055537148782863754, 0.06877514405435975, 0.7445944560798636, -0.6675171128706231, 0.0012113596359206152, 0.0005476982455656242, 1.8115872085407987, 3.868458788957976], "E40.7.3.7": [0.054731850443016275, 0.06851348676239967, 0.9517245528222696, -0.3069533768428862, 0.0012113596359206152, 0.0005476982455656242, 1.8115872085407858, 3.8684587889580118], "E40.7.3.8": [0.05410259941116964, 0.06794690658844638, 0.9942928282355765, 0.10668538662487148, 0.0012113596359206152, 0.0005476982455656242, 1.8115872085407754, 3.8684587889580224], "E40.7.3.9": [0.0537581989072963, 0.0671733703917957, 0.8649388407801819, 0.5018772775388773, 0.001211359635920615, 0.000547698245565624, 1.8115872085407754, 3.868458788958016], "E40.7.3.10": [0.0537581989072963, 0.0663266296082043, 0.5860290700312074, 0.8102900277544814, 0.0012113596359206152, 0.0005476982455656242, 1.8115872085407807, 3.868458788958045], "E40.7.3.11": [0.05410259941116967, 0.06555309341155365, 0.20578954916687192, 0.97859627091753, 0.0012113596359206152, 0.0005476982455656242, 1.8115872085407752, 3.868458788957996], "E40.7.3.12": [0.05473185044301629, 0.06498651323760035, -0.2100328542877775, 0.9776943285709134, 0.0012113596359206152, 0.0005476982455656242, 1.8115872085407776, 3.8684587889580073], "E40.7.3.13": [0.055537148782863754, 0.06472485594564024, -0.5895386691474909, 0.8077401547402515, 0.0012113596359206152, 0.0005476982455656242, 1.8115872085407836, 3.8684587889580175], "E40.7.3.14": [0.0563792510318467, 0.06481336445853511, -0.8671078923209321, 0.4981203700660625, 0.0012113596359206152, 0.0005476982455656242, 1.8115872085407811, 3.868458788957983], "E40.8.0.0": [0.07936255006085717, -0.0015132651496692073, -0.9947462834841825, 0.10237104812595471, 0.0012113596359206152, 0.0005476982455656242, 1.8115872085408105, 3.868458788958024], "E40.8.0.1": [0.07986025180596679, -0.0008282374659133868, -0.9503840052467358, -0.31107915804690683, 0.0012113596359206152, 0.0005476982455656242, 1.8115872085407585, 3.868458788958019], "E40.8.0.2": [0.08003629911396762, 0, -0.741691698534492, -0.6707409517280276, 0.0012113596359206152, 0.0005476982455656242, 1.8115872085407891, 3.8684587889580095], "E40.8.0.3": [0.07986025180596677, 0.0008282374659133868, -0.40475415908808526, -0.9144255413651223, 0.0012113596359206152, 0.0005476982455656242, 1.8115872085407905, 3.868458788958002], "E40.8.0.4": [0.07936255006085718, 0.0015132651496692073, 0.002169051540750866, -0.99999764760494, 0.0012113596359206152, 0.0005476982455656242, 1.8115872085407774, 3.8684587889580273], "E40.8.0.5": [0.07862925103184668, 0.0019366355414648928, 0.40871721345297557, -0.912661075880436, 0.0012113596359206152, 0.0005476982455656242, 1.8115872085407752, 3.8684587889580113], "E40.8.0.6": [0.07778714878286375, 0.0020251440543597454, 0.7445944560798636, -0.6675171128706231, 0.0012113596359206152, 0.0005476982455656242, 1.811587208540798, 3.8684587889579767], "E40.8.0.7": [0.07698185044301627, 0.0017634867623996658, 0.9517245528222696, -0.3069533768428862, 0.0012113596359206152, 0.0005476982455656242, 1.811587208540785, 3.8684587889580127], "E40.8.0.8": [0.07635259941116963, 0.0011969065884463656, 0.9942928282355765, 0.10668538662487148, 0.0012113596359206152, 0.0005476982455656242, 1.8115872085407754, 3.868458788958021], "E40.8.0.9": [0.07600819890729629, 0.0004233703917957028, 0.8649388407801819, 0.5018772775388773, 0.001211359635920615, 0.000547698245565624, 1.8115872085407738, 3.8684587889580158], "E40.8.0.10": [0.07600819890729629, -0.0004233703917957062, 0.5860290700312074, 0.8102900277544814, 0.0012113596359206152, 0.0005476982455656242, 1.811587208540776, 3.868458788958045], "E40.8.0.11": [0.07635259941116966, -0.0011969065884463587, 0.20578954916687192, 0.97859627091753, 0.0012113596359206152, 0.0005476982455656242, 1.8115872085407798, 3.8684587889579958], "E40.8.0.12": [0.07698185044301628, -0.001763486762399652, -0.2100328542877775, 0.9776943285709134, 0.0012113596359206152, 0.0005476982455656242, 1.8115872085407814, 3.868458788958003], "E40.8.0.13": [0.07778714878286375, -0.0020251440543597593, -0.5895386691474909, 0.8077401547402515, 0.0012113596359206152, 0.0005476982455656242, 1.8115872085407858, 3.8684587889580233], "E40.8.0.14": [0.07862925103184669, -0.0019366355414648928, -0.8671078923209321, 0.4981203700660625, 0.0012113596359206152, 0.0005476982455656242, 1.8115872085407796, 3.8684587889579802], "E40.8.1.0": [0.07936255006085717, 0.02073673485033079, -0.9947462834841825, 0.10237104812595471, 0.0012113596359206152, 0.0005476982455656242, 1.8115872085408105, 3.8684587889580238], "E40.8.1.1": [0.07986025180596679, 0.021421762534086612, -0.9503840052467358, -0.31107915804690683, 0.0012113596359206152, 0.0005476982455656242, 1.8115872085407578, 3.868458788958019], "E40.8.1.2": [0.08003629911396762, 0.02225, -0.741691698534492, -0.6707409517280276, 0.0012113596359206152, 0.0005476982455656242, 1.8115872085407894, 3.86845878895801], "E40.8.1.3": [0.07986025180596677, 0.023078237465913386, -0.40475415908808526, -0.9144255413651223, 0.0012113596359206152, 0.0005476982455656242, 1.8115872085407896, 3.868458788958003], "E40.8.1.4": [0.07936255006085718, 0.023763265149669206, 0.002169051540750866, -0.99999764760494, 0.0012113596359206152, 0.0005476982455656242, 1.8115872085407771, 3.8684587889580273], "E40.8.1.5": [0.07862925103184668, 0.024186635541464892, 0.40871721345297557, -0.912661075880436, 0.0012113596359206152, 0.0005476982455656242, 1.8115872085407752, 3.8684587889580118], "E40.8.1.6": [0.07778714878286375, 0.024275144054359744, 0.7445944560798636, -0.6675171128706231, 0.0012113596359206152, 0.0005476982455656242, 1.8115872085407987, 3.868458788957976], "E40.8.1.7": [0.07698185044301627, 0.024013486762399665, 0.9517245528222696, -0.3069533768428862, 0.0012113596359206152, 0.0005476982455656242, 1.8115872085407854, 3.8684587889580118], "E40.8.1.8": [0.07635259941116963, 0.023446906588446365, 0.9942928282355765, 0.10668538662487148, 0.0012113596359206152, 0.0005476982455656242, 1.8115872085407754, 3.8684587889580206], "E40.8.1.9": [0.07600819890729629, 0.022673370391795702, 0.8649388407801819, 0.5018772775388773, 0.001211359635920615, 0.000547698245565624, 1.8115872085407736, 3.8684587889580158], "E40.8.1.10": [0.07600819890729629, 0.021826629608204293, 0.5860290700312074, 0.8102900277544814, 0.0012113596359206152, 0.0005476982455656242, 1.8115872085407756, 3.868458788958045], "E40.8.1.11": [0.07635259941116966, 0.02105309341155364, 0.20578954916687192, 0.97859627091753, 0.0012113596359206152, 0.0005476982455656242, 1.811587208540781, 3.868458788957996], "E40.8.1.12": [0.07698185044301628, 0.020486513237600347, -0.2100328542877775, 0.9776943285709134, 0.0012113596359206152, 0.0005476982455656242, 1.8115872085407831, 3.8684587889580038], "E40.8.1.13": [0.07778714878286375, 0.02022485594564024, -0.5895386691474909, 0.8077401547402515, 0.0012113596359206152, 0.0005476982455656242, 1.8115872085407858, 3.868458788958025], "E40.8.1.14": [0.07862925103184669, 0.020313364458535106, -0.8671078923209321, 0.4981203700660625, 0.0012113596359206152, 0.0005476982455656242, 1.81158720854078, 3.868458788957983], "E40.8.2.0": [0.07936255006085717, 0.04298673485033079, -0.9947462834841825, 0.10237104812595471, 0.0012113596359206152, 0.0005476982455656242, 1.8115872085408105, 3.8684587889580255], "E40.8.2.1": [0.07986025180596679, 0.04367176253408661, -0.9503840052467358, -0.31107915804690683, 0.0012113596359206152, 0.0005476982455656242, 1.8115872085407578, 3.868458788958019], "E40.8.2.2": [0.08003629911396762, 0.0445, -0.741691698534492, -0.6707409517280276, 0.0012113596359206152, 0.0005476982455656242, 1.8115872085407914, 3.868458788958009], "E40.8.2.3": [0.07986025180596677, 0.045328237465913385, -0.40475415908808526, -0.9144255413651223, 0.0012113596359206152, 0.0005476982455656242, 1.8115872085407922, 3.868458788958], "E40.8.2.4": [0.07936255006085718, 0.046013265149669205, 0.002169051540750866, -0.99999764760494, 0.0012113596359206152, 0.0005476982455656242, 1.8115872085407771, 3.8684587889580273], "E40.8.2.5": [0.07862925103184668, 0.04643663554146489, 0.40871721345297557, -0.912661075880436, 0.0012113596359206152, 0.0005476982455656242, 1.8115872085407778, 3.8684587889580118], "E40.8.2.6": [0.07778714878286375, 0.04652514405435974, 0.7445944560798636, -0.6675171128706231, 0.0012113596359206152, 0.0005476982455656242, 1.8115872085407987, 3.868458788957976], "E40.8.2.7": [0.07698185044301627, 0.046263486762399664, 0.9517245528222696, -0.3069533768428862, 0.0012113596359206152, 0.0005476982455656242, 1.8115872085407847, 3.8684587889580118], "E40.8.2.8": [0.07635259941116963, 0.045696906588446363, 0.9942928282355765, 0.10668538662487148, 0.0012113596359206152, 0.0005476982455656242, 1.8115872085407754, 3.8684587889580224], "E40.8.2.9": [0.07600819890729629, 0.0449233703917957, 0.8649388407801819, 0.5018772775388773, 0.001211359635920615, 0.000547698245565624, 1.8115872085407754, 3.8684587889580158], "E40.8.2.10": [0.07600819890729629, 0.04407662960820429, 0.5860290700312074, 0.8102900277544814, 0.0012113596359206152, 0.0005476982455656242, 1.8115872085407756, 3.868458788958045], "E40.8.2.11": [0.07635259941116966, 0.04330309341155364, 0.20578954916687192, 0.97859627091753, 0.0012113596359206152, 0.0005476982455656242, 1.811587208540781, 3.868458788957996], "E40.8.2.12": [0.07698185044301628, 0.042736513237600346, -0.2100328542877775, 0.9776943285709134, 0.0012113596359206152, 0.0005476982455656242, 1.8115872085407831, 3.868458788958], "E40.8.2.13": [0.07778714878286375, 0.04247485594564024, -0.5895386691474909, 0.8077401547402515, 0.0012113596359206152, 0.0005476982455656242, 1.8115872085407836, 3.868458788958025], "E40.8.2.14": [0.07862925103184669, 0.042563364458535105, -0.8671078923209321, 0.4981203700660625, 0.0012113596359206152, 0.0005476982455656242, 1.811587208540779, 3.868458788957983], "E40.8.3.0": [0.07936255006085717, 0.0652367348503308, -0.9947462834841825, 0.10237104812595471, 0.0012113596359206152, 0.0005476982455656242, 1.8115872085408105, 3.8684587889580255], "E40.8.3.1": [0.07986025180596679, 0.06592176253408662, -0.9503840052467358, -0.31107915804690683, 0.0012113596359206152, 0.0005476982455656242, 1.8115872085407603, 3.8684587889580175], "E40.8.3.2": [0.08003629911396762, 0.06675, -0.741691698534492, -0.6707409517280276, 0.0012113596359206152, 0.0005476982455656242, 1.8115872085407871, 3.868458788958009], "E40.8.3.3": [0.07986025180596677, 0.06757823746591339, -0.40475415908808526, -0.9144255413651223, 0.0012113596359206152, 0.0005476982455656242, 1.8115872085407922, 3.868458788958005], "E40.8.3.4": [0.07936255006085718, 0.06826326514966921, 0.002169051540750866, -0.99999764760494, 0.0012113596359206152, 0.0005476982455656242, 1.8115872085407712, 3.8684587889580273], "E40.8.3.5": [0.07862925103184668, 0.0686866355414649, 0.40871721345297557, -0.912661075880436, 0.0012113596359206152, 0.0005476982455656242, 1.8115872085407727, 3.868458788958004], "E40.8.3.6": [0.07778714878286375, 0.06877514405435975, 0.7445944560798636, -0.6675171128706231, 0.0012113596359206152, 0.0005476982455656242, 1.8115872085407987, 3.868458788957976], "E40.8.3.7": [0.07698185044301627, 0.06851348676239967, 0.9517245528222696, -0.3069533768428862, 0.0012113596359206152, 0.0005476982455656242, 1.8115872085407858, 3.8684587889580118], "E40.8.3.8": [0.07635259941116963, 0.06794690658844638, 0.9942928282355765, 0.10668538662487148, 0.0012113596359206152, 0.0005476982455656242, 1.8115872085407754, 3.8684587889580224], "E40.8.3.9": [0.07600819890729629, 0.0671733703917957, 0.8649388407801819, 0.5018772775388773, 0.001211359635920615, 0.000547698245565624, 1.8115872085407754, 3.868458788958016], "E40.8.3.10": [0.07600819890729629, 0.0663266296082043, 0.5860290700312074, 0.8102900277544814, 0.0012113596359206152, 0.0005476982455656242, 1.8115872085407807, 3.868458788958045], "E40.8.3.11": [0.07635259941116966, 0.06555309341155365, 0.20578954916687192, 0.97859627091753, 0.0012113596359206152, 0.0005476982455656242, 1.8115872085407752, 3.868458788957996], "E40.8.3.12": [0.07698185044301628, 0.06498651323760035, -0.2100328542877775, 0.9776943285709134, 0.0012113596359206152, 0.0005476982455656242, 1.8115872085407776, 3.8684587889580073], "E40.8.3.13": [0.07778714878286375, 0.06472485594564024, -0.5895386691474909, 0.8077401547402515, 0.0012113596359206152, 0.0005476982455656242, 1.8115872085407836, 3.8684587889580175], "E40.8.3.14": [0.07862925103184669, 0.06481336445853511, -0.8671078923209321, 0.4981203700660625, 0.0012113596359206152, 0.0005476982455656242, 1.8115872085407811, 3.868458788957983], "E40.9.0.0": [0.10161255006085716, -0.0015132651496692073, -0.9947462834841825, 0.10237104812595471, 0.0012113596359206152, 0.0005476982455656242, 1.8115872085408105, 3.868458788958024], "E40.9.0.1": [0.10211025180596678, -0.0008282374659133868, -0.9503840052467358, -0.31107915804690683, 0.0012113596359206152, 0.0005476982455656242, 1.8115872085407585, 3.868458788958019], "E40.9.0.2": [0.10228629911396761, 0, -0.741691698534492, -0.6707409517280276, 0.0012113596359206152, 0.0005476982455656242, 1.8115872085407891, 3.8684587889580095], "E40.9.0.3": [0.10211025180596676, 0.0008282374659133868, -0.40475415908808526, -0.9144255413651223, 0.0012113596359206152, 0.0005476982455656242, 1.8115872085407905, 3.868458788958002], "E40.9.0.4": [0.10161255006085718, 0.0015132651496692073, 0.002169051540750866, -0.99999764760494, 0.0012113596359206152, 0.0005476982455656242, 1.8115872085407774, 3.8684587889580273], "E40.9.0.5": [0.10087925103184667, 0.0019366355414648928, 0.40871721345297557, -0.912661075880436, 0.0012113596359206152, 0.0005476982455656242, 1.8115872085407752, 3.8684587889580113], "E40.9.0.6": [0.10003714878286374, 0.0020251440543597454, 0.7445944560798636, -0.6675171128706231, 0.0012113596359206152, 0.0005476982455656242, 1.811587208540798, 3.8684587889579767], "E40.9.0.7": [0.09923185044301626, 0.0017634867623996658, 0.9517245528222696, -0.3069533768428862, 0.0012113596359206152, 0.0005476982455656242, 1.811587208540785, 3.8684587889580127], "E40.9.0.8": [0.09860259941116963, 0.0011969065884463656, 0.9942928282355765, 0.10668538662487148, 0.0012113596359206152, 0.0005476982455656242, 1.8115872085407754, 3.868458788958021], "E40.9.0.9": [0.09825819890729628, 0.0004233703917957028, 0.8649388407801819, 0.5018772775388773, 0.001211359635920615, 0.000547698245565624, 1.8115872085407738, 3.8684587889580158], "E40.9.0.10": [0.09825819890729628, -0.0004233703917957062, 0.5860290700312074, 0.8102900277544814, 0.0012113596359206152, 0.0005476982455656242, 1.811587208540776, 3.868458788958045], "E40.9.0.11": [0.09860259941116965, -0.0011969065884463587, 0.20578954916687192, 0.97859627091753, 0.0012113596359206152, 0.0005476982455656242, 1.8115872085407798, 3.8684587889579958], "E40.9.0.12": [0.09923185044301627, -0.001763486762399652, -0.2100328542877775, 0.9776943285709134, 0.0012113596359206152, 0.0005476982455656242, 1.8115872085407814, 3.868458788958003], "E40.9.0.13": [0.10003714878286374, -0.0020251440543597593, -0.5895386691474909, 0.8077401547402515, 0.0012113596359206152, 0.0005476982455656242, 1.8115872085407858, 3.8684587889580233], "E40.9.0.14": [0.10087925103184668, -0.0019366355414648928, -0.8671078923209321, 0.4981203700660625, 0.0012113596359206152, 0.0005476982455656242, 1.8115872085407796, 3.8684587889579802], "E40.9.1.0": [0.10161255006085716, 0.02073673485033079, -0.9947462834841825, 0.10237104812595471, 0.0012113596359206152, 0.0005476982455656242, 1.8115872085408105, 3.8684587889580238], "E40.9.1.1": [0.10211025180596678, 0.021421762534086612, -0.9503840052467358, -0.31107915804690683, 0.0012113596359206152, 0.0005476982455656242, 1.8115872085407578, 3.868458788958019], "E40.9.1.2": [0.10228629911396761, 0.02225, -0.741691698534492, -0.6707409517280276, 0.0012113596359206152, 0.0005476982455656242, 1.8115872085407894, 3.86845878895801], "E40.9.1.3": [0.10211025180596676, 0.023078237465913386, -0.40475415908808526, -0.9144255413651223, 0.0012113596359206152, 0.0005476982455656242, 1.8115872085407896, 3.868458788958003], "E40.9.1.4": [0.10161255006085718, 0.023763265149669206, 0.002169051540750866, -0.99999764760494, 0.0012113596359206152, 0.0005476982455656242, 1.8115872085407771, 3.8684587889580273], "E40.9.1.5": [0.10087925103184667, 0.024186635541464892, 0.40871721345297557, -0.912661075880436, 0.0012113596359206152, 0.0005476982455656242, 1.8115872085407752, 3.8684587889580118], "E40.9.1.6": [0.10003714878286374, 0.024275144054359744, 0.7445944560798636, -0.6675171128706231, 0.0012113596359206152, 0.0005476982455656242, 1.8115872085407987, 3.868458788957976], "E40.9.1.7": [0.09923185044301626, 0.024013486762399665, 0.9517245528222696, -0.3069533768428862, 0.0012113596359206152, 0.0005476982455656242, 1.8115872085407854, 3.8684587889580118], "E40.9.1.8": [0.09860259941116963, 0.023446906588446365, 0.9942928282355765, 0.10668538662487148, 0.0012113596359206152, 0.0005476982455656242, 1.8115872085407754, 3.8684587889580206], "E40.9.1.9": [0.09825819890729628, 0.022673370391795702, 0.8649388407801819, 0.5018772775388773, 0.001211359635920615, 0.000547698245565624, 1.8115872085407736, 3.8684587889580158], "E40.9.1.10": [0.09825819890729628, 0.021826629608204293, 0.5860290700312074, 0.8102900277544814, 0.0012113596359206152, 0.0005476982455656242, 1.8115872085407756, 3.868458788958045], "E40.9.1.11": [0.09860259941116965, 0.02105309341155364, 0.20578954916687192, 0.97859627091753, 0.0012113596359206152, 0.0005476982455656242, 1.811587208540781, 3.868458788957996], "E40.9.1.12": [0.09923185044301627, 0.020486513237600347, -0.2100328542877775, 0.9776943285709134, 0.0012113596359206152, 0.0005476982455656242, 1.8115872085407831, 3.8684587889580038], "E40.9.1.13": [0.10003714878286374, 0.02022485594564024, -0.5895386691474909, 0.8077401547402515, 0.0012113596359206152, 0.0005476982455656242, 1.8115872085407858, 3.868458788958025], "E40.9.1.14": [0.10087925103184668, 0.020313364458535106, -0.8671078923209321, 0.4981203700660625, 0.0012113596359206152, 0.0005476982455656242, 1.81158720854078, 3.868458788957983], "E40.9.2.0": [0.10161255006085716, 0.04298673485033079, -0.9947462834841825, 0.10237104812595471, 0.0012113596359206152, 0.0005476982455656242, 1.8115872085408105, 3.8684587889580255], "E40.9.2.1": [0.10211025180596678, 0.04367176253408661, -0.9503840052467358, -0.31107915804690683, 0.0012113596359206152, 0.0005476982455656242, 1.8115872085407578, 3.868458788958019], "E40.9.2.2": [0.10228629911396761, 0.0445, -0.741691698534492, -0.6707409517280276, 0.0012113596359206152, 0.0005476982455656242, 1.8115872085407914, 3.868458788958009], "E40.9.2.3": [0.10211025180596676, 0.045328237465913385, -0.40475415908808526, -0.9144255413651223, 0.0012113596359206152, 0.0005476982455656242, 1.8115872085407922, 3.868458788958], "E40.9.2.4": [0.10161255006085718, 0.046013265149669205, 0.002169051540750866, -0.99999764760494, 0.0012113596359206152, 0.0005476982455656242, 1.8115872085407771, 3.8684587889580273], "E40.9.2.5": [0.10087925103184667, 0.04643663554146489, 0.40871721345297557, -0.912661075880436, 0.0012113596359206152, 0.0005476982455656242, 1.8115872085407778, 3.8684587889580118], "E40.9.2.6": [0.10003714878286374, 0.04652514405435974, 0.7445944560798636, -0.6675171128706231, 0.0012113596359206152, 0.0005476982455656242, 1.8115872085407987, 3.868458788957976], "E40.9.2.7": [0.09923185044301626, 0.046263486762399664, 0.9517245528222696, -0.3069533768428862, 0.0012113596359206152, 0.0005476982455656242, 1.8115872085407847, 3.8684587889580118], "E40.9.2.8": [0.09860259941116963, 0.045696906588446363, 0.9942928282355765, 0.10668538662487148, 0.0012113596359206152, 0.0005476982455656242, 1.8115872085407754, 3.8684587889580224], "E40.9.2.9": [0.09825819890729628, 0.0449233703917957, 0.8649388407801819, 0.5018772775388773, 0.001211359635920615, 0.000547698245565624, 1.8115872085407754, 3.8684587889580158], "E40.9.2.10": [0.09825819890729628, 0.04407662960820429, 0.5860290700312074, 0.8102900277544814, 0.0012113596359206152, 0.0005476982455656242, 1.8115872085407756, 3.868458788958045], "E40.9.2.11": [0.09860259941116965, 0.04330309341155364, 0.20578954916687192, 0.97859627091753, 0.0012113596359206152, 0.0005476982455656242, 1.811587208540781, 3.868458788957996], "E40.9.2.12": [0.09923185044301627, 0.042736513237600346, -0.2100328542877775, 0.9776943285709134, 0.0012113596359206152, 0.0005476982455656242, 1.8115872085407831, 3.868458788958], "E40.9.2.13": [0.10003714878286374, 0.04247485594564024, -0.5895386691474909, 0.8077401547402515, 0.0012113596359206152, 0.0005476982455656242, 1.8115872085407836, 3.868458788958025], "E40.9.2.14": [0.10087925103184668, 0.042563364458535105, -0.8671078923209321, 0.4981203700660625, 0.0012113596359206152, 0.0005476982455656242, 1.811587208540779, 3.868458788957983], "E40.9.3.0": [0.10161255006085716, 0.0652367348503308, -0.9947462834841825, 0.10237104812595471, 0.0012113596359206152, 0.0005476982455656242, 1.8115872085408105, 3.8684587889580255], "E40.9.3.1": [0.10211025180596678, 0.06592176253408662, -0.9503840052467358, -0.31107915804690683, 0.0012113596359206152, 0.0005476982455656242, 1.8115872085407603, 3.8684587889580175], "E40.9.3.2": [0.10228629911396761, 0.06675, -0.741691698534492, -0.6707409517280276, 0.0012113596359206152, 0.0005476982455656242, 1.8115872085407871, 3.868458788958009], "E40.9.3.3": [0.10211025180596676, 0.06757823746591339, -0.40475415908808526, -0.9144255413651223, 0.0012113596359206152, 0.0005476982455656242, 1.8115872085407922, 3.868458788958005], "E40.9.3.4": [0.10161255006085718, 0.06826326514966921, 0.002169051540750866, -0.99999764760494, 0.0012113596359206152, 0.0005476982455656242, 1.8115872085407712, 3.8684587889580273], "E40.9.3.5": [0.10087925103184667, 0.0686866355414649, 0.40871721345297557, -0.912661075880436, 0.0012113596359206152, 0.0005476982455656242, 1.8115872085407727, 3.868458788958004], "E40.9.3.6": [0.10003714878286374, 0.06877514405435975, 0.7445944560798636, -0.6675171128706231, 0.0012113596359206152, 0.0005476982455656242, 1.8115872085407987, 3.868458788957976], "E40.9.3.7": [0.09923185044301626, 0.06851348676239967, 0.9517245528222696, -0.3069533768428862, 0.0012113596359206152, 0.0005476982455656242, 1.8115872085407858, 3.8684587889580118], "E40.9.3.8": [0.09860259941116963, 0.06794690658844638, 0.9942928282355765, 0.10668538662487148, 0.0012113596359206152, 0.0005476982455656242, 1.8115872085407754, 3.8684587889580224], "E40.9.3.9": [0.09825819890729628, 0.0671733703917957, 0.8649388407801819, 0.5018772775388773, 0.001211359635920615, 0.000547698245565624, 1.8115872085407754, 3.868458788958016], "E40.9.3.10": [0.09825819890729628, 0.0663266296082043, 0.5860290700312074, 0.8102900277544814, 0.0012113596359206152, 0.0005476982455656242, 1.8115872085407807, 3.868458788958045], "E40.9.3.11": [0.09860259941116965, 0.06555309341155365, 0.20578954916687192, 0.97859627091753, 0.0012113596359206152, 0.0005476982455656242, 1.8115872085407752, 3.868458788957996], "E40.9.3.12": [0.09923185044301627, 0.06498651323760035, -0.2100328542877775, 0.9776943285709134, 0.0012113596359206152, 0.0005476982455656242, 1.8115872085407776, 3.8684587889580073], "E40.9.3.13": [0.10003714878286374, 0.06472485594564024, -0.5895386691474909, 0.8077401547402515, 0.0012113596359206152, 0.0005476982455656242, 1.8115872085407836, 3.8684587889580175], "E40.9.3.14": [0.10087925103184668, 0.06481336445853511, -0.8671078923209321, 0.4981203700660625, 0.0012113596359206152, 0.0005476982455656242, 1.8115872085407811, 3.868458788957983], "E42": [-0.09433333442604606, -0.07596045306760557, 0, -1, 0.003350724066908284, 0.001398073716455388, 3.999467100408776, 2.5658668739144703], "E43": [-0.09699647773835246, -0.069949058671853, 0.4696130912697798, -0.8828723262782913, 0.00417825352559616, 0.0023973383681521335, 0.5111390050749848, 0.8169980815897804], "E45.MirrorCS": [-0.09297007770587269, -0.06850136345783646, 0.2001031237869894, -0.9797748414052532, 0.00417825352559616, 0.0023973383681521335, 0.1576384270288582, 4.452648440843217], "E46.MirrorCS": [-0.09119554182140502, -0.07483225733452598, 0.6367806024140514, -0.7710450469260522, 0.003350724066908284, 0.001398073716455388, 3.201412664403824, 3.7173184332651266], "E47.trimOffspring": [-0.09699647773835246, -0.069949058671853, 0.4696130912697798, -0.8828723262782913, 0.00417825352559616, 0.0023973383681521335, 1.8305368663362123, 6.125546880150718], "E48.trimOffspring": [-0.09297007770587269, -0.06850136345783646, 0.2001031237869894, -0.9797748414052532, 0.00417825352559616, 0.0023973383681521335, 5.466187225589829, 5.772046302104604], "E49.trimOffspring": [-0.09433333442604606, -0.07596045306760557, 0, -1, 0.003350724066908284, 0.001398073716455388, 2.5658668739144703, 3.0817726427757735], "E50.trimOffspring": [-0.09119554182140502, -0.07483225733452598, 0.6367806024140514, -0.7710450469260522, 0.003350724066908284, 0.001398073716455388, 3.7173184332651266, 2.2837182067708244], "E52.MirrorCS": [-0.008847360657390793, -0.05784149602032215, 0.050607726231367355, -0.9987186080401681, 0.004178253525596159, 0.002397338368152133, 1.8305368663363706, 6.125546880150719], "E53.MirrorCS": [-0.004587124748511848, -0.058239124810700524, -0.2345542129721361, -0.972103040411366, 0.004178253525596159, 0.002397338368152133, 0.15763842702886952, 4.45264844084337], "E54.MirrorCS": [-0.008986687583956168, -0.0644149108779667, -0.42433117184485264, -0.9055070715354873, 0.0033507240669082834, 0.0013980737164553877, 3.999467100408766, 2.5658668739144543], "E55.MirrorCS": [-0.005666665573953941, -0.06472478487652056, 0.2494308901952482, -0.968392601694378, 0.0033507240669082834, 0.0013980737164553877, 3.7173184332650755, 2.283718206770833], "E56.1.0.0": [-0.06377467250219067, -0.06458565031987797, 0.2001031237869894, -0.9797748414052532, 0.00417825352559616, 0.0023973383681521335, 0.1576384270288582, 4.452648440843217], "E56.1.0.1": [-0.06780107253467044, -0.0660333455338945, 0.4696130912697798, -0.8828723262782913, 0.00417825352559616, 0.0023973383681521335, 1.8305368663362123, 6.125546880150718], "E56.1.0.2": [-0.06513792922236404, -0.07204473992964708, 0, -1, 0.003350724066908284, 0.001398073716455388, 3.999467100408776, 2.5658668739144703], "E56.1.0.3": [-0.062000136617722995, -0.07091654419656748, 0.6367806024140514, -0.7710450469260522, 0.003350724066908284, 0.001398073716455388, 3.7173184332651266, 2.2837182067708244], "E57.0.1.0": [-0.01465527290842565, -0.024921615000959366, 0.050607726231367355, -0.9987186080401681, 0.004178253525596159, 0.002397338368152133, 1.8305368663363706, 6.12554688015072], "E57.0.1.1": [-0.0103950369995467, -0.025319243791337723, -0.2345542129721361, -0.972103040411366, 0.004178253525596159, 0.002397338368152133, 0.15763842702886952, 4.452648440843373], "E57.0.1.2": [-0.011474577824988794, -0.03180490385715776, 0.2494308901952482, -0.968392601694378, 0.0033507240669082834, 0.0013980737164553877, 3.717318433265075, 2.283718206770833], "E57.0.1.3": [-0.014794599834991025, -0.03149502985860392, -0.4243311718448526, -0.9055070715354873, 0.0033507240669082834, 0.0013980737164553877, 3.9994671004087614, 2.5658668739144597], "E57.0.1.4": [-0.06958258475322553, -0.03166576930051518, 0.20010312378698944, -0.9797748414052532, 0.00417825352559616, 0.0023973383681521335, 0.1576384270288594, 4.452648440843217], "E57.0.1.5": [-0.0736089847857053, -0.033113464514531704, 0.4696130912697798, -0.8828723262782913, 0.00417825352559616, 0.0023973383681521335, 1.8305368663362096, 6.1255468801507185], "E57.0.1.6": [-0.0709458414733989, -0.03912485891028428, 0, -1, 0.003350724066908284, 0.001398073716455388, 3.999467100408776, 2.5658668739144703], "E57.0.1.7": [-0.06780804886875785, -0.037996663177204695, 0.6367806024140514, -0.7710450469260521, 0.003350724066908284, 0.001398073716455388, 3.717318433265119, 2.2837182067708257], "E57.0.1.8": [-0.09700345407243988, -0.04191237631516319, 0.6367806024140514, -0.7710450469260521, 0.003350724066908284, 0.001398073716455388, 3.717318433265119, 2.2837182067708257], "E57.0.1.9": [-0.10014124667708092, -0.04304057204824277, 0, -1, 0.003350724066908284, 0.001398073716455388, 3.999467100408776, 2.5658668739144757], "E57.0.1.10": [-0.10280438998938732, -0.0370291776524902, 0.4696130912697798, -0.8828723262782913, 0.00417825352559616, 0.0023973383681521335, 1.8305368663362096, 6.1255468801507185], "E57.0.1.11": [-0.09877798995690755, -0.03558148243847367, 0.20010312378698944, -0.9797748414052532, 0.00417825352559616, 0.0023973383681521335, 0.1576384270288594, 4.452648440843217], "E58.MirrorCS": [0.004587124748511848, -0.058239124810700524, 0.2345542129721361, -0.972103040411366, 0.004178253525596159, 0.002397338368152133, 1.8305368663362165, 6.125546880150717], "E59.MirrorCS": [0.008847360657390793, -0.05784149602032215, -0.05060772623136735, -0.9987186080401681, 0.004178253525596159, 0.002397338368152133, 0.15763842702886627, 4.452648440843216], "E60.MirrorCS": [0.0103950369995467, -0.025319243791337723, 0.2345542129721361, -0.972103040411366, 0.004178253525596159, 0.002397338368152133, 1.8305368663362132, 6.125546880150717], "E61.MirrorCS": [0.011474577824988794, -0.03180490385715776, -0.2494308901952482, -0.968392601694378, 0.0033507240669082834, 0.0013980737164553877, 3.999467100408753, 2.565866873914511], "E62.MirrorCS": [0.01479459983499102, -0.03149502985860392, 0.4243311718448526, -0.9055070715354873, 0.0033507240669082834, 0.0013980737164553877, 3.717318433265126, 2.283718206770824], "E63.MirrorCS": [0.014655272908425644, -0.024921615000959366, -0.050607726231367355, -0.9987186080401681, 0.004178253525596159, 0.002397338368152133, 0.1576384270288679, 4.452648440843215], "E64.MirrorCS": [0.06958258475322551, -0.03166576930051518, -0.20010312378698944, -0.9797748414052532, 0.00417825352559616, 0.0023973383681521335, 1.8305368663363695, 6.125546880150731], "E65.MirrorCS": [0.0736089847857053, -0.033113464514531704, -0.4696130912697798, -0.8828723262782913, 0.00417825352559616, 0.0023973383681521335, 0.15763842702886816, 4.452648440843377], "E66.MirrorCS": [0.09877798995690754, -0.03558148243847367, -0.20010312378698944, -0.9797748414052532, 0.00417825352559616, 0.0023973383681521335, 1.8305368663363695, 6.125546880150731], "E67.MirrorCS": [0.10280438998938732, -0.0370291776524902, -0.4696130912697798, -0.8828723262782913, 0.00417825352559616, 0.0023973383681521335, 0.15763842702886816, 4.452648440843377], "E68.MirrorCS": [0.09297007770587269, -0.06850136345783646, -0.2001031237869894, -0.9797748414052532, 0.00417825352559616, 0.0023973383681521335, 1.8305368663363693, 6.125546880150731], "E69.MirrorCS": [0.09699647773835246, -0.069949058671853, -0.4696130912697798, -0.8828723262782913, 0.00417825352559616, 0.0023973383681521335, 0.15763842702886874, 4.452648440843374], "E70.MirrorCS": [0.09119554182140502, -0.07483225733452598, -0.6367806024140514, -0.7710450469260521, 0.003350724066908284, 0.001398073716455388, 3.9994671004087627, 2.5658668739144606], "E71.MirrorCS": [0.09433333442604606, -0.07596045306760557, 0, -1, 0.003350724066908284, 0.001398073716455388, 3.717318433265116, 2.28371820677081], "E72.MirrorCS": [0.005666665573953941, -0.06472478487652056, -0.2494308901952482, -0.968392601694378, 0.0033507240669082834, 0.0013980737164553877, 3.999467100408753, 2.565866873914511], "E73.MirrorCS": [0.008986687583956168, -0.0644149108779667, 0.42433117184485264, -0.9055070715354873, 0.0033507240669082834, 0.0013980737164553877, 3.717318433265131, 2.2837182067708204], "E74.MirrorCS": [0.06780804886875785, -0.037996663177204695, -0.6367806024140514, -0.7710450469260521, 0.003350724066908284, 0.001398073716455388, 3.9994671004087614, 2.565866873914467], "E75.MirrorCS": [0.0709458414733989, -0.03912485891028428, 0, -1, 0.003350724066908284, 0.001398073716455388, 3.717318433265116, 2.28371820677081], "E76.MirrorCS": [0.06377467250219067, -0.06458565031987797, -0.2001031237869894, -0.9797748414052532, 0.00417825352559616, 0.0023973383681521335, 1.8305368663363708, 6.125546880150731], "E77.MirrorCS": [0.06780107253467044, -0.0660333455338945, -0.4696130912697798, -0.8828723262782913, 0.00417825352559616, 0.0023973383681521335, 0.15763842702886874, 4.452648440843374], "E78.MirrorCS": [0.06513792922236404, -0.07204473992964708, 0, -1, 0.003350724066908284, 0.001398073716455388, 3.717318433265116, 2.28371820677081], "E79.MirrorCS": [0.062000136617722995, -0.07091654419656748, -0.6367806024140514, -0.7710450469260521, 0.003350724066908284, 0.001398073716455388, 3.9994671004087627, 2.5658668739144606]};
            skSetInitialGuess(sketch, initialGuessF0);
            skSolve(sketch);
        }
        {
            var Q0;
            Q0=makeQuery(id+"F0.imprint","IMPRINT",FACE,{"disambiguationData":[TD([[makeQuery(id+"F0.imprint","IMPRINT",EDGE,{"derivedFrom":sQuery(id+"F0.wireOp",EDGE,"E8")}),1.0]])]});
            extrude(context, id + "F1", {"entities" : qUnion([Q0]), "depth" : 1.5 * mm});
        }
        {
            var Q0;
            Q0=makeQuery(id+"F0.imprint","IMPRINT",FACE,{"disambiguationData":[TD([[makeQuery(id+"F0.imprint","IMPRINT",EDGE,{"derivedFrom":sQuery(id+"F0.wireOp",EDGE,"E14.0")}),1.0]])]});
            extrude(context, id + "F2", {"entities" : qUnion([Q0]), "operationType" : NewBodyOperationType.ADD, "depth" : 1.2 * mm});
        }
    });
